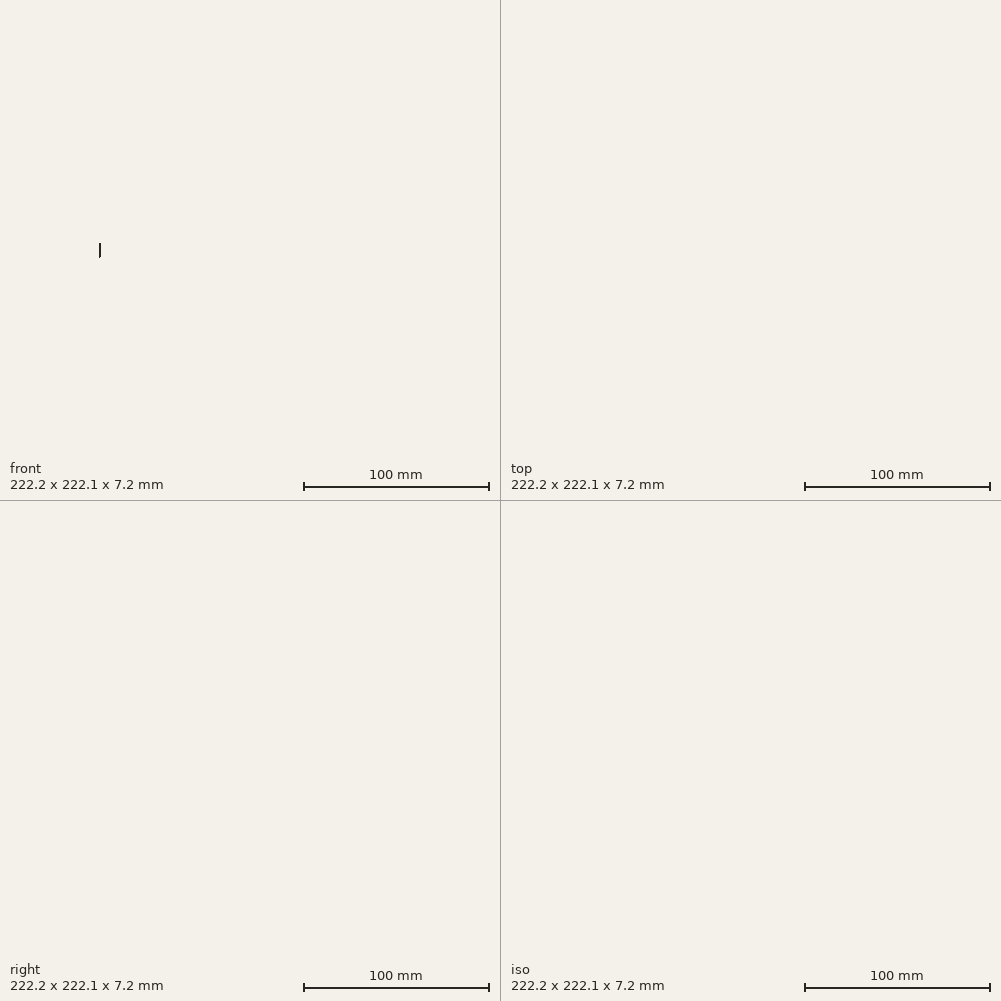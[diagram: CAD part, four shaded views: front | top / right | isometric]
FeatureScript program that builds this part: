
annotation { "Feature Type Name" : "Feature", "Feature Type Description" : "" }
export const myFeature = defineFeature(function(context is Context, id is Id, definition is map)
    precondition{}
    {
        {
            var Q0;
            Q0=qCreatedBy(makeId("Top.planeOp"),FACE);
            var sketch = newSketch(context, id + "F0", { "sketchPlane" : qUnion([Q0])});
            skCircle(sketch, "E0", {"center": v(0, 0) * mm, "radius": 101.6 * mm});
            skCircle(sketch, "E1", {"center": v(0, 0) * mm, "radius": 111.13 * mm});
            skSolve(sketch);
        }
        {
            var Q0;
            Q0=qSketchRegion(id+"F0",true);
            extrude(context, id + "F1", {"entities" : qUnion([Q0]), "depth" : 12.7 * mm});
        }
        {
            var Q0;
            Q0=makeQuery(id+"F1.opExtrude","CAP_FACE",FACE,{"disambiguationData":[OSD([sQuery(id+"F0.wireOp",EDGE,"E0"),sQuery(id+"F0.wireOp",EDGE,"E1")])],"isStart":false});
            var sketch = newSketch(context, id + "F2", { "sketchPlane" : qUnion([Q0])});
            skCircle(sketch, "E2", {"center": v(0, 0) * mm, "radius": 108.74 * mm, "construction": true});
            skCircle(sketch, "E3", {"center": v(0, 0) * mm, "radius": 112.9 * mm});
            skLineSegment(sketch, "E4", {"start": v(0, 0) * mm, "end": v(0, 111.13) * mm, "construction": true});
            skLineSegment(sketch, "E5", {"start": v(0, 0) * mm, "end": v(5.74, 110.98) * mm, "construction": true});
            skArc(sketch, "E6", {"start": v(1.35, 110.38) * mm, "mid": v(0.77, 110.93) * mm, "end": v(0, 111.13) * mm});
            skLineSegment(sketch, "E7", {"start": v(0, 0) * mm, "end": v(2.87, 111.09) * mm, "construction": true});
            skLineSegment(sketch, "E8", {"start": v(0, 111.12) * mm, "end": v(5.74, 110.98) * mm, "construction": true});
            skPoint(sketch, "E9", {"position": v(2.87, 111.05) * mm});
            skArc(sketch, "E10", {"start": v(2.16, 109.08) * mm, "mid": v(2.44, 108.81) * mm, "end": v(2.8, 108.7) * mm});
            skPoint(sketch, "E11", {"position": v(2.8, 108.7) * mm});
            skLineSegment(sketch, "E12", {"start": v(1.35, 110.38) * mm, "end": v(2.16, 109.08) * mm});
            skArc(sketch, "E13.MirrorCS", {"start": v(3.48, 109.05) * mm, "mid": v(3.19, 108.8) * mm, "end": v(2.8, 108.7) * mm});
            skLineSegment(sketch, "E14.MirrorCS", {"start": v(4.35, 110.3) * mm, "end": v(3.48, 109.05) * mm});
            skArc(sketch, "E15.MirrorCS", {"start": v(4.35, 110.3) * mm, "mid": v(4.96, 110.82) * mm, "end": v(5.74, 110.98) * mm});
            skArc(sketch, "E16.1.0", {"start": v(-4.34, 110.3) * mm, "mid": v(-4.94, 110.82) * mm, "end": v(-5.72, 110.98) * mm});
            skLineSegment(sketch, "E16.1.1", {"start": v(-4.34, 110.3) * mm, "end": v(-3.46, 109.05) * mm});
            skArc(sketch, "E16.1.2", {"start": v(-3.46, 109.05) * mm, "mid": v(-3.17, 108.8) * mm, "end": v(-2.8, 108.7) * mm});
            skArc(sketch, "E16.1.3", {"start": v(-2.14, 109.08) * mm, "mid": v(-2.42, 108.81) * mm, "end": v(-2.8, 108.7) * mm});
            skLineSegment(sketch, "E16.1.4", {"start": v(-1.33, 110.38) * mm, "end": v(-2.14, 109.08) * mm});
            skArc(sketch, "E16.1.5", {"start": v(-1.33, 110.38) * mm, "mid": v(-0.75, 110.93) * mm, "end": v(0.02, 111.12) * mm});
            skArc(sketch, "E16.2.0", {"start": v(-10, 109.93) * mm, "mid": v(-10.64, 110.42) * mm, "end": v(-11.43, 110.54) * mm});
            skLineSegment(sketch, "E16.2.1", {"start": v(-10, 109.93) * mm, "end": v(-9.07, 108.72) * mm});
            skArc(sketch, "E16.2.2", {"start": v(-9.07, 108.72) * mm, "mid": v(-8.77, 108.49) * mm, "end": v(-8.38, 108.42) * mm});
            skArc(sketch, "E16.2.3", {"start": v(-7.75, 108.83) * mm, "mid": v(-8.02, 108.54) * mm, "end": v(-8.38, 108.42) * mm});
            skLineSegment(sketch, "E16.2.4", {"start": v(-7, 110.16) * mm, "end": v(-7.75, 108.83) * mm});
            skArc(sketch, "E16.2.5", {"start": v(-7, 110.16) * mm, "mid": v(-6.46, 110.74) * mm, "end": v(-5.7, 110.98) * mm});
            skArc(sketch, "E16.3.0", {"start": v(-15.66, 109.27) * mm, "mid": v(-16.3, 109.72) * mm, "end": v(-17.1, 109.8) * mm});
            skLineSegment(sketch, "E16.3.1", {"start": v(-15.66, 109.27) * mm, "end": v(-14.66, 108.11) * mm});
            skArc(sketch, "E16.3.2", {"start": v(-14.66, 108.11) * mm, "mid": v(-14.34, 107.9) * mm, "end": v(-13.95, 107.84) * mm});
            skArc(sketch, "E16.3.3", {"start": v(-13.34, 108.28) * mm, "mid": v(-13.6, 107.99) * mm, "end": v(-13.95, 107.84) * mm});
            skLineSegment(sketch, "E16.3.4", {"start": v(-12.67, 109.66) * mm, "end": v(-13.34, 108.28) * mm});
            skArc(sketch, "E16.3.5", {"start": v(-12.67, 109.66) * mm, "mid": v(-12.15, 110.26) * mm, "end": v(-11.4, 110.54) * mm});
            skArc(sketch, "E16.4.0", {"start": v(-21.26, 108.32) * mm, "mid": v(-21.94, 108.74) * mm, "end": v(-22.73, 108.78) * mm});
            skLineSegment(sketch, "E16.4.1", {"start": v(-21.26, 108.32) * mm, "end": v(-20.2, 107.22) * mm});
            skArc(sketch, "E16.4.2", {"start": v(-20.2, 107.22) * mm, "mid": v(-19.87, 107) * mm, "end": v(-19.49, 106.98) * mm});
            skArc(sketch, "E16.4.3", {"start": v(-18.9, 107.45) * mm, "mid": v(-19.13, 107.14) * mm, "end": v(-19.49, 106.98) * mm});
            skLineSegment(sketch, "E16.4.4", {"start": v(-18.3, 108.86) * mm, "end": v(-18.9, 107.45) * mm});
            skArc(sketch, "E16.4.5", {"start": v(-18.3, 108.86) * mm, "mid": v(-17.81, 109.49) * mm, "end": v(-17.08, 109.8) * mm});
            skArc(sketch, "E16.5.0", {"start": v(-26.8, 107.08) * mm, "mid": v(-27.5, 107.46) * mm, "end": v(-28.3, 107.46) * mm});
            skLineSegment(sketch, "E16.5.1", {"start": v(-26.8, 107.08) * mm, "end": v(-25.7, 106.03) * mm});
            skArc(sketch, "E16.5.2", {"start": v(-25.7, 106.03) * mm, "mid": v(-25.36, 105.84) * mm, "end": v(-24.97, 105.84) * mm});
            skArc(sketch, "E16.5.3", {"start": v(-24.4, 106.34) * mm, "mid": v(-24.62, 106.02) * mm, "end": v(-24.97, 105.84) * mm});
            skLineSegment(sketch, "E16.5.4", {"start": v(-23.88, 107.77) * mm, "end": v(-24.4, 106.34) * mm});
            skArc(sketch, "E16.5.5", {"start": v(-23.88, 107.77) * mm, "mid": v(-23.43, 108.43) * mm, "end": v(-22.71, 108.78) * mm});
            skArc(sketch, "E16.6.0", {"start": v(-32.28, 105.56) * mm, "mid": v(-33, 105.9) * mm, "end": v(-33.8, 105.86) * mm});
            skLineSegment(sketch, "E16.6.1", {"start": v(-32.28, 105.56) * mm, "end": v(-31.12, 104.57) * mm});
            skArc(sketch, "E16.6.2", {"start": v(-31.12, 104.57) * mm, "mid": v(-30.77, 104.4) * mm, "end": v(-30.38, 104.41) * mm});
            skArc(sketch, "E16.6.3", {"start": v(-29.85, 104.94) * mm, "mid": v(-30.05, 104.6) * mm, "end": v(-30.38, 104.41) * mm});
            skLineSegment(sketch, "E16.6.4", {"start": v(-29.4, 106.4) * mm, "end": v(-29.85, 104.94) * mm});
            skArc(sketch, "E16.6.5", {"start": v(-29.4, 106.4) * mm, "mid": v(-28.98, 107.08) * mm, "end": v(-28.28, 107.47) * mm});
            skArc(sketch, "E16.7.0", {"start": v(-37.68, 103.76) * mm, "mid": v(-38.4, 104.07) * mm, "end": v(-39.2, 103.98) * mm});
            skLineSegment(sketch, "E16.7.1", {"start": v(-37.68, 103.76) * mm, "end": v(-36.46, 102.83) * mm});
            skArc(sketch, "E16.7.2", {"start": v(-36.46, 102.83) * mm, "mid": v(-36.1, 102.68) * mm, "end": v(-35.72, 102.71) * mm});
            skArc(sketch, "E16.7.3", {"start": v(-35.21, 103.26) * mm, "mid": v(-35.4, 102.92) * mm, "end": v(-35.72, 102.71) * mm});
            skLineSegment(sketch, "E16.7.4", {"start": v(-34.83, 104.75) * mm, "end": v(-35.21, 103.26) * mm});
            skArc(sketch, "E16.7.5", {"start": v(-34.83, 104.75) * mm, "mid": v(-34.45, 105.44) * mm, "end": v(-33.78, 105.87) * mm});
            skArc(sketch, "E16.8.0", {"start": v(-42.97, 101.68) * mm, "mid": v(-43.71, 101.95) * mm, "end": v(-44.5, 101.83) * mm});
            skLineSegment(sketch, "E16.8.1", {"start": v(-42.97, 101.68) * mm, "end": v(-41.7, 100.82) * mm});
            skArc(sketch, "E16.8.2", {"start": v(-41.7, 100.82) * mm, "mid": v(-41.34, 100.68) * mm, "end": v(-40.96, 100.74) * mm});
            skArc(sketch, "E16.8.3", {"start": v(-40.48, 101.31) * mm, "mid": v(-40.65, 100.96) * mm, "end": v(-40.96, 100.74) * mm});
            skLineSegment(sketch, "E16.8.4", {"start": v(-40.18, 102.81) * mm, "end": v(-40.48, 101.31) * mm});
            skArc(sketch, "E16.8.5", {"start": v(-40.18, 102.81) * mm, "mid": v(-39.83, 103.53) * mm, "end": v(-39.18, 103.99) * mm});
            skArc(sketch, "E16.9.0", {"start": v(-48.14, 99.33) * mm, "mid": v(-48.9, 99.57) * mm, "end": v(-49.68, 99.4) * mm});
            skLineSegment(sketch, "E16.9.1", {"start": v(-48.14, 99.33) * mm, "end": v(-46.84, 98.54) * mm});
            skArc(sketch, "E16.9.2", {"start": v(-46.84, 98.54) * mm, "mid": v(-46.47, 98.42) * mm, "end": v(-46.1, 98.5) * mm});
            skArc(sketch, "E16.9.3", {"start": v(-45.64, 99.1) * mm, "mid": v(-45.79, 98.74) * mm, "end": v(-46.1, 98.5) * mm});
            skLineSegment(sketch, "E16.9.4", {"start": v(-45.42, 100.6) * mm, "end": v(-45.64, 99.1) * mm});
            skArc(sketch, "E16.9.5", {"start": v(-45.42, 100.6) * mm, "mid": v(-45.11, 101.34) * mm, "end": v(-44.48, 101.83) * mm});
            skArc(sketch, "E16.10.0", {"start": v(-53.2, 96.72) * mm, "mid": v(-53.97, 96.92) * mm, "end": v(-54.73, 96.71) * mm});
            skLineSegment(sketch, "E16.10.1", {"start": v(-53.2, 96.72) * mm, "end": v(-51.85, 96) * mm});
            skArc(sketch, "E16.10.2", {"start": v(-51.85, 96) * mm, "mid": v(-51.48, 95.9) * mm, "end": v(-51.1, 95.99) * mm});
            skArc(sketch, "E16.10.3", {"start": v(-50.68, 96.62) * mm, "mid": v(-50.81, 96.25) * mm, "end": v(-51.1, 95.99) * mm});
            skLineSegment(sketch, "E16.10.4", {"start": v(-50.54, 98.14) * mm, "end": v(-50.68, 96.62) * mm});
            skArc(sketch, "E16.10.5", {"start": v(-50.54, 98.14) * mm, "mid": v(-50.27, 98.89) * mm, "end": v(-49.67, 99.4) * mm});
            skArc(sketch, "E16.11.0", {"start": v(-58.1, 93.86) * mm, "mid": v(-58.88, 94) * mm, "end": v(-59.64, 93.76) * mm});
            skLineSegment(sketch, "E16.11.1", {"start": v(-58.1, 93.86) * mm, "end": v(-56.72, 93.2) * mm});
            skArc(sketch, "E16.11.2", {"start": v(-56.72, 93.2) * mm, "mid": v(-56.34, 93.12) * mm, "end": v(-55.97, 93.23) * mm});
            skArc(sketch, "E16.11.3", {"start": v(-55.59, 93.88) * mm, "mid": v(-55.7, 93.5) * mm, "end": v(-55.97, 93.23) * mm});
            skLineSegment(sketch, "E16.11.4", {"start": v(-55.52, 95.4) * mm, "end": v(-55.59, 93.88) * mm});
            skArc(sketch, "E16.11.5", {"start": v(-55.52, 95.4) * mm, "mid": v(-55.3, 96.17) * mm, "end": v(-54.72, 96.72) * mm});
            skArc(sketch, "E16.12.0", {"start": v(-62.86, 90.74) * mm, "mid": v(-63.64, 90.85) * mm, "end": v(-64.39, 90.57) * mm});
            skLineSegment(sketch, "E16.12.1", {"start": v(-62.86, 90.74) * mm, "end": v(-61.45, 90.15) * mm});
            skArc(sketch, "E16.12.2", {"start": v(-61.45, 90.15) * mm, "mid": v(-61.06, 90.1) * mm, "end": v(-60.7, 90.23) * mm});
            skArc(sketch, "E16.12.3", {"start": v(-60.35, 90.9) * mm, "mid": v(-60.44, 90.52) * mm, "end": v(-60.7, 90.23) * mm});
            skLineSegment(sketch, "E16.12.4", {"start": v(-60.36, 92.42) * mm, "end": v(-60.35, 90.9) * mm});
            skArc(sketch, "E16.12.5", {"start": v(-60.36, 92.42) * mm, "mid": v(-60.17, 93.2) * mm, "end": v(-59.63, 93.77) * mm});
            skArc(sketch, "E16.13.0", {"start": v(-67.45, 87.39) * mm, "mid": v(-68.24, 87.46) * mm, "end": v(-68.97, 87.14) * mm});
            skLineSegment(sketch, "E16.13.1", {"start": v(-67.45, 87.39) * mm, "end": v(-66, 86.87) * mm});
            skArc(sketch, "E16.13.2", {"start": v(-66, 86.87) * mm, "mid": v(-65.62, 86.83) * mm, "end": v(-65.26, 86.98) * mm});
            skArc(sketch, "E16.13.3", {"start": v(-64.95, 87.67) * mm, "mid": v(-65.02, 87.28) * mm, "end": v(-65.26, 86.98) * mm});
            skLineSegment(sketch, "E16.13.4", {"start": v(-65.04, 89.2) * mm, "end": v(-64.95, 87.67) * mm});
            skArc(sketch, "E16.13.5", {"start": v(-65.04, 89.2) * mm, "mid": v(-64.89, 89.97) * mm, "end": v(-64.37, 90.58) * mm});
            skArc(sketch, "E16.14.0", {"start": v(-71.85, 83.8) * mm, "mid": v(-72.65, 83.83) * mm, "end": v(-73.36, 83.47) * mm});
            skLineSegment(sketch, "E16.14.1", {"start": v(-71.85, 83.8) * mm, "end": v(-70.4, 83.36) * mm});
            skArc(sketch, "E16.14.2", {"start": v(-70.4, 83.36) * mm, "mid": v(-70, 83.34) * mm, "end": v(-69.65, 83.5) * mm});
            skArc(sketch, "E16.14.3", {"start": v(-69.37, 84.2) * mm, "mid": v(-69.43, 83.82) * mm, "end": v(-69.65, 83.5) * mm});
            skLineSegment(sketch, "E16.14.4", {"start": v(-69.54, 85.72) * mm, "end": v(-69.37, 84.2) * mm});
            skArc(sketch, "E16.14.5", {"start": v(-69.54, 85.72) * mm, "mid": v(-69.43, 86.51) * mm, "end": v(-68.95, 87.15) * mm});
            skArc(sketch, "E16.15.0", {"start": v(-76.07, 79.99) * mm, "mid": v(-76.87, 79.98) * mm, "end": v(-77.56, 79.58) * mm});
            skLineSegment(sketch, "E16.15.1", {"start": v(-76.07, 79.99) * mm, "end": v(-74.59, 79.62) * mm});
            skArc(sketch, "E16.15.2", {"start": v(-74.59, 79.62) * mm, "mid": v(-74.2, 79.63) * mm, "end": v(-73.86, 79.81) * mm});
            skArc(sketch, "E16.15.3", {"start": v(-73.62, 80.52) * mm, "mid": v(-73.65, 80.14) * mm, "end": v(-73.86, 79.81) * mm});
            skLineSegment(sketch, "E16.15.4", {"start": v(-73.86, 82.03) * mm, "end": v(-73.62, 80.52) * mm});
            skArc(sketch, "E16.15.5", {"start": v(-73.86, 82.03) * mm, "mid": v(-73.8, 82.82) * mm, "end": v(-73.35, 83.48) * mm});
            skArc(sketch, "E16.16.0", {"start": v(-80.09, 75.97) * mm, "mid": v(-80.88, 75.91) * mm, "end": v(-81.55, 75.48) * mm});
            skLineSegment(sketch, "E16.16.1", {"start": v(-80.09, 75.97) * mm, "end": v(-78.59, 75.68) * mm});
            skArc(sketch, "E16.16.2", {"start": v(-78.59, 75.68) * mm, "mid": v(-78.2, 75.7) * mm, "end": v(-77.87, 75.9) * mm});
            skArc(sketch, "E16.16.3", {"start": v(-77.66, 76.63) * mm, "mid": v(-77.68, 76.24) * mm, "end": v(-77.87, 75.9) * mm});
            skLineSegment(sketch, "E16.16.4", {"start": v(-77.99, 78.12) * mm, "end": v(-77.66, 76.63) * mm});
            skArc(sketch, "E16.16.5", {"start": v(-77.99, 78.12) * mm, "mid": v(-77.96, 78.91) * mm, "end": v(-77.55, 79.6) * mm});
            skArc(sketch, "E16.17.0", {"start": v(-83.9, 71.74) * mm, "mid": v(-84.68, 71.65) * mm, "end": v(-85.33, 71.19) * mm});
            skLineSegment(sketch, "E16.17.1", {"start": v(-83.9, 71.74) * mm, "end": v(-82.38, 71.53) * mm});
            skArc(sketch, "E16.17.2", {"start": v(-82.38, 71.53) * mm, "mid": v(-82, 71.57) * mm, "end": v(-81.68, 71.8) * mm});
            skArc(sketch, "E16.17.3", {"start": v(-81.5, 72.53) * mm, "mid": v(-81.5, 72.14) * mm, "end": v(-81.68, 71.8) * mm});
            skLineSegment(sketch, "E16.17.4", {"start": v(-81.9, 74) * mm, "end": v(-81.5, 72.53) * mm});
            skArc(sketch, "E16.17.5", {"start": v(-81.9, 74) * mm, "mid": v(-81.92, 74.8) * mm, "end": v(-81.54, 75.5) * mm});
            skArc(sketch, "E16.18.0", {"start": v(-87.48, 67.33) * mm, "mid": v(-88.26, 67.2) * mm, "end": v(-88.88, 66.7) * mm});
            skLineSegment(sketch, "E16.18.1", {"start": v(-87.48, 67.33) * mm, "end": v(-85.95, 67.2) * mm});
            skArc(sketch, "E16.18.2", {"start": v(-85.95, 67.2) * mm, "mid": v(-85.57, 67.26) * mm, "end": v(-85.26, 67.5) * mm});
            skArc(sketch, "E16.18.3", {"start": v(-85.13, 68.23) * mm, "mid": v(-85.1, 67.85) * mm, "end": v(-85.26, 67.5) * mm});
            skLineSegment(sketch, "E16.18.4", {"start": v(-85.6, 69.69) * mm, "end": v(-85.13, 68.23) * mm});
            skArc(sketch, "E16.18.5", {"start": v(-85.6, 69.69) * mm, "mid": v(-85.66, 70.48) * mm, "end": v(-85.32, 71.2) * mm});
            skArc(sketch, "E16.19.0", {"start": v(-90.83, 62.74) * mm, "mid": v(-91.6, 62.56) * mm, "end": v(-92.2, 62.03) * mm});
            skLineSegment(sketch, "E16.19.1", {"start": v(-90.83, 62.74) * mm, "end": v(-89.3, 62.68) * mm});
            skArc(sketch, "E16.19.2", {"start": v(-89.3, 62.68) * mm, "mid": v(-88.92, 62.76) * mm, "end": v(-88.62, 63.02) * mm});
            skArc(sketch, "E16.19.3", {"start": v(-88.53, 63.76) * mm, "mid": v(-88.48, 63.38) * mm, "end": v(-88.62, 63.02) * mm});
            skLineSegment(sketch, "E16.19.4", {"start": v(-89.08, 65.19) * mm, "end": v(-88.53, 63.76) * mm});
            skArc(sketch, "E16.19.5", {"start": v(-89.08, 65.19) * mm, "mid": v(-89.17, 65.98) * mm, "end": v(-88.87, 66.71) * mm});
            skArc(sketch, "E16.20.0", {"start": v(-93.93, 57.98) * mm, "mid": v(-94.7, 57.76) * mm, "end": v(-95.27, 57.2) * mm});
            skLineSegment(sketch, "E16.20.1", {"start": v(-93.93, 57.98) * mm, "end": v(-92.4, 58) * mm});
            skArc(sketch, "E16.20.2", {"start": v(-92.4, 58) * mm, "mid": v(-92.03, 58.1) * mm, "end": v(-91.75, 58.37) * mm});
            skArc(sketch, "E16.20.3", {"start": v(-91.7, 59.12) * mm, "mid": v(-91.63, 58.74) * mm, "end": v(-91.75, 58.37) * mm});
            skLineSegment(sketch, "E16.20.4", {"start": v(-92.32, 60.51) * mm, "end": v(-91.7, 59.12) * mm});
            skArc(sketch, "E16.20.5", {"start": v(-92.32, 60.51) * mm, "mid": v(-92.45, 61.3) * mm, "end": v(-92.19, 62.05) * mm});
            skArc(sketch, "E16.21.0", {"start": v(-96.8, 53.06) * mm, "mid": v(-97.55, 52.81) * mm, "end": v(-98.09, 52.23) * mm});
            skLineSegment(sketch, "E16.21.1", {"start": v(-96.8, 53.06) * mm, "end": v(-95.27, 53.17) * mm});
            skArc(sketch, "E16.21.2", {"start": v(-95.27, 53.17) * mm, "mid": v(-94.9, 53.29) * mm, "end": v(-94.63, 53.57) * mm});
            skArc(sketch, "E16.21.3", {"start": v(-94.62, 54.32) * mm, "mid": v(-94.53, 53.94) * mm, "end": v(-94.63, 53.57) * mm});
            skLineSegment(sketch, "E16.21.4", {"start": v(-95.31, 55.68) * mm, "end": v(-94.62, 54.32) * mm});
            skArc(sketch, "E16.21.5", {"start": v(-95.31, 55.68) * mm, "mid": v(-95.49, 56.46) * mm, "end": v(-95.26, 57.22) * mm});
            skArc(sketch, "E16.22.0", {"start": v(-99.4, 48.01) * mm, "mid": v(-100.14, 47.72) * mm, "end": v(-100.65, 47.1) * mm});
            skLineSegment(sketch, "E16.22.1", {"start": v(-99.4, 48.01) * mm, "end": v(-97.88, 48.2) * mm});
            skArc(sketch, "E16.22.2", {"start": v(-97.88, 48.2) * mm, "mid": v(-97.52, 48.33) * mm, "end": v(-97.27, 48.63) * mm});
            skArc(sketch, "E16.22.3", {"start": v(-97.29, 49.38) * mm, "mid": v(-97.18, 49) * mm, "end": v(-97.27, 48.63) * mm});
            skLineSegment(sketch, "E16.22.4", {"start": v(-98.05, 50.7) * mm, "end": v(-97.29, 49.38) * mm});
            skArc(sketch, "E16.22.5", {"start": v(-98.05, 50.7) * mm, "mid": v(-98.27, 51.47) * mm, "end": v(-98.08, 52.24) * mm});
            skArc(sketch, "E16.23.0", {"start": v(-101.74, 42.83) * mm, "mid": v(-102.46, 42.5) * mm, "end": v(-102.94, 41.86) * mm});
            skLineSegment(sketch, "E16.23.1", {"start": v(-101.74, 42.83) * mm, "end": v(-100.23, 43.1) * mm});
            skArc(sketch, "E16.23.2", {"start": v(-100.23, 43.1) * mm, "mid": v(-99.88, 43.25) * mm, "end": v(-99.64, 43.55) * mm});
            skArc(sketch, "E16.23.3", {"start": v(-99.7, 44.3) * mm, "mid": v(-99.58, 43.94) * mm, "end": v(-99.64, 43.55) * mm});
            skLineSegment(sketch, "E16.23.4", {"start": v(-100.53, 45.59) * mm, "end": v(-99.7, 44.3) * mm});
            skArc(sketch, "E16.23.5", {"start": v(-100.53, 45.59) * mm, "mid": v(-100.78, 46.34) * mm, "end": v(-100.64, 47.12) * mm});
            skArc(sketch, "E16.24.0", {"start": v(-103.8, 37.54) * mm, "mid": v(-104.52, 37.17) * mm, "end": v(-104.96, 36.5) * mm});
            skLineSegment(sketch, "E16.24.1", {"start": v(-103.8, 37.54) * mm, "end": v(-102.32, 37.87) * mm});
            skArc(sketch, "E16.24.2", {"start": v(-102.32, 37.87) * mm, "mid": v(-101.97, 38.05) * mm, "end": v(-101.75, 38.37) * mm});
            skArc(sketch, "E16.24.3", {"start": v(-101.85, 39.11) * mm, "mid": v(-101.7, 38.75) * mm, "end": v(-101.75, 38.37) * mm});
            skLineSegment(sketch, "E16.24.4", {"start": v(-102.75, 40.35) * mm, "end": v(-101.85, 39.11) * mm});
            skArc(sketch, "E16.24.5", {"start": v(-102.75, 40.35) * mm, "mid": v(-103.04, 41.1) * mm, "end": v(-102.93, 41.88) * mm});
            skArc(sketch, "E16.25.0", {"start": v(-105.6, 32.14) * mm, "mid": v(-106.29, 31.74) * mm, "end": v(-106.7, 31.06) * mm});
            skLineSegment(sketch, "E16.25.1", {"start": v(-105.6, 32.14) * mm, "end": v(-104.13, 32.56) * mm});
            skArc(sketch, "E16.25.2", {"start": v(-104.13, 32.56) * mm, "mid": v(-103.8, 32.75) * mm, "end": v(-103.6, 33.08) * mm});
            skArc(sketch, "E16.25.3", {"start": v(-103.73, 33.82) * mm, "mid": v(-103.57, 33.47) * mm, "end": v(-103.6, 33.08) * mm});
            skLineSegment(sketch, "E16.25.4", {"start": v(-104.69, 35) * mm, "end": v(-103.73, 33.82) * mm});
            skArc(sketch, "E16.25.5", {"start": v(-104.69, 35) * mm, "mid": v(-105.02, 35.73) * mm, "end": v(-104.95, 36.53) * mm});
            skArc(sketch, "E16.26.0", {"start": v(-107.12, 26.66) * mm, "mid": v(-107.78, 26.23) * mm, "end": v(-108.15, 25.52) * mm});
            skLineSegment(sketch, "E16.26.1", {"start": v(-107.12, 26.66) * mm, "end": v(-105.67, 27.15) * mm});
            skArc(sketch, "E16.26.2", {"start": v(-105.67, 27.15) * mm, "mid": v(-105.34, 27.36) * mm, "end": v(-105.16, 27.7) * mm});
            skArc(sketch, "E16.26.3", {"start": v(-105.33, 28.43) * mm, "mid": v(-105.15, 28.1) * mm, "end": v(-105.16, 27.7) * mm});
            skLineSegment(sketch, "E16.26.4", {"start": v(-106.35, 29.57) * mm, "end": v(-105.33, 28.43) * mm});
            skArc(sketch, "E16.26.5", {"start": v(-106.35, 29.57) * mm, "mid": v(-106.72, 30.28) * mm, "end": v(-106.7, 31.08) * mm});
            skArc(sketch, "E16.27.0", {"start": v(-108.35, 21.11) * mm, "mid": v(-109, 20.64) * mm, "end": v(-109.32, 19.92) * mm});
            skLineSegment(sketch, "E16.27.1", {"start": v(-108.35, 21.11) * mm, "end": v(-106.93, 21.68) * mm});
            skArc(sketch, "E16.27.2", {"start": v(-106.93, 21.68) * mm, "mid": v(-106.61, 21.9) * mm, "end": v(-106.44, 22.25) * mm});
            skArc(sketch, "E16.27.3", {"start": v(-106.66, 22.97) * mm, "mid": v(-106.46, 22.64) * mm, "end": v(-106.44, 22.25) * mm});
            skLineSegment(sketch, "E16.27.4", {"start": v(-107.73, 24.06) * mm, "end": v(-106.66, 22.97) * mm});
            skArc(sketch, "E16.27.5", {"start": v(-107.73, 24.06) * mm, "mid": v(-108.13, 24.75) * mm, "end": v(-108.15, 25.54) * mm});
            skArc(sketch, "E16.28.0", {"start": v(-109.3, 15.5) * mm, "mid": v(-109.9, 15) * mm, "end": v(-110.2, 14.27) * mm});
            skLineSegment(sketch, "E16.28.1", {"start": v(-109.3, 15.5) * mm, "end": v(-107.9, 16.14) * mm});
            skArc(sketch, "E16.28.2", {"start": v(-107.9, 16.14) * mm, "mid": v(-107.6, 16.39) * mm, "end": v(-107.45, 16.74) * mm});
            skArc(sketch, "E16.28.3", {"start": v(-107.7, 17.45) * mm, "mid": v(-107.48, 17.13) * mm, "end": v(-107.45, 16.74) * mm});
            skLineSegment(sketch, "E16.28.4", {"start": v(-108.83, 18.48) * mm, "end": v(-107.7, 17.45) * mm});
            skArc(sketch, "E16.28.5", {"start": v(-108.83, 18.48) * mm, "mid": v(-109.26, 19.15) * mm, "end": v(-109.32, 19.94) * mm});
            skArc(sketch, "E16.29.0", {"start": v(-109.94, 9.86) * mm, "mid": v(-110.54, 9.33) * mm, "end": v(-110.8, 8.58) * mm});
            skLineSegment(sketch, "E16.29.1", {"start": v(-109.94, 9.86) * mm, "end": v(-108.59, 10.57) * mm});
            skArc(sketch, "E16.29.2", {"start": v(-108.59, 10.57) * mm, "mid": v(-108.3, 10.83) * mm, "end": v(-108.17, 11.19) * mm});
            skArc(sketch, "E16.29.3", {"start": v(-108.45, 11.89) * mm, "mid": v(-108.22, 11.57) * mm, "end": v(-108.17, 11.19) * mm});
            skLineSegment(sketch, "E16.29.4", {"start": v(-109.63, 12.85) * mm, "end": v(-108.45, 11.89) * mm});
            skArc(sketch, "E16.29.5", {"start": v(-109.63, 12.85) * mm, "mid": v(-110.1, 13.5) * mm, "end": v(-110.2, 14.29) * mm});
            skArc(sketch, "E16.30.0", {"start": v(-110.3, 4.19) * mm, "mid": v(-110.87, 3.63) * mm, "end": v(-111.09, 2.86) * mm});
            skLineSegment(sketch, "E16.30.1", {"start": v(-110.3, 4.19) * mm, "end": v(-108.99, 4.96) * mm});
            skArc(sketch, "E16.30.2", {"start": v(-108.99, 4.96) * mm, "mid": v(-108.71, 5.24) * mm, "end": v(-108.6, 5.6) * mm});
            skArc(sketch, "E16.30.3", {"start": v(-108.92, 6.29) * mm, "mid": v(-108.67, 5.99) * mm, "end": v(-108.6, 5.6) * mm});
            skLineSegment(sketch, "E16.30.4", {"start": v(-110.15, 7.2) * mm, "end": v(-108.92, 6.29) * mm});
            skArc(sketch, "E16.30.5", {"start": v(-110.15, 7.2) * mm, "mid": v(-110.65, 7.81) * mm, "end": v(-110.8, 8.6) * mm});
            skArc(sketch, "E16.31.0", {"start": v(-110.38, -1.5) * mm, "mid": v(-110.9, -2.09) * mm, "end": v(-111.09, -2.86) * mm});
            skLineSegment(sketch, "E16.31.1", {"start": v(-110.38, -1.5) * mm, "end": v(-109.1, -0.65) * mm});
            skArc(sketch, "E16.31.2", {"start": v(-109.1, -0.65) * mm, "mid": v(-108.84, -0.37) * mm, "end": v(-108.74, 0) * mm});
            skArc(sketch, "E16.31.3", {"start": v(-109.1, 0.67) * mm, "mid": v(-108.84, 0.38) * mm, "end": v(-108.74, 0) * mm});
            skLineSegment(sketch, "E16.31.4", {"start": v(-110.38, 1.51) * mm, "end": v(-109.1, 0.67) * mm});
            skArc(sketch, "E16.31.5", {"start": v(-110.38, 1.51) * mm, "mid": v(-110.9, 2.1) * mm, "end": v(-111.09, 2.88) * mm});
            skArc(sketch, "E16.32.0", {"start": v(-110.15, -7.18) * mm, "mid": v(-110.65, -7.8) * mm, "end": v(-110.8, -8.58) * mm});
            skLineSegment(sketch, "E16.32.1", {"start": v(-110.15, -7.18) * mm, "end": v(-108.92, -6.27) * mm});
            skArc(sketch, "E16.32.2", {"start": v(-108.92, -6.27) * mm, "mid": v(-108.68, -5.97) * mm, "end": v(-108.6, -5.59) * mm});
            skArc(sketch, "E16.32.3", {"start": v(-109, -4.95) * mm, "mid": v(-108.71, -5.22) * mm, "end": v(-108.6, -5.59) * mm});
            skLineSegment(sketch, "E16.32.4", {"start": v(-110.3, -4.17) * mm, "end": v(-109, -4.95) * mm});
            skArc(sketch, "E16.32.5", {"start": v(-110.3, -4.17) * mm, "mid": v(-110.87, -3.6) * mm, "end": v(-111.09, -2.84) * mm});
            skArc(sketch, "E16.33.0", {"start": v(-109.64, -12.84) * mm, "mid": v(-110.1, -13.48) * mm, "end": v(-110.2, -14.27) * mm});
            skLineSegment(sketch, "E16.33.1", {"start": v(-109.64, -12.84) * mm, "end": v(-108.45, -11.87) * mm});
            skArc(sketch, "E16.33.2", {"start": v(-108.45, -11.87) * mm, "mid": v(-108.22, -11.56) * mm, "end": v(-108.17, -11.17) * mm});
            skArc(sketch, "E16.33.3", {"start": v(-108.6, -10.55) * mm, "mid": v(-108.3, -10.8) * mm, "end": v(-108.17, -11.17) * mm});
            skLineSegment(sketch, "E16.33.4", {"start": v(-109.95, -9.84) * mm, "end": v(-108.6, -10.55) * mm});
            skArc(sketch, "E16.33.5", {"start": v(-109.95, -9.84) * mm, "mid": v(-110.54, -9.31) * mm, "end": v(-110.8, -8.56) * mm});
            skArc(sketch, "E16.34.0", {"start": v(-108.83, -18.46) * mm, "mid": v(-109.27, -19.13) * mm, "end": v(-109.32, -19.92) * mm});
            skLineSegment(sketch, "E16.34.1", {"start": v(-108.83, -18.46) * mm, "end": v(-107.7, -17.44) * mm});
            skArc(sketch, "E16.34.2", {"start": v(-107.7, -17.44) * mm, "mid": v(-107.49, -17.11) * mm, "end": v(-107.45, -16.73) * mm});
            skArc(sketch, "E16.34.3", {"start": v(-107.9, -16.13) * mm, "mid": v(-107.6, -16.37) * mm, "end": v(-107.45, -16.73) * mm});
            skLineSegment(sketch, "E16.34.4", {"start": v(-109.3, -15.5) * mm, "end": v(-107.9, -16.13) * mm});
            skArc(sketch, "E16.34.5", {"start": v(-109.3, -15.5) * mm, "mid": v(-109.91, -14.99) * mm, "end": v(-110.2, -14.25) * mm});
            skArc(sketch, "E16.35.0", {"start": v(-107.74, -24.04) * mm, "mid": v(-108.14, -24.73) * mm, "end": v(-108.15, -25.52) * mm});
            skLineSegment(sketch, "E16.35.1", {"start": v(-107.74, -24.04) * mm, "end": v(-106.66, -22.96) * mm});
            skArc(sketch, "E16.35.2", {"start": v(-106.66, -22.96) * mm, "mid": v(-106.46, -22.62) * mm, "end": v(-106.45, -22.24) * mm});
            skArc(sketch, "E16.35.3", {"start": v(-106.93, -21.66) * mm, "mid": v(-106.62, -21.89) * mm, "end": v(-106.45, -22.24) * mm});
            skLineSegment(sketch, "E16.35.4", {"start": v(-108.35, -21.1) * mm, "end": v(-106.93, -21.66) * mm});
            skArc(sketch, "E16.35.5", {"start": v(-108.35, -21.1) * mm, "mid": v(-109, -20.63) * mm, "end": v(-109.33, -19.9) * mm});
            skArc(sketch, "E16.36.0", {"start": v(-106.36, -29.56) * mm, "mid": v(-106.72, -30.26) * mm, "end": v(-106.7, -31.06) * mm});
            skLineSegment(sketch, "E16.36.1", {"start": v(-106.36, -29.56) * mm, "end": v(-105.34, -28.42) * mm});
            skArc(sketch, "E16.36.2", {"start": v(-105.34, -28.42) * mm, "mid": v(-105.16, -28.07) * mm, "end": v(-105.16, -27.69) * mm});
            skArc(sketch, "E16.36.3", {"start": v(-105.67, -27.14) * mm, "mid": v(-105.35, -27.35) * mm, "end": v(-105.16, -27.69) * mm});
            skLineSegment(sketch, "E16.36.4", {"start": v(-107.12, -26.65) * mm, "end": v(-105.67, -27.14) * mm});
            skArc(sketch, "E16.36.5", {"start": v(-107.12, -26.65) * mm, "mid": v(-107.79, -26.21) * mm, "end": v(-108.16, -25.5) * mm});
            skArc(sketch, "E16.37.0", {"start": v(-104.7, -35) * mm, "mid": v(-105.02, -35.72) * mm, "end": v(-104.96, -36.5) * mm});
            skLineSegment(sketch, "E16.37.1", {"start": v(-104.7, -35) * mm, "end": v(-103.73, -33.8) * mm});
            skArc(sketch, "E16.37.2", {"start": v(-103.73, -33.8) * mm, "mid": v(-103.57, -33.45) * mm, "end": v(-103.6, -33.06) * mm});
            skArc(sketch, "E16.37.3", {"start": v(-104.14, -32.54) * mm, "mid": v(-103.8, -32.73) * mm, "end": v(-103.6, -33.06) * mm});
            skLineSegment(sketch, "E16.37.4", {"start": v(-105.6, -32.13) * mm, "end": v(-104.14, -32.54) * mm});
            skArc(sketch, "E16.37.5", {"start": v(-105.6, -32.13) * mm, "mid": v(-106.3, -31.72) * mm, "end": v(-106.7, -31.04) * mm});
            skArc(sketch, "E16.38.0", {"start": v(-102.75, -40.33) * mm, "mid": v(-103.04, -41.08) * mm, "end": v(-102.94, -41.86) * mm});
            skLineSegment(sketch, "E16.38.1", {"start": v(-102.75, -40.33) * mm, "end": v(-101.86, -39.1) * mm});
            skArc(sketch, "E16.38.2", {"start": v(-101.86, -39.1) * mm, "mid": v(-101.71, -38.74) * mm, "end": v(-101.76, -38.35) * mm});
            skArc(sketch, "E16.38.3", {"start": v(-102.32, -37.86) * mm, "mid": v(-101.98, -38.03) * mm, "end": v(-101.76, -38.35) * mm});
            skLineSegment(sketch, "E16.38.4", {"start": v(-103.81, -37.52) * mm, "end": v(-102.32, -37.86) * mm});
            skArc(sketch, "E16.38.5", {"start": v(-103.81, -37.52) * mm, "mid": v(-104.52, -37.15) * mm, "end": v(-104.96, -36.5) * mm});
            skArc(sketch, "E16.39.0", {"start": v(-100.54, -45.57) * mm, "mid": v(-100.8, -46.33) * mm, "end": v(-100.65, -47.1) * mm});
            skLineSegment(sketch, "E16.39.1", {"start": v(-100.54, -45.57) * mm, "end": v(-99.7, -44.29) * mm});
            skArc(sketch, "E16.39.2", {"start": v(-99.7, -44.29) * mm, "mid": v(-99.58, -43.92) * mm, "end": v(-99.65, -43.54) * mm});
            skArc(sketch, "E16.39.3", {"start": v(-100.24, -43.07) * mm, "mid": v(-99.88, -43.23) * mm, "end": v(-99.65, -43.54) * mm});
            skLineSegment(sketch, "E16.39.4", {"start": v(-101.74, -42.81) * mm, "end": v(-100.24, -43.07) * mm});
            skArc(sketch, "E16.39.5", {"start": v(-101.74, -42.81) * mm, "mid": v(-102.47, -42.49) * mm, "end": v(-102.94, -41.85) * mm});
            skArc(sketch, "E16.40.0", {"start": v(-98.06, -50.69) * mm, "mid": v(-98.27, -51.45) * mm, "end": v(-98.09, -52.23) * mm});
            skLineSegment(sketch, "E16.40.1", {"start": v(-98.06, -50.69) * mm, "end": v(-97.3, -49.36) * mm});
            skArc(sketch, "E16.40.2", {"start": v(-97.3, -49.36) * mm, "mid": v(-97.2, -48.99) * mm, "end": v(-97.27, -48.61) * mm});
            skArc(sketch, "E16.40.3", {"start": v(-97.89, -48.18) * mm, "mid": v(-97.53, -48.32) * mm, "end": v(-97.27, -48.61) * mm});
            skLineSegment(sketch, "E16.40.4", {"start": v(-99.4, -48) * mm, "end": v(-97.89, -48.18) * mm});
            skArc(sketch, "E16.40.5", {"start": v(-99.4, -48) * mm, "mid": v(-100.15, -47.7) * mm, "end": v(-100.65, -47.1) * mm});
            skArc(sketch, "E16.41.0", {"start": v(-95.32, -55.67) * mm, "mid": v(-95.5, -56.44) * mm, "end": v(-95.27, -57.2) * mm});
            skLineSegment(sketch, "E16.41.1", {"start": v(-95.32, -55.67) * mm, "end": v(-94.63, -54.3) * mm});
            skArc(sketch, "E16.41.2", {"start": v(-94.63, -54.3) * mm, "mid": v(-94.54, -53.93) * mm, "end": v(-94.64, -53.55) * mm});
            skArc(sketch, "E16.41.3", {"start": v(-95.28, -53.15) * mm, "mid": v(-94.91, -53.27) * mm, "end": v(-94.64, -53.55) * mm});
            skLineSegment(sketch, "E16.41.4", {"start": v(-96.8, -53.05) * mm, "end": v(-95.28, -53.15) * mm});
            skArc(sketch, "E16.41.5", {"start": v(-96.8, -53.05) * mm, "mid": v(-97.56, -52.8) * mm, "end": v(-98.1, -52.21) * mm});
            skArc(sketch, "E16.42.0", {"start": v(-92.33, -60.5) * mm, "mid": v(-92.46, -61.28) * mm, "end": v(-92.2, -62.03) * mm});
            skLineSegment(sketch, "E16.42.1", {"start": v(-92.33, -60.5) * mm, "end": v(-91.7, -59.1) * mm});
            skArc(sketch, "E16.42.2", {"start": v(-91.7, -59.1) * mm, "mid": v(-91.64, -58.72) * mm, "end": v(-91.76, -58.35) * mm});
            skArc(sketch, "E16.42.3", {"start": v(-92.42, -57.99) * mm, "mid": v(-92.04, -58.09) * mm, "end": v(-91.76, -58.35) * mm});
            skLineSegment(sketch, "E16.42.4", {"start": v(-93.94, -57.96) * mm, "end": v(-92.42, -57.99) * mm});
            skArc(sketch, "E16.42.5", {"start": v(-93.94, -57.96) * mm, "mid": v(-94.71, -57.75) * mm, "end": v(-95.28, -57.2) * mm});
            skArc(sketch, "E16.43.0", {"start": v(-89.1, -65.17) * mm, "mid": v(-89.18, -65.96) * mm, "end": v(-88.88, -66.7) * mm});
            skLineSegment(sketch, "E16.43.1", {"start": v(-89.1, -65.17) * mm, "end": v(-88.54, -63.75) * mm});
            skArc(sketch, "E16.43.2", {"start": v(-88.54, -63.75) * mm, "mid": v(-88.5, -63.36) * mm, "end": v(-88.63, -63) * mm});
            skArc(sketch, "E16.43.3", {"start": v(-89.3, -62.67) * mm, "mid": v(-88.93, -62.75) * mm, "end": v(-88.63, -63) * mm});
            skLineSegment(sketch, "E16.43.4", {"start": v(-90.84, -62.72) * mm, "end": v(-89.3, -62.67) * mm});
            skArc(sketch, "E16.43.5", {"start": v(-90.84, -62.72) * mm, "mid": v(-91.61, -62.55) * mm, "end": v(-92.2, -62.02) * mm});
            skArc(sketch, "E16.44.0", {"start": v(-85.62, -69.67) * mm, "mid": v(-85.67, -70.47) * mm, "end": v(-85.33, -71.19) * mm});
            skLineSegment(sketch, "E16.44.1", {"start": v(-85.62, -69.67) * mm, "end": v(-85.14, -68.22) * mm});
            skArc(sketch, "E16.44.2", {"start": v(-85.14, -68.22) * mm, "mid": v(-85.11, -67.83) * mm, "end": v(-85.27, -67.48) * mm});
            skArc(sketch, "E16.44.3", {"start": v(-85.96, -67.18) * mm, "mid": v(-85.58, -67.24) * mm, "end": v(-85.27, -67.48) * mm});
            skLineSegment(sketch, "E16.44.4", {"start": v(-87.49, -67.31) * mm, "end": v(-85.96, -67.18) * mm});
            skArc(sketch, "E16.44.5", {"start": v(-87.49, -67.31) * mm, "mid": v(-88.27, -67.18) * mm, "end": v(-88.9, -66.68) * mm});
            skArc(sketch, "E16.45.0", {"start": v(-81.92, -73.99) * mm, "mid": v(-81.93, -74.78) * mm, "end": v(-81.55, -75.48) * mm});
            skLineSegment(sketch, "E16.45.1", {"start": v(-81.92, -73.99) * mm, "end": v(-81.52, -72.51) * mm});
            skArc(sketch, "E16.45.2", {"start": v(-81.52, -72.51) * mm, "mid": v(-81.5, -72.13) * mm, "end": v(-81.69, -71.78) * mm});
            skArc(sketch, "E16.45.3", {"start": v(-82.4, -71.52) * mm, "mid": v(-82, -71.56) * mm, "end": v(-81.69, -71.78) * mm});
            skLineSegment(sketch, "E16.45.4", {"start": v(-83.9, -71.73) * mm, "end": v(-82.4, -71.52) * mm});
            skArc(sketch, "E16.45.5", {"start": v(-83.9, -71.73) * mm, "mid": v(-84.7, -71.64) * mm, "end": v(-85.34, -71.17) * mm});
            skArc(sketch, "E16.46.0", {"start": v(-78, -78.1) * mm, "mid": v(-77.97, -78.9) * mm, "end": v(-77.56, -79.58) * mm});
            skLineSegment(sketch, "E16.46.1", {"start": v(-78, -78.1) * mm, "end": v(-77.68, -76.61) * mm});
            skArc(sketch, "E16.46.2", {"start": v(-77.68, -76.61) * mm, "mid": v(-77.69, -76.23) * mm, "end": v(-77.88, -75.9) * mm});
            skArc(sketch, "E16.46.3", {"start": v(-78.6, -75.67) * mm, "mid": v(-78.21, -75.69) * mm, "end": v(-77.88, -75.9) * mm});
            skLineSegment(sketch, "E16.46.4", {"start": v(-80.1, -75.95) * mm, "end": v(-78.6, -75.67) * mm});
            skArc(sketch, "E16.46.5", {"start": v(-80.1, -75.95) * mm, "mid": v(-80.9, -75.9) * mm, "end": v(-81.57, -75.47) * mm});
            skArc(sketch, "E16.47.0", {"start": v(-73.88, -82.02) * mm, "mid": v(-73.8, -82.81) * mm, "end": v(-73.36, -83.47) * mm});
            skLineSegment(sketch, "E16.47.1", {"start": v(-73.88, -82.02) * mm, "end": v(-73.63, -80.51) * mm});
            skArc(sketch, "E16.47.2", {"start": v(-73.63, -80.51) * mm, "mid": v(-73.66, -80.12) * mm, "end": v(-73.87, -79.8) * mm});
            skArc(sketch, "E16.47.3", {"start": v(-74.6, -79.61) * mm, "mid": v(-74.21, -79.61) * mm, "end": v(-73.87, -79.8) * mm});
            skLineSegment(sketch, "E16.47.4", {"start": v(-76.09, -79.98) * mm, "end": v(-74.6, -79.61) * mm});
            skArc(sketch, "E16.47.5", {"start": v(-76.09, -79.98) * mm, "mid": v(-76.88, -79.96) * mm, "end": v(-77.57, -79.57) * mm});
            skArc(sketch, "E16.48.0", {"start": v(-69.56, -85.71) * mm, "mid": v(-69.45, -86.5) * mm, "end": v(-68.97, -87.14) * mm});
            skLineSegment(sketch, "E16.48.1", {"start": v(-69.56, -85.71) * mm, "end": v(-69.39, -84.2) * mm});
            skArc(sketch, "E16.48.2", {"start": v(-69.39, -84.2) * mm, "mid": v(-69.44, -83.81) * mm, "end": v(-69.67, -83.5) * mm});
            skArc(sketch, "E16.48.3", {"start": v(-70.4, -83.35) * mm, "mid": v(-70.02, -83.33) * mm, "end": v(-69.67, -83.5) * mm});
            skLineSegment(sketch, "E16.48.4", {"start": v(-71.87, -83.79) * mm, "end": v(-70.4, -83.35) * mm});
            skArc(sketch, "E16.48.5", {"start": v(-71.87, -83.79) * mm, "mid": v(-72.66, -83.82) * mm, "end": v(-73.37, -83.46) * mm});
            skArc(sketch, "E16.49.0", {"start": v(-65.05, -89.18) * mm, "mid": v(-64.9, -89.96) * mm, "end": v(-64.39, -90.57) * mm});
            skLineSegment(sketch, "E16.49.1", {"start": v(-65.05, -89.18) * mm, "end": v(-64.96, -87.65) * mm});
            skArc(sketch, "E16.49.2", {"start": v(-64.96, -87.65) * mm, "mid": v(-65.03, -87.27) * mm, "end": v(-65.28, -86.97) * mm});
            skArc(sketch, "E16.49.3", {"start": v(-66.02, -86.86) * mm, "mid": v(-65.63, -86.82) * mm, "end": v(-65.28, -86.97) * mm});
            skLineSegment(sketch, "E16.49.4", {"start": v(-67.46, -87.37) * mm, "end": v(-66.02, -86.86) * mm});
            skArc(sketch, "E16.49.5", {"start": v(-67.46, -87.37) * mm, "mid": v(-68.25, -87.45) * mm, "end": v(-68.98, -87.12) * mm});
            skArc(sketch, "E16.50.0", {"start": v(-60.38, -92.41) * mm, "mid": v(-60.18, -93.18) * mm, "end": v(-59.64, -93.76) * mm});
            skLineSegment(sketch, "E16.50.1", {"start": v(-60.38, -92.41) * mm, "end": v(-60.36, -90.88) * mm});
            skArc(sketch, "E16.50.2", {"start": v(-60.36, -90.88) * mm, "mid": v(-60.45, -90.5) * mm, "end": v(-60.71, -90.22) * mm});
            skArc(sketch, "E16.50.3", {"start": v(-61.46, -90.14) * mm, "mid": v(-61.08, -90.09) * mm, "end": v(-60.71, -90.22) * mm});
            skLineSegment(sketch, "E16.50.4", {"start": v(-62.87, -90.73) * mm, "end": v(-61.46, -90.14) * mm});
            skArc(sketch, "E16.50.5", {"start": v(-62.87, -90.73) * mm, "mid": v(-63.66, -90.84) * mm, "end": v(-64.4, -90.56) * mm});
            skArc(sketch, "E16.51.0", {"start": v(-55.54, -95.4) * mm, "mid": v(-55.3, -96.16) * mm, "end": v(-54.73, -96.71) * mm});
            skLineSegment(sketch, "E16.51.1", {"start": v(-55.54, -95.4) * mm, "end": v(-55.6, -93.87) * mm});
            skArc(sketch, "E16.51.2", {"start": v(-55.6, -93.87) * mm, "mid": v(-55.71, -93.5) * mm, "end": v(-55.99, -93.22) * mm});
            skArc(sketch, "E16.51.3", {"start": v(-56.74, -93.19) * mm, "mid": v(-56.36, -93.11) * mm, "end": v(-55.99, -93.22) * mm});
            skLineSegment(sketch, "E16.51.4", {"start": v(-58.12, -93.85) * mm, "end": v(-56.74, -93.19) * mm});
            skArc(sketch, "E16.51.5", {"start": v(-58.12, -93.85) * mm, "mid": v(-58.9, -94) * mm, "end": v(-59.66, -93.75) * mm});
            skArc(sketch, "E16.52.0", {"start": v(-50.55, -98.13) * mm, "mid": v(-50.28, -98.88) * mm, "end": v(-49.68, -99.4) * mm});
            skLineSegment(sketch, "E16.52.1", {"start": v(-50.55, -98.13) * mm, "end": v(-50.7, -96.6) * mm});
            skArc(sketch, "E16.52.2", {"start": v(-50.7, -96.6) * mm, "mid": v(-50.83, -96.24) * mm, "end": v(-51.11, -95.98) * mm});
            skArc(sketch, "E16.52.3", {"start": v(-51.87, -95.98) * mm, "mid": v(-51.5, -95.89) * mm, "end": v(-51.11, -95.98) * mm});
            skLineSegment(sketch, "E16.52.4", {"start": v(-53.2, -96.71) * mm, "end": v(-51.87, -95.98) * mm});
            skArc(sketch, "E16.52.5", {"start": v(-53.2, -96.71) * mm, "mid": v(-53.98, -96.9) * mm, "end": v(-54.75, -96.7) * mm});
            skArc(sketch, "E16.53.0", {"start": v(-45.44, -100.6) * mm, "mid": v(-45.13, -101.33) * mm, "end": v(-44.5, -101.83) * mm});
            skLineSegment(sketch, "E16.53.1", {"start": v(-45.44, -100.6) * mm, "end": v(-45.66, -99.09) * mm});
            skArc(sketch, "E16.53.2", {"start": v(-45.66, -99.09) * mm, "mid": v(-45.8, -98.73) * mm, "end": v(-46.1, -98.49) * mm});
            skArc(sketch, "E16.53.3", {"start": v(-46.86, -98.53) * mm, "mid": v(-46.49, -98.41) * mm, "end": v(-46.1, -98.49) * mm});
            skLineSegment(sketch, "E16.53.4", {"start": v(-48.16, -99.33) * mm, "end": v(-46.86, -98.53) * mm});
            skArc(sketch, "E16.53.5", {"start": v(-48.16, -99.33) * mm, "mid": v(-48.92, -99.56) * mm, "end": v(-49.7, -99.4) * mm});
            skArc(sketch, "E16.54.0", {"start": v(-40.2, -102.8) * mm, "mid": v(-39.85, -103.52) * mm, "end": v(-39.2, -103.98) * mm});
            skLineSegment(sketch, "E16.54.1", {"start": v(-40.2, -102.8) * mm, "end": v(-40.5, -101.3) * mm});
            skArc(sketch, "E16.54.2", {"start": v(-40.5, -101.3) * mm, "mid": v(-40.66, -100.96) * mm, "end": v(-40.97, -100.73) * mm});
            skArc(sketch, "E16.54.3", {"start": v(-41.72, -100.8) * mm, "mid": v(-41.36, -100.67) * mm, "end": v(-40.97, -100.73) * mm});
            skLineSegment(sketch, "E16.54.4", {"start": v(-42.98, -101.67) * mm, "end": v(-41.72, -100.8) * mm});
            skArc(sketch, "E16.54.5", {"start": v(-42.98, -101.67) * mm, "mid": v(-43.73, -101.94) * mm, "end": v(-44.52, -101.82) * mm});
            skArc(sketch, "E16.55.0", {"start": v(-34.85, -104.74) * mm, "mid": v(-34.47, -105.44) * mm, "end": v(-33.8, -105.86) * mm});
            skLineSegment(sketch, "E16.55.1", {"start": v(-34.85, -104.74) * mm, "end": v(-35.23, -103.26) * mm});
            skArc(sketch, "E16.55.2", {"start": v(-35.23, -103.26) * mm, "mid": v(-35.41, -102.92) * mm, "end": v(-35.74, -102.7) * mm});
            skArc(sketch, "E16.55.3", {"start": v(-36.48, -102.82) * mm, "mid": v(-36.12, -102.67) * mm, "end": v(-35.74, -102.7) * mm});
            skLineSegment(sketch, "E16.55.4", {"start": v(-37.7, -103.75) * mm, "end": v(-36.48, -102.82) * mm});
            skArc(sketch, "E16.55.5", {"start": v(-37.7, -103.75) * mm, "mid": v(-38.43, -104.06) * mm, "end": v(-39.22, -103.98) * mm});
            skArc(sketch, "E16.56.0", {"start": v(-29.41, -106.4) * mm, "mid": v(-29, -107.07) * mm, "end": v(-28.3, -107.46) * mm});
            skLineSegment(sketch, "E16.56.1", {"start": v(-29.41, -106.4) * mm, "end": v(-29.86, -104.94) * mm});
            skArc(sketch, "E16.56.2", {"start": v(-29.86, -104.94) * mm, "mid": v(-30.07, -104.6) * mm, "end": v(-30.4, -104.4) * mm});
            skArc(sketch, "E16.56.3", {"start": v(-31.14, -104.56) * mm, "mid": v(-30.79, -104.4) * mm, "end": v(-30.4, -104.4) * mm});
            skLineSegment(sketch, "E16.56.4", {"start": v(-32.3, -105.55) * mm, "end": v(-31.14, -104.56) * mm});
            skArc(sketch, "E16.56.5", {"start": v(-32.3, -105.55) * mm, "mid": v(-33.02, -105.9) * mm, "end": v(-33.81, -105.86) * mm});
            skArc(sketch, "E16.57.0", {"start": v(-23.9, -107.77) * mm, "mid": v(-23.44, -108.42) * mm, "end": v(-22.73, -108.78) * mm});
            skLineSegment(sketch, "E16.57.1", {"start": v(-23.9, -107.77) * mm, "end": v(-24.42, -106.33) * mm});
            skArc(sketch, "E16.57.2", {"start": v(-24.42, -106.33) * mm, "mid": v(-24.64, -106.01) * mm, "end": v(-24.99, -105.83) * mm});
            skArc(sketch, "E16.57.3", {"start": v(-25.71, -106.03) * mm, "mid": v(-25.37, -105.84) * mm, "end": v(-24.99, -105.83) * mm});
            skLineSegment(sketch, "E16.57.4", {"start": v(-26.82, -107.08) * mm, "end": v(-25.71, -106.03) * mm});
            skArc(sketch, "E16.57.5", {"start": v(-26.82, -107.08) * mm, "mid": v(-27.52, -107.46) * mm, "end": v(-28.32, -107.46) * mm});
            skArc(sketch, "E16.58.0", {"start": v(-18.32, -108.86) * mm, "mid": v(-17.83, -109.49) * mm, "end": v(-17.1, -109.8) * mm});
            skLineSegment(sketch, "E16.58.1", {"start": v(-18.32, -108.86) * mm, "end": v(-18.92, -107.45) * mm});
            skArc(sketch, "E16.58.2", {"start": v(-18.92, -107.45) * mm, "mid": v(-19.15, -107.14) * mm, "end": v(-19.5, -106.98) * mm});
            skArc(sketch, "E16.58.3", {"start": v(-20.22, -107.21) * mm, "mid": v(-19.9, -107) * mm, "end": v(-19.5, -106.98) * mm});
            skLineSegment(sketch, "E16.58.4", {"start": v(-21.28, -108.32) * mm, "end": v(-20.22, -107.21) * mm});
            skArc(sketch, "E16.58.5", {"start": v(-21.28, -108.32) * mm, "mid": v(-21.95, -108.73) * mm, "end": v(-22.75, -108.77) * mm});
            skArc(sketch, "E16.59.0", {"start": v(-12.69, -109.65) * mm, "mid": v(-12.17, -110.26) * mm, "end": v(-11.43, -110.54) * mm});
            skLineSegment(sketch, "E16.59.1", {"start": v(-12.69, -109.65) * mm, "end": v(-13.36, -108.28) * mm});
            skArc(sketch, "E16.59.2", {"start": v(-13.36, -108.28) * mm, "mid": v(-13.61, -107.98) * mm, "end": v(-13.97, -107.84) * mm});
            skArc(sketch, "E16.59.3", {"start": v(-14.67, -108.11) * mm, "mid": v(-14.36, -107.89) * mm, "end": v(-13.97, -107.84) * mm});
            skLineSegment(sketch, "E16.59.4", {"start": v(-15.67, -109.27) * mm, "end": v(-14.67, -108.11) * mm});
            skArc(sketch, "E16.59.5", {"start": v(-15.67, -109.27) * mm, "mid": v(-16.33, -109.72) * mm, "end": v(-17.12, -109.8) * mm});
            skArc(sketch, "E16.60.0", {"start": v(-7.03, -110.16) * mm, "mid": v(-6.48, -110.74) * mm, "end": v(-5.72, -110.98) * mm});
            skLineSegment(sketch, "E16.60.1", {"start": v(-7.03, -110.16) * mm, "end": v(-7.77, -108.83) * mm});
            skArc(sketch, "E16.60.2", {"start": v(-7.77, -108.83) * mm, "mid": v(-8.03, -108.54) * mm, "end": v(-8.4, -108.42) * mm});
            skArc(sketch, "E16.60.3", {"start": v(-9.09, -108.72) * mm, "mid": v(-8.78, -108.48) * mm, "end": v(-8.4, -108.42) * mm});
            skLineSegment(sketch, "E16.60.4", {"start": v(-10.03, -109.93) * mm, "end": v(-9.09, -108.72) * mm});
            skArc(sketch, "E16.60.5", {"start": v(-10.03, -109.93) * mm, "mid": v(-10.66, -110.42) * mm, "end": v(-11.44, -110.53) * mm});
            skArc(sketch, "E16.61.0", {"start": v(-1.35, -110.38) * mm, "mid": v(-0.77, -110.93) * mm, "end": v(0, -111.13) * mm});
            skLineSegment(sketch, "E16.61.1", {"start": v(-1.35, -110.38) * mm, "end": v(-2.16, -109.08) * mm});
            skArc(sketch, "E16.61.2", {"start": v(-2.16, -109.08) * mm, "mid": v(-2.44, -108.81) * mm, "end": v(-2.8, -108.7) * mm});
            skArc(sketch, "E16.61.3", {"start": v(-3.48, -109.05) * mm, "mid": v(-3.19, -108.8) * mm, "end": v(-2.8, -108.7) * mm});
            skLineSegment(sketch, "E16.61.4", {"start": v(-4.35, -110.3) * mm, "end": v(-3.48, -109.05) * mm});
            skArc(sketch, "E16.61.5", {"start": v(-4.35, -110.3) * mm, "mid": v(-4.96, -110.82) * mm, "end": v(-5.74, -110.98) * mm});
            skArc(sketch, "E16.62.0", {"start": v(4.34, -110.3) * mm, "mid": v(4.94, -110.82) * mm, "end": v(5.72, -110.98) * mm});
            skLineSegment(sketch, "E16.62.1", {"start": v(4.34, -110.3) * mm, "end": v(3.46, -109.05) * mm});
            skArc(sketch, "E16.62.2", {"start": v(3.46, -109.05) * mm, "mid": v(3.17, -108.8) * mm, "end": v(2.8, -108.7) * mm});
            skArc(sketch, "E16.62.3", {"start": v(2.14, -109.08) * mm, "mid": v(2.42, -108.81) * mm, "end": v(2.8, -108.7) * mm});
            skLineSegment(sketch, "E16.62.4", {"start": v(1.33, -110.38) * mm, "end": v(2.14, -109.08) * mm});
            skArc(sketch, "E16.62.5", {"start": v(1.33, -110.38) * mm, "mid": v(0.75, -110.93) * mm, "end": v(-0.02, -111.12) * mm});
            skArc(sketch, "E16.63.0", {"start": v(10, -109.93) * mm, "mid": v(10.64, -110.42) * mm, "end": v(11.43, -110.54) * mm});
            skLineSegment(sketch, "E16.63.1", {"start": v(10, -109.93) * mm, "end": v(9.07, -108.72) * mm});
            skArc(sketch, "E16.63.2", {"start": v(9.07, -108.72) * mm, "mid": v(8.77, -108.49) * mm, "end": v(8.38, -108.42) * mm});
            skArc(sketch, "E16.63.3", {"start": v(7.75, -108.83) * mm, "mid": v(8.02, -108.54) * mm, "end": v(8.38, -108.42) * mm});
            skLineSegment(sketch, "E16.63.4", {"start": v(7, -110.16) * mm, "end": v(7.75, -108.83) * mm});
            skArc(sketch, "E16.63.5", {"start": v(7, -110.16) * mm, "mid": v(6.46, -110.74) * mm, "end": v(5.7, -110.98) * mm});
            skArc(sketch, "E16.64.0", {"start": v(15.66, -109.27) * mm, "mid": v(16.3, -109.72) * mm, "end": v(17.1, -109.8) * mm});
            skLineSegment(sketch, "E16.64.1", {"start": v(15.66, -109.27) * mm, "end": v(14.66, -108.11) * mm});
            skArc(sketch, "E16.64.2", {"start": v(14.66, -108.11) * mm, "mid": v(14.34, -107.9) * mm, "end": v(13.95, -107.84) * mm});
            skArc(sketch, "E16.64.3", {"start": v(13.34, -108.28) * mm, "mid": v(13.6, -107.99) * mm, "end": v(13.95, -107.84) * mm});
            skLineSegment(sketch, "E16.64.4", {"start": v(12.67, -109.66) * mm, "end": v(13.34, -108.28) * mm});
            skArc(sketch, "E16.64.5", {"start": v(12.67, -109.66) * mm, "mid": v(12.15, -110.26) * mm, "end": v(11.4, -110.54) * mm});
            skArc(sketch, "E16.65.0", {"start": v(21.26, -108.32) * mm, "mid": v(21.94, -108.74) * mm, "end": v(22.73, -108.78) * mm});
            skLineSegment(sketch, "E16.65.1", {"start": v(21.26, -108.32) * mm, "end": v(20.2, -107.22) * mm});
            skArc(sketch, "E16.65.2", {"start": v(20.2, -107.22) * mm, "mid": v(19.87, -107) * mm, "end": v(19.49, -106.98) * mm});
            skArc(sketch, "E16.65.3", {"start": v(18.9, -107.45) * mm, "mid": v(19.13, -107.14) * mm, "end": v(19.49, -106.98) * mm});
            skLineSegment(sketch, "E16.65.4", {"start": v(18.3, -108.86) * mm, "end": v(18.9, -107.45) * mm});
            skArc(sketch, "E16.65.5", {"start": v(18.3, -108.86) * mm, "mid": v(17.81, -109.49) * mm, "end": v(17.08, -109.8) * mm});
            skArc(sketch, "E16.66.0", {"start": v(26.8, -107.08) * mm, "mid": v(27.5, -107.46) * mm, "end": v(28.3, -107.46) * mm});
            skLineSegment(sketch, "E16.66.1", {"start": v(26.8, -107.08) * mm, "end": v(25.7, -106.03) * mm});
            skArc(sketch, "E16.66.2", {"start": v(25.7, -106.03) * mm, "mid": v(25.36, -105.84) * mm, "end": v(24.97, -105.84) * mm});
            skArc(sketch, "E16.66.3", {"start": v(24.4, -106.34) * mm, "mid": v(24.62, -106.02) * mm, "end": v(24.97, -105.84) * mm});
            skLineSegment(sketch, "E16.66.4", {"start": v(23.88, -107.77) * mm, "end": v(24.4, -106.34) * mm});
            skArc(sketch, "E16.66.5", {"start": v(23.88, -107.77) * mm, "mid": v(23.43, -108.43) * mm, "end": v(22.71, -108.78) * mm});
            skArc(sketch, "E16.67.0", {"start": v(32.28, -105.56) * mm, "mid": v(33, -105.9) * mm, "end": v(33.8, -105.86) * mm});
            skLineSegment(sketch, "E16.67.1", {"start": v(32.28, -105.56) * mm, "end": v(31.12, -104.57) * mm});
            skArc(sketch, "E16.67.2", {"start": v(31.12, -104.57) * mm, "mid": v(30.77, -104.4) * mm, "end": v(30.38, -104.41) * mm});
            skArc(sketch, "E16.67.3", {"start": v(29.85, -104.94) * mm, "mid": v(30.05, -104.6) * mm, "end": v(30.38, -104.41) * mm});
            skLineSegment(sketch, "E16.67.4", {"start": v(29.4, -106.4) * mm, "end": v(29.85, -104.94) * mm});
            skArc(sketch, "E16.67.5", {"start": v(29.4, -106.4) * mm, "mid": v(28.98, -107.08) * mm, "end": v(28.28, -107.47) * mm});
            skArc(sketch, "E16.68.0", {"start": v(37.68, -103.76) * mm, "mid": v(38.4, -104.07) * mm, "end": v(39.2, -103.98) * mm});
            skLineSegment(sketch, "E16.68.1", {"start": v(37.68, -103.76) * mm, "end": v(36.46, -102.83) * mm});
            skArc(sketch, "E16.68.2", {"start": v(36.46, -102.83) * mm, "mid": v(36.1, -102.68) * mm, "end": v(35.72, -102.71) * mm});
            skArc(sketch, "E16.68.3", {"start": v(35.21, -103.26) * mm, "mid": v(35.4, -102.92) * mm, "end": v(35.72, -102.71) * mm});
            skLineSegment(sketch, "E16.68.4", {"start": v(34.83, -104.75) * mm, "end": v(35.21, -103.26) * mm});
            skArc(sketch, "E16.68.5", {"start": v(34.83, -104.75) * mm, "mid": v(34.45, -105.44) * mm, "end": v(33.78, -105.87) * mm});
            skArc(sketch, "E16.69.0", {"start": v(42.97, -101.68) * mm, "mid": v(43.71, -101.95) * mm, "end": v(44.5, -101.83) * mm});
            skLineSegment(sketch, "E16.69.1", {"start": v(42.97, -101.68) * mm, "end": v(41.7, -100.82) * mm});
            skArc(sketch, "E16.69.2", {"start": v(41.7, -100.82) * mm, "mid": v(41.34, -100.68) * mm, "end": v(40.96, -100.74) * mm});
            skArc(sketch, "E16.69.3", {"start": v(40.48, -101.31) * mm, "mid": v(40.65, -100.96) * mm, "end": v(40.96, -100.74) * mm});
            skLineSegment(sketch, "E16.69.4", {"start": v(40.18, -102.81) * mm, "end": v(40.48, -101.31) * mm});
            skArc(sketch, "E16.69.5", {"start": v(40.18, -102.81) * mm, "mid": v(39.83, -103.53) * mm, "end": v(39.18, -103.99) * mm});
            skArc(sketch, "E16.70.0", {"start": v(48.14, -99.33) * mm, "mid": v(48.9, -99.57) * mm, "end": v(49.68, -99.4) * mm});
            skLineSegment(sketch, "E16.70.1", {"start": v(48.14, -99.33) * mm, "end": v(46.84, -98.54) * mm});
            skArc(sketch, "E16.70.2", {"start": v(46.84, -98.54) * mm, "mid": v(46.47, -98.42) * mm, "end": v(46.1, -98.5) * mm});
            skArc(sketch, "E16.70.3", {"start": v(45.64, -99.1) * mm, "mid": v(45.79, -98.74) * mm, "end": v(46.1, -98.5) * mm});
            skLineSegment(sketch, "E16.70.4", {"start": v(45.42, -100.6) * mm, "end": v(45.64, -99.1) * mm});
            skArc(sketch, "E16.70.5", {"start": v(45.42, -100.6) * mm, "mid": v(45.11, -101.34) * mm, "end": v(44.48, -101.83) * mm});
            skArc(sketch, "E16.71.0", {"start": v(53.2, -96.72) * mm, "mid": v(53.97, -96.92) * mm, "end": v(54.73, -96.71) * mm});
            skLineSegment(sketch, "E16.71.1", {"start": v(53.2, -96.72) * mm, "end": v(51.85, -96) * mm});
            skArc(sketch, "E16.71.2", {"start": v(51.85, -96) * mm, "mid": v(51.48, -95.9) * mm, "end": v(51.1, -95.99) * mm});
            skArc(sketch, "E16.71.3", {"start": v(50.68, -96.62) * mm, "mid": v(50.81, -96.25) * mm, "end": v(51.1, -95.99) * mm});
            skLineSegment(sketch, "E16.71.4", {"start": v(50.54, -98.14) * mm, "end": v(50.68, -96.62) * mm});
            skArc(sketch, "E16.71.5", {"start": v(50.54, -98.14) * mm, "mid": v(50.27, -98.89) * mm, "end": v(49.67, -99.4) * mm});
            skArc(sketch, "E16.72.0", {"start": v(58.1, -93.86) * mm, "mid": v(58.88, -94) * mm, "end": v(59.64, -93.76) * mm});
            skLineSegment(sketch, "E16.72.1", {"start": v(58.1, -93.86) * mm, "end": v(56.72, -93.2) * mm});
            skArc(sketch, "E16.72.2", {"start": v(56.72, -93.2) * mm, "mid": v(56.34, -93.12) * mm, "end": v(55.97, -93.23) * mm});
            skArc(sketch, "E16.72.3", {"start": v(55.59, -93.88) * mm, "mid": v(55.7, -93.5) * mm, "end": v(55.97, -93.23) * mm});
            skLineSegment(sketch, "E16.72.4", {"start": v(55.52, -95.4) * mm, "end": v(55.59, -93.88) * mm});
            skArc(sketch, "E16.72.5", {"start": v(55.52, -95.4) * mm, "mid": v(55.3, -96.17) * mm, "end": v(54.72, -96.72) * mm});
            skArc(sketch, "E16.73.0", {"start": v(62.86, -90.74) * mm, "mid": v(63.64, -90.85) * mm, "end": v(64.39, -90.57) * mm});
            skLineSegment(sketch, "E16.73.1", {"start": v(62.86, -90.74) * mm, "end": v(61.45, -90.15) * mm});
            skArc(sketch, "E16.73.2", {"start": v(61.45, -90.15) * mm, "mid": v(61.06, -90.1) * mm, "end": v(60.7, -90.23) * mm});
            skArc(sketch, "E16.73.3", {"start": v(60.35, -90.9) * mm, "mid": v(60.44, -90.52) * mm, "end": v(60.7, -90.23) * mm});
            skLineSegment(sketch, "E16.73.4", {"start": v(60.36, -92.42) * mm, "end": v(60.35, -90.9) * mm});
            skArc(sketch, "E16.73.5", {"start": v(60.36, -92.42) * mm, "mid": v(60.17, -93.2) * mm, "end": v(59.63, -93.77) * mm});
            skArc(sketch, "E16.74.0", {"start": v(67.45, -87.39) * mm, "mid": v(68.24, -87.46) * mm, "end": v(68.97, -87.14) * mm});
            skLineSegment(sketch, "E16.74.1", {"start": v(67.45, -87.39) * mm, "end": v(66, -86.87) * mm});
            skArc(sketch, "E16.74.2", {"start": v(66, -86.87) * mm, "mid": v(65.62, -86.83) * mm, "end": v(65.26, -86.98) * mm});
            skArc(sketch, "E16.74.3", {"start": v(64.95, -87.67) * mm, "mid": v(65.02, -87.28) * mm, "end": v(65.26, -86.98) * mm});
            skLineSegment(sketch, "E16.74.4", {"start": v(65.04, -89.2) * mm, "end": v(64.95, -87.67) * mm});
            skArc(sketch, "E16.74.5", {"start": v(65.04, -89.2) * mm, "mid": v(64.89, -89.97) * mm, "end": v(64.37, -90.58) * mm});
            skArc(sketch, "E16.75.0", {"start": v(71.85, -83.8) * mm, "mid": v(72.65, -83.83) * mm, "end": v(73.36, -83.47) * mm});
            skLineSegment(sketch, "E16.75.1", {"start": v(71.85, -83.8) * mm, "end": v(70.4, -83.36) * mm});
            skArc(sketch, "E16.75.2", {"start": v(70.4, -83.36) * mm, "mid": v(70, -83.34) * mm, "end": v(69.65, -83.5) * mm});
            skArc(sketch, "E16.75.3", {"start": v(69.37, -84.2) * mm, "mid": v(69.43, -83.82) * mm, "end": v(69.65, -83.5) * mm});
            skLineSegment(sketch, "E16.75.4", {"start": v(69.54, -85.72) * mm, "end": v(69.37, -84.2) * mm});
            skArc(sketch, "E16.75.5", {"start": v(69.54, -85.72) * mm, "mid": v(69.43, -86.51) * mm, "end": v(68.95, -87.15) * mm});
            skArc(sketch, "E16.76.0", {"start": v(76.07, -79.99) * mm, "mid": v(76.87, -79.98) * mm, "end": v(77.56, -79.58) * mm});
            skLineSegment(sketch, "E16.76.1", {"start": v(76.07, -79.99) * mm, "end": v(74.59, -79.62) * mm});
            skArc(sketch, "E16.76.2", {"start": v(74.59, -79.62) * mm, "mid": v(74.2, -79.63) * mm, "end": v(73.86, -79.81) * mm});
            skArc(sketch, "E16.76.3", {"start": v(73.62, -80.52) * mm, "mid": v(73.65, -80.14) * mm, "end": v(73.86, -79.81) * mm});
            skLineSegment(sketch, "E16.76.4", {"start": v(73.86, -82.03) * mm, "end": v(73.62, -80.52) * mm});
            skArc(sketch, "E16.76.5", {"start": v(73.86, -82.03) * mm, "mid": v(73.8, -82.82) * mm, "end": v(73.35, -83.48) * mm});
            skArc(sketch, "E16.77.0", {"start": v(80.09, -75.97) * mm, "mid": v(80.88, -75.91) * mm, "end": v(81.55, -75.48) * mm});
            skLineSegment(sketch, "E16.77.1", {"start": v(80.09, -75.97) * mm, "end": v(78.59, -75.68) * mm});
            skArc(sketch, "E16.77.2", {"start": v(78.59, -75.68) * mm, "mid": v(78.2, -75.7) * mm, "end": v(77.87, -75.9) * mm});
            skArc(sketch, "E16.77.3", {"start": v(77.66, -76.63) * mm, "mid": v(77.68, -76.24) * mm, "end": v(77.87, -75.9) * mm});
            skLineSegment(sketch, "E16.77.4", {"start": v(77.99, -78.12) * mm, "end": v(77.66, -76.63) * mm});
            skArc(sketch, "E16.77.5", {"start": v(77.99, -78.12) * mm, "mid": v(77.96, -78.91) * mm, "end": v(77.55, -79.6) * mm});
            skArc(sketch, "E16.78.0", {"start": v(83.9, -71.74) * mm, "mid": v(84.68, -71.65) * mm, "end": v(85.33, -71.19) * mm});
            skLineSegment(sketch, "E16.78.1", {"start": v(83.9, -71.74) * mm, "end": v(82.38, -71.53) * mm});
            skArc(sketch, "E16.78.2", {"start": v(82.38, -71.53) * mm, "mid": v(82, -71.57) * mm, "end": v(81.68, -71.8) * mm});
            skArc(sketch, "E16.78.3", {"start": v(81.5, -72.53) * mm, "mid": v(81.5, -72.14) * mm, "end": v(81.68, -71.8) * mm});
            skLineSegment(sketch, "E16.78.4", {"start": v(81.9, -74) * mm, "end": v(81.5, -72.53) * mm});
            skArc(sketch, "E16.78.5", {"start": v(81.9, -74) * mm, "mid": v(81.92, -74.8) * mm, "end": v(81.54, -75.5) * mm});
            skArc(sketch, "E16.79.0", {"start": v(87.48, -67.33) * mm, "mid": v(88.26, -67.2) * mm, "end": v(88.88, -66.7) * mm});
            skLineSegment(sketch, "E16.79.1", {"start": v(87.48, -67.33) * mm, "end": v(85.95, -67.2) * mm});
            skArc(sketch, "E16.79.2", {"start": v(85.95, -67.2) * mm, "mid": v(85.57, -67.26) * mm, "end": v(85.26, -67.5) * mm});
            skArc(sketch, "E16.79.3", {"start": v(85.13, -68.23) * mm, "mid": v(85.1, -67.85) * mm, "end": v(85.26, -67.5) * mm});
            skLineSegment(sketch, "E16.79.4", {"start": v(85.6, -69.69) * mm, "end": v(85.13, -68.23) * mm});
            skArc(sketch, "E16.79.5", {"start": v(85.6, -69.69) * mm, "mid": v(85.66, -70.48) * mm, "end": v(85.32, -71.2) * mm});
            skArc(sketch, "E16.80.0", {"start": v(90.83, -62.74) * mm, "mid": v(91.6, -62.56) * mm, "end": v(92.2, -62.03) * mm});
            skLineSegment(sketch, "E16.80.1", {"start": v(90.83, -62.74) * mm, "end": v(89.3, -62.68) * mm});
            skArc(sketch, "E16.80.2", {"start": v(89.3, -62.68) * mm, "mid": v(88.92, -62.76) * mm, "end": v(88.62, -63.02) * mm});
            skArc(sketch, "E16.80.3", {"start": v(88.53, -63.76) * mm, "mid": v(88.48, -63.38) * mm, "end": v(88.62, -63.02) * mm});
            skLineSegment(sketch, "E16.80.4", {"start": v(89.08, -65.19) * mm, "end": v(88.53, -63.76) * mm});
            skArc(sketch, "E16.80.5", {"start": v(89.08, -65.19) * mm, "mid": v(89.17, -65.98) * mm, "end": v(88.87, -66.71) * mm});
            skArc(sketch, "E16.81.0", {"start": v(93.93, -57.98) * mm, "mid": v(94.7, -57.76) * mm, "end": v(95.27, -57.2) * mm});
            skLineSegment(sketch, "E16.81.1", {"start": v(93.93, -57.98) * mm, "end": v(92.4, -58) * mm});
            skArc(sketch, "E16.81.2", {"start": v(92.4, -58) * mm, "mid": v(92.03, -58.1) * mm, "end": v(91.75, -58.37) * mm});
            skArc(sketch, "E16.81.3", {"start": v(91.7, -59.12) * mm, "mid": v(91.63, -58.74) * mm, "end": v(91.75, -58.37) * mm});
            skLineSegment(sketch, "E16.81.4", {"start": v(92.32, -60.51) * mm, "end": v(91.7, -59.12) * mm});
            skArc(sketch, "E16.81.5", {"start": v(92.32, -60.51) * mm, "mid": v(92.45, -61.3) * mm, "end": v(92.19, -62.05) * mm});
            skArc(sketch, "E16.82.0", {"start": v(96.8, -53.06) * mm, "mid": v(97.55, -52.81) * mm, "end": v(98.09, -52.23) * mm});
            skLineSegment(sketch, "E16.82.1", {"start": v(96.8, -53.06) * mm, "end": v(95.27, -53.17) * mm});
            skArc(sketch, "E16.82.2", {"start": v(95.27, -53.17) * mm, "mid": v(94.9, -53.29) * mm, "end": v(94.63, -53.57) * mm});
            skArc(sketch, "E16.82.3", {"start": v(94.62, -54.32) * mm, "mid": v(94.53, -53.94) * mm, "end": v(94.63, -53.57) * mm});
            skLineSegment(sketch, "E16.82.4", {"start": v(95.31, -55.68) * mm, "end": v(94.62, -54.32) * mm});
            skArc(sketch, "E16.82.5", {"start": v(95.31, -55.68) * mm, "mid": v(95.49, -56.46) * mm, "end": v(95.26, -57.22) * mm});
            skArc(sketch, "E16.83.0", {"start": v(99.4, -48.01) * mm, "mid": v(100.14, -47.72) * mm, "end": v(100.65, -47.1) * mm});
            skLineSegment(sketch, "E16.83.1", {"start": v(99.4, -48.01) * mm, "end": v(97.88, -48.2) * mm});
            skArc(sketch, "E16.83.2", {"start": v(97.88, -48.2) * mm, "mid": v(97.52, -48.33) * mm, "end": v(97.27, -48.63) * mm});
            skArc(sketch, "E16.83.3", {"start": v(97.29, -49.38) * mm, "mid": v(97.18, -49) * mm, "end": v(97.27, -48.63) * mm});
            skLineSegment(sketch, "E16.83.4", {"start": v(98.05, -50.7) * mm, "end": v(97.29, -49.38) * mm});
            skArc(sketch, "E16.83.5", {"start": v(98.05, -50.7) * mm, "mid": v(98.27, -51.47) * mm, "end": v(98.08, -52.24) * mm});
            skArc(sketch, "E16.84.0", {"start": v(101.74, -42.83) * mm, "mid": v(102.46, -42.5) * mm, "end": v(102.94, -41.86) * mm});
            skLineSegment(sketch, "E16.84.1", {"start": v(101.74, -42.83) * mm, "end": v(100.23, -43.1) * mm});
            skArc(sketch, "E16.84.2", {"start": v(100.23, -43.1) * mm, "mid": v(99.88, -43.25) * mm, "end": v(99.64, -43.55) * mm});
            skArc(sketch, "E16.84.3", {"start": v(99.7, -44.3) * mm, "mid": v(99.58, -43.94) * mm, "end": v(99.64, -43.55) * mm});
            skLineSegment(sketch, "E16.84.4", {"start": v(100.53, -45.59) * mm, "end": v(99.7, -44.3) * mm});
            skArc(sketch, "E16.84.5", {"start": v(100.53, -45.59) * mm, "mid": v(100.78, -46.34) * mm, "end": v(100.64, -47.12) * mm});
            skArc(sketch, "E16.85.0", {"start": v(103.8, -37.54) * mm, "mid": v(104.52, -37.17) * mm, "end": v(104.96, -36.5) * mm});
            skLineSegment(sketch, "E16.85.1", {"start": v(103.8, -37.54) * mm, "end": v(102.32, -37.87) * mm});
            skArc(sketch, "E16.85.2", {"start": v(102.32, -37.87) * mm, "mid": v(101.97, -38.05) * mm, "end": v(101.75, -38.37) * mm});
            skArc(sketch, "E16.85.3", {"start": v(101.85, -39.11) * mm, "mid": v(101.7, -38.75) * mm, "end": v(101.75, -38.37) * mm});
            skLineSegment(sketch, "E16.85.4", {"start": v(102.75, -40.35) * mm, "end": v(101.85, -39.11) * mm});
            skArc(sketch, "E16.85.5", {"start": v(102.75, -40.35) * mm, "mid": v(103.04, -41.1) * mm, "end": v(102.93, -41.88) * mm});
            skArc(sketch, "E16.86.0", {"start": v(105.6, -32.14) * mm, "mid": v(106.29, -31.74) * mm, "end": v(106.7, -31.06) * mm});
            skLineSegment(sketch, "E16.86.1", {"start": v(105.6, -32.14) * mm, "end": v(104.13, -32.56) * mm});
            skArc(sketch, "E16.86.2", {"start": v(104.13, -32.56) * mm, "mid": v(103.8, -32.75) * mm, "end": v(103.6, -33.08) * mm});
            skArc(sketch, "E16.86.3", {"start": v(103.73, -33.82) * mm, "mid": v(103.57, -33.47) * mm, "end": v(103.6, -33.08) * mm});
            skLineSegment(sketch, "E16.86.4", {"start": v(104.69, -35) * mm, "end": v(103.73, -33.82) * mm});
            skArc(sketch, "E16.86.5", {"start": v(104.69, -35) * mm, "mid": v(105.02, -35.73) * mm, "end": v(104.95, -36.53) * mm});
            skArc(sketch, "E16.87.0", {"start": v(107.12, -26.66) * mm, "mid": v(107.78, -26.23) * mm, "end": v(108.15, -25.52) * mm});
            skLineSegment(sketch, "E16.87.1", {"start": v(107.12, -26.66) * mm, "end": v(105.67, -27.15) * mm});
            skArc(sketch, "E16.87.2", {"start": v(105.67, -27.15) * mm, "mid": v(105.34, -27.36) * mm, "end": v(105.16, -27.7) * mm});
            skArc(sketch, "E16.87.3", {"start": v(105.33, -28.43) * mm, "mid": v(105.15, -28.1) * mm, "end": v(105.16, -27.7) * mm});
            skLineSegment(sketch, "E16.87.4", {"start": v(106.35, -29.57) * mm, "end": v(105.33, -28.43) * mm});
            skArc(sketch, "E16.87.5", {"start": v(106.35, -29.57) * mm, "mid": v(106.72, -30.28) * mm, "end": v(106.7, -31.08) * mm});
            skArc(sketch, "E16.88.0", {"start": v(108.35, -21.11) * mm, "mid": v(109, -20.64) * mm, "end": v(109.32, -19.92) * mm});
            skLineSegment(sketch, "E16.88.1", {"start": v(108.35, -21.11) * mm, "end": v(106.93, -21.68) * mm});
            skArc(sketch, "E16.88.2", {"start": v(106.93, -21.68) * mm, "mid": v(106.61, -21.9) * mm, "end": v(106.44, -22.25) * mm});
            skArc(sketch, "E16.88.3", {"start": v(106.66, -22.97) * mm, "mid": v(106.46, -22.64) * mm, "end": v(106.44, -22.25) * mm});
            skLineSegment(sketch, "E16.88.4", {"start": v(107.73, -24.06) * mm, "end": v(106.66, -22.97) * mm});
            skArc(sketch, "E16.88.5", {"start": v(107.73, -24.06) * mm, "mid": v(108.13, -24.75) * mm, "end": v(108.15, -25.54) * mm});
            skArc(sketch, "E16.89.0", {"start": v(109.3, -15.5) * mm, "mid": v(109.9, -15) * mm, "end": v(110.2, -14.27) * mm});
            skLineSegment(sketch, "E16.89.1", {"start": v(109.3, -15.5) * mm, "end": v(107.9, -16.14) * mm});
            skArc(sketch, "E16.89.2", {"start": v(107.9, -16.14) * mm, "mid": v(107.6, -16.39) * mm, "end": v(107.45, -16.74) * mm});
            skArc(sketch, "E16.89.3", {"start": v(107.7, -17.45) * mm, "mid": v(107.48, -17.13) * mm, "end": v(107.45, -16.74) * mm});
            skLineSegment(sketch, "E16.89.4", {"start": v(108.83, -18.48) * mm, "end": v(107.7, -17.45) * mm});
            skArc(sketch, "E16.89.5", {"start": v(108.83, -18.48) * mm, "mid": v(109.26, -19.15) * mm, "end": v(109.32, -19.94) * mm});
            skArc(sketch, "E16.90.0", {"start": v(109.94, -9.86) * mm, "mid": v(110.54, -9.33) * mm, "end": v(110.8, -8.58) * mm});
            skLineSegment(sketch, "E16.90.1", {"start": v(109.94, -9.86) * mm, "end": v(108.59, -10.57) * mm});
            skArc(sketch, "E16.90.2", {"start": v(108.59, -10.57) * mm, "mid": v(108.3, -10.83) * mm, "end": v(108.17, -11.19) * mm});
            skArc(sketch, "E16.90.3", {"start": v(108.45, -11.89) * mm, "mid": v(108.22, -11.57) * mm, "end": v(108.17, -11.19) * mm});
            skLineSegment(sketch, "E16.90.4", {"start": v(109.63, -12.85) * mm, "end": v(108.45, -11.89) * mm});
            skArc(sketch, "E16.90.5", {"start": v(109.63, -12.85) * mm, "mid": v(110.1, -13.5) * mm, "end": v(110.2, -14.29) * mm});
            skArc(sketch, "E16.91.0", {"start": v(110.3, -4.19) * mm, "mid": v(110.87, -3.63) * mm, "end": v(111.09, -2.86) * mm});
            skLineSegment(sketch, "E16.91.1", {"start": v(110.3, -4.19) * mm, "end": v(108.99, -4.96) * mm});
            skArc(sketch, "E16.91.2", {"start": v(108.99, -4.96) * mm, "mid": v(108.71, -5.24) * mm, "end": v(108.6, -5.6) * mm});
            skArc(sketch, "E16.91.3", {"start": v(108.92, -6.29) * mm, "mid": v(108.67, -5.99) * mm, "end": v(108.6, -5.6) * mm});
            skLineSegment(sketch, "E16.91.4", {"start": v(110.15, -7.2) * mm, "end": v(108.92, -6.29) * mm});
            skArc(sketch, "E16.91.5", {"start": v(110.15, -7.2) * mm, "mid": v(110.65, -7.81) * mm, "end": v(110.8, -8.6) * mm});
            skArc(sketch, "E16.92.0", {"start": v(110.38, 1.5) * mm, "mid": v(110.9, 2.09) * mm, "end": v(111.09, 2.86) * mm});
            skLineSegment(sketch, "E16.92.1", {"start": v(110.38, 1.5) * mm, "end": v(109.1, 0.65) * mm});
            skArc(sketch, "E16.92.2", {"start": v(109.1, 0.65) * mm, "mid": v(108.84, 0.37) * mm, "end": v(108.74, 0) * mm});
            skArc(sketch, "E16.92.3", {"start": v(109.1, -0.67) * mm, "mid": v(108.84, -0.38) * mm, "end": v(108.74, 0) * mm});
            skLineSegment(sketch, "E16.92.4", {"start": v(110.38, -1.51) * mm, "end": v(109.1, -0.67) * mm});
            skArc(sketch, "E16.92.5", {"start": v(110.38, -1.51) * mm, "mid": v(110.9, -2.1) * mm, "end": v(111.09, -2.88) * mm});
            skArc(sketch, "E16.93.0", {"start": v(110.15, 7.18) * mm, "mid": v(110.65, 7.8) * mm, "end": v(110.8, 8.58) * mm});
            skLineSegment(sketch, "E16.93.1", {"start": v(110.15, 7.18) * mm, "end": v(108.92, 6.27) * mm});
            skArc(sketch, "E16.93.2", {"start": v(108.92, 6.27) * mm, "mid": v(108.68, 5.97) * mm, "end": v(108.6, 5.59) * mm});
            skArc(sketch, "E16.93.3", {"start": v(109, 4.95) * mm, "mid": v(108.71, 5.22) * mm, "end": v(108.6, 5.59) * mm});
            skLineSegment(sketch, "E16.93.4", {"start": v(110.3, 4.17) * mm, "end": v(109, 4.95) * mm});
            skArc(sketch, "E16.93.5", {"start": v(110.3, 4.17) * mm, "mid": v(110.87, 3.6) * mm, "end": v(111.09, 2.84) * mm});
            skArc(sketch, "E16.94.0", {"start": v(109.64, 12.84) * mm, "mid": v(110.1, 13.48) * mm, "end": v(110.2, 14.27) * mm});
            skLineSegment(sketch, "E16.94.1", {"start": v(109.64, 12.84) * mm, "end": v(108.45, 11.87) * mm});
            skArc(sketch, "E16.94.2", {"start": v(108.45, 11.87) * mm, "mid": v(108.22, 11.56) * mm, "end": v(108.17, 11.17) * mm});
            skArc(sketch, "E16.94.3", {"start": v(108.6, 10.55) * mm, "mid": v(108.3, 10.8) * mm, "end": v(108.17, 11.17) * mm});
            skLineSegment(sketch, "E16.94.4", {"start": v(109.95, 9.84) * mm, "end": v(108.6, 10.55) * mm});
            skArc(sketch, "E16.94.5", {"start": v(109.95, 9.84) * mm, "mid": v(110.54, 9.31) * mm, "end": v(110.8, 8.56) * mm});
            skArc(sketch, "E16.95.0", {"start": v(108.83, 18.46) * mm, "mid": v(109.27, 19.13) * mm, "end": v(109.32, 19.92) * mm});
            skLineSegment(sketch, "E16.95.1", {"start": v(108.83, 18.46) * mm, "end": v(107.7, 17.44) * mm});
            skArc(sketch, "E16.95.2", {"start": v(107.7, 17.44) * mm, "mid": v(107.49, 17.11) * mm, "end": v(107.45, 16.73) * mm});
            skArc(sketch, "E16.95.3", {"start": v(107.9, 16.13) * mm, "mid": v(107.6, 16.37) * mm, "end": v(107.45, 16.73) * mm});
            skLineSegment(sketch, "E16.95.4", {"start": v(109.3, 15.5) * mm, "end": v(107.9, 16.13) * mm});
            skArc(sketch, "E16.95.5", {"start": v(109.3, 15.5) * mm, "mid": v(109.91, 14.99) * mm, "end": v(110.2, 14.25) * mm});
            skArc(sketch, "E16.96.0", {"start": v(107.74, 24.04) * mm, "mid": v(108.14, 24.73) * mm, "end": v(108.15, 25.52) * mm});
            skLineSegment(sketch, "E16.96.1", {"start": v(107.74, 24.04) * mm, "end": v(106.66, 22.96) * mm});
            skArc(sketch, "E16.96.2", {"start": v(106.66, 22.96) * mm, "mid": v(106.46, 22.62) * mm, "end": v(106.45, 22.24) * mm});
            skArc(sketch, "E16.96.3", {"start": v(106.93, 21.66) * mm, "mid": v(106.62, 21.89) * mm, "end": v(106.45, 22.24) * mm});
            skLineSegment(sketch, "E16.96.4", {"start": v(108.35, 21.1) * mm, "end": v(106.93, 21.66) * mm});
            skArc(sketch, "E16.96.5", {"start": v(108.35, 21.1) * mm, "mid": v(109, 20.63) * mm, "end": v(109.33, 19.9) * mm});
            skArc(sketch, "E16.97.0", {"start": v(106.36, 29.56) * mm, "mid": v(106.72, 30.26) * mm, "end": v(106.7, 31.06) * mm});
            skLineSegment(sketch, "E16.97.1", {"start": v(106.36, 29.56) * mm, "end": v(105.34, 28.42) * mm});
            skArc(sketch, "E16.97.2", {"start": v(105.34, 28.42) * mm, "mid": v(105.16, 28.07) * mm, "end": v(105.16, 27.69) * mm});
            skArc(sketch, "E16.97.3", {"start": v(105.67, 27.14) * mm, "mid": v(105.35, 27.35) * mm, "end": v(105.16, 27.69) * mm});
            skLineSegment(sketch, "E16.97.4", {"start": v(107.12, 26.65) * mm, "end": v(105.67, 27.14) * mm});
            skArc(sketch, "E16.97.5", {"start": v(107.12, 26.65) * mm, "mid": v(107.79, 26.21) * mm, "end": v(108.16, 25.5) * mm});
            skArc(sketch, "E16.98.0", {"start": v(104.7, 35) * mm, "mid": v(105.02, 35.72) * mm, "end": v(104.96, 36.5) * mm});
            skLineSegment(sketch, "E16.98.1", {"start": v(104.7, 35) * mm, "end": v(103.73, 33.8) * mm});
            skArc(sketch, "E16.98.2", {"start": v(103.73, 33.8) * mm, "mid": v(103.57, 33.45) * mm, "end": v(103.6, 33.06) * mm});
            skArc(sketch, "E16.98.3", {"start": v(104.14, 32.54) * mm, "mid": v(103.8, 32.73) * mm, "end": v(103.6, 33.06) * mm});
            skLineSegment(sketch, "E16.98.4", {"start": v(105.6, 32.13) * mm, "end": v(104.14, 32.54) * mm});
            skArc(sketch, "E16.98.5", {"start": v(105.6, 32.13) * mm, "mid": v(106.3, 31.72) * mm, "end": v(106.7, 31.04) * mm});
            skArc(sketch, "E16.99.0", {"start": v(102.75, 40.33) * mm, "mid": v(103.04, 41.08) * mm, "end": v(102.94, 41.86) * mm});
            skLineSegment(sketch, "E16.99.1", {"start": v(102.75, 40.33) * mm, "end": v(101.86, 39.1) * mm});
            skArc(sketch, "E16.99.2", {"start": v(101.86, 39.1) * mm, "mid": v(101.71, 38.74) * mm, "end": v(101.76, 38.35) * mm});
            skArc(sketch, "E16.99.3", {"start": v(102.32, 37.86) * mm, "mid": v(101.98, 38.03) * mm, "end": v(101.76, 38.35) * mm});
            skLineSegment(sketch, "E16.99.4", {"start": v(103.81, 37.52) * mm, "end": v(102.32, 37.86) * mm});
            skArc(sketch, "E16.99.5", {"start": v(103.81, 37.52) * mm, "mid": v(104.52, 37.15) * mm, "end": v(104.96, 36.5) * mm});
            skArc(sketch, "E16.100.0", {"start": v(100.54, 45.57) * mm, "mid": v(100.8, 46.33) * mm, "end": v(100.65, 47.1) * mm});
            skLineSegment(sketch, "E16.100.1", {"start": v(100.54, 45.57) * mm, "end": v(99.7, 44.29) * mm});
            skArc(sketch, "E16.100.2", {"start": v(99.7, 44.29) * mm, "mid": v(99.58, 43.92) * mm, "end": v(99.65, 43.54) * mm});
            skArc(sketch, "E16.100.3", {"start": v(100.24, 43.07) * mm, "mid": v(99.88, 43.23) * mm, "end": v(99.65, 43.54) * mm});
            skLineSegment(sketch, "E16.100.4", {"start": v(101.74, 42.81) * mm, "end": v(100.24, 43.07) * mm});
            skArc(sketch, "E16.100.5", {"start": v(101.74, 42.81) * mm, "mid": v(102.47, 42.49) * mm, "end": v(102.94, 41.85) * mm});
            skArc(sketch, "E16.101.0", {"start": v(98.06, 50.69) * mm, "mid": v(98.27, 51.45) * mm, "end": v(98.09, 52.23) * mm});
            skLineSegment(sketch, "E16.101.1", {"start": v(98.06, 50.69) * mm, "end": v(97.3, 49.36) * mm});
            skArc(sketch, "E16.101.2", {"start": v(97.3, 49.36) * mm, "mid": v(97.2, 48.99) * mm, "end": v(97.27, 48.61) * mm});
            skArc(sketch, "E16.101.3", {"start": v(97.89, 48.18) * mm, "mid": v(97.53, 48.32) * mm, "end": v(97.27, 48.61) * mm});
            skLineSegment(sketch, "E16.101.4", {"start": v(99.4, 48) * mm, "end": v(97.89, 48.18) * mm});
            skArc(sketch, "E16.101.5", {"start": v(99.4, 48) * mm, "mid": v(100.15, 47.7) * mm, "end": v(100.65, 47.1) * mm});
            skArc(sketch, "E16.102.0", {"start": v(95.32, 55.67) * mm, "mid": v(95.5, 56.44) * mm, "end": v(95.27, 57.2) * mm});
            skLineSegment(sketch, "E16.102.1", {"start": v(95.32, 55.67) * mm, "end": v(94.63, 54.3) * mm});
            skArc(sketch, "E16.102.2", {"start": v(94.63, 54.3) * mm, "mid": v(94.54, 53.93) * mm, "end": v(94.64, 53.55) * mm});
            skArc(sketch, "E16.102.3", {"start": v(95.28, 53.15) * mm, "mid": v(94.91, 53.27) * mm, "end": v(94.64, 53.55) * mm});
            skLineSegment(sketch, "E16.102.4", {"start": v(96.8, 53.05) * mm, "end": v(95.28, 53.15) * mm});
            skArc(sketch, "E16.102.5", {"start": v(96.8, 53.05) * mm, "mid": v(97.56, 52.8) * mm, "end": v(98.1, 52.21) * mm});
            skArc(sketch, "E16.103.0", {"start": v(92.33, 60.5) * mm, "mid": v(92.46, 61.28) * mm, "end": v(92.2, 62.03) * mm});
            skLineSegment(sketch, "E16.103.1", {"start": v(92.33, 60.5) * mm, "end": v(91.7, 59.1) * mm});
            skArc(sketch, "E16.103.2", {"start": v(91.7, 59.1) * mm, "mid": v(91.64, 58.72) * mm, "end": v(91.76, 58.35) * mm});
            skArc(sketch, "E16.103.3", {"start": v(92.42, 57.99) * mm, "mid": v(92.04, 58.09) * mm, "end": v(91.76, 58.35) * mm});
            skLineSegment(sketch, "E16.103.4", {"start": v(93.94, 57.96) * mm, "end": v(92.42, 57.99) * mm});
            skArc(sketch, "E16.103.5", {"start": v(93.94, 57.96) * mm, "mid": v(94.71, 57.75) * mm, "end": v(95.28, 57.2) * mm});
            skArc(sketch, "E16.104.0", {"start": v(89.1, 65.17) * mm, "mid": v(89.18, 65.96) * mm, "end": v(88.88, 66.7) * mm});
            skLineSegment(sketch, "E16.104.1", {"start": v(89.1, 65.17) * mm, "end": v(88.54, 63.75) * mm});
            skArc(sketch, "E16.104.2", {"start": v(88.54, 63.75) * mm, "mid": v(88.5, 63.36) * mm, "end": v(88.63, 63) * mm});
            skArc(sketch, "E16.104.3", {"start": v(89.3, 62.67) * mm, "mid": v(88.93, 62.75) * mm, "end": v(88.63, 63) * mm});
            skLineSegment(sketch, "E16.104.4", {"start": v(90.84, 62.72) * mm, "end": v(89.3, 62.67) * mm});
            skArc(sketch, "E16.104.5", {"start": v(90.84, 62.72) * mm, "mid": v(91.61, 62.55) * mm, "end": v(92.2, 62.02) * mm});
            skArc(sketch, "E16.105.0", {"start": v(85.62, 69.67) * mm, "mid": v(85.67, 70.47) * mm, "end": v(85.33, 71.19) * mm});
            skLineSegment(sketch, "E16.105.1", {"start": v(85.62, 69.67) * mm, "end": v(85.14, 68.22) * mm});
            skArc(sketch, "E16.105.2", {"start": v(85.14, 68.22) * mm, "mid": v(85.11, 67.83) * mm, "end": v(85.27, 67.48) * mm});
            skArc(sketch, "E16.105.3", {"start": v(85.96, 67.18) * mm, "mid": v(85.58, 67.24) * mm, "end": v(85.27, 67.48) * mm});
            skLineSegment(sketch, "E16.105.4", {"start": v(87.49, 67.31) * mm, "end": v(85.96, 67.18) * mm});
            skArc(sketch, "E16.105.5", {"start": v(87.49, 67.31) * mm, "mid": v(88.27, 67.18) * mm, "end": v(88.9, 66.68) * mm});
            skArc(sketch, "E16.106.0", {"start": v(81.92, 73.99) * mm, "mid": v(81.93, 74.78) * mm, "end": v(81.55, 75.48) * mm});
            skLineSegment(sketch, "E16.106.1", {"start": v(81.92, 73.99) * mm, "end": v(81.52, 72.51) * mm});
            skArc(sketch, "E16.106.2", {"start": v(81.52, 72.51) * mm, "mid": v(81.5, 72.13) * mm, "end": v(81.69, 71.78) * mm});
            skArc(sketch, "E16.106.3", {"start": v(82.4, 71.52) * mm, "mid": v(82, 71.56) * mm, "end": v(81.69, 71.78) * mm});
            skLineSegment(sketch, "E16.106.4", {"start": v(83.9, 71.73) * mm, "end": v(82.4, 71.52) * mm});
            skArc(sketch, "E16.106.5", {"start": v(83.9, 71.73) * mm, "mid": v(84.7, 71.64) * mm, "end": v(85.34, 71.17) * mm});
            skArc(sketch, "E16.107.0", {"start": v(78, 78.1) * mm, "mid": v(77.97, 78.9) * mm, "end": v(77.56, 79.58) * mm});
            skLineSegment(sketch, "E16.107.1", {"start": v(78, 78.1) * mm, "end": v(77.68, 76.61) * mm});
            skArc(sketch, "E16.107.2", {"start": v(77.68, 76.61) * mm, "mid": v(77.69, 76.23) * mm, "end": v(77.88, 75.9) * mm});
            skArc(sketch, "E16.107.3", {"start": v(78.6, 75.67) * mm, "mid": v(78.21, 75.69) * mm, "end": v(77.88, 75.9) * mm});
            skLineSegment(sketch, "E16.107.4", {"start": v(80.1, 75.95) * mm, "end": v(78.6, 75.67) * mm});
            skArc(sketch, "E16.107.5", {"start": v(80.1, 75.95) * mm, "mid": v(80.9, 75.9) * mm, "end": v(81.57, 75.47) * mm});
            skArc(sketch, "E16.108.0", {"start": v(73.88, 82.02) * mm, "mid": v(73.8, 82.81) * mm, "end": v(73.36, 83.47) * mm});
            skLineSegment(sketch, "E16.108.1", {"start": v(73.88, 82.02) * mm, "end": v(73.63, 80.51) * mm});
            skArc(sketch, "E16.108.2", {"start": v(73.63, 80.51) * mm, "mid": v(73.66, 80.12) * mm, "end": v(73.87, 79.8) * mm});
            skArc(sketch, "E16.108.3", {"start": v(74.6, 79.61) * mm, "mid": v(74.21, 79.61) * mm, "end": v(73.87, 79.8) * mm});
            skLineSegment(sketch, "E16.108.4", {"start": v(76.09, 79.98) * mm, "end": v(74.6, 79.61) * mm});
            skArc(sketch, "E16.108.5", {"start": v(76.09, 79.98) * mm, "mid": v(76.88, 79.96) * mm, "end": v(77.57, 79.57) * mm});
            skArc(sketch, "E16.109.0", {"start": v(69.56, 85.71) * mm, "mid": v(69.45, 86.5) * mm, "end": v(68.97, 87.14) * mm});
            skLineSegment(sketch, "E16.109.1", {"start": v(69.56, 85.71) * mm, "end": v(69.39, 84.2) * mm});
            skArc(sketch, "E16.109.2", {"start": v(69.39, 84.2) * mm, "mid": v(69.44, 83.81) * mm, "end": v(69.67, 83.5) * mm});
            skArc(sketch, "E16.109.3", {"start": v(70.4, 83.35) * mm, "mid": v(70.02, 83.33) * mm, "end": v(69.67, 83.5) * mm});
            skLineSegment(sketch, "E16.109.4", {"start": v(71.87, 83.79) * mm, "end": v(70.4, 83.35) * mm});
            skArc(sketch, "E16.109.5", {"start": v(71.87, 83.79) * mm, "mid": v(72.66, 83.82) * mm, "end": v(73.37, 83.46) * mm});
            skArc(sketch, "E16.110.0", {"start": v(65.05, 89.18) * mm, "mid": v(64.9, 89.96) * mm, "end": v(64.39, 90.57) * mm});
            skLineSegment(sketch, "E16.110.1", {"start": v(65.05, 89.18) * mm, "end": v(64.96, 87.65) * mm});
            skArc(sketch, "E16.110.2", {"start": v(64.96, 87.65) * mm, "mid": v(65.03, 87.27) * mm, "end": v(65.28, 86.97) * mm});
            skArc(sketch, "E16.110.3", {"start": v(66.02, 86.86) * mm, "mid": v(65.63, 86.82) * mm, "end": v(65.28, 86.97) * mm});
            skLineSegment(sketch, "E16.110.4", {"start": v(67.46, 87.37) * mm, "end": v(66.02, 86.86) * mm});
            skArc(sketch, "E16.110.5", {"start": v(67.46, 87.37) * mm, "mid": v(68.25, 87.45) * mm, "end": v(68.98, 87.12) * mm});
            skArc(sketch, "E16.111.0", {"start": v(60.38, 92.41) * mm, "mid": v(60.18, 93.18) * mm, "end": v(59.64, 93.76) * mm});
            skLineSegment(sketch, "E16.111.1", {"start": v(60.38, 92.41) * mm, "end": v(60.36, 90.88) * mm});
            skArc(sketch, "E16.111.2", {"start": v(60.36, 90.88) * mm, "mid": v(60.45, 90.5) * mm, "end": v(60.71, 90.22) * mm});
            skArc(sketch, "E16.111.3", {"start": v(61.46, 90.14) * mm, "mid": v(61.08, 90.09) * mm, "end": v(60.71, 90.22) * mm});
            skLineSegment(sketch, "E16.111.4", {"start": v(62.87, 90.73) * mm, "end": v(61.46, 90.14) * mm});
            skArc(sketch, "E16.111.5", {"start": v(62.87, 90.73) * mm, "mid": v(63.66, 90.84) * mm, "end": v(64.4, 90.56) * mm});
            skArc(sketch, "E16.112.0", {"start": v(55.54, 95.4) * mm, "mid": v(55.3, 96.16) * mm, "end": v(54.73, 96.71) * mm});
            skLineSegment(sketch, "E16.112.1", {"start": v(55.54, 95.4) * mm, "end": v(55.6, 93.87) * mm});
            skArc(sketch, "E16.112.2", {"start": v(55.6, 93.87) * mm, "mid": v(55.71, 93.5) * mm, "end": v(55.99, 93.22) * mm});
            skArc(sketch, "E16.112.3", {"start": v(56.74, 93.19) * mm, "mid": v(56.36, 93.11) * mm, "end": v(55.99, 93.22) * mm});
            skLineSegment(sketch, "E16.112.4", {"start": v(58.12, 93.85) * mm, "end": v(56.74, 93.19) * mm});
            skArc(sketch, "E16.112.5", {"start": v(58.12, 93.85) * mm, "mid": v(58.9, 94) * mm, "end": v(59.66, 93.75) * mm});
            skArc(sketch, "E16.113.0", {"start": v(50.55, 98.13) * mm, "mid": v(50.28, 98.88) * mm, "end": v(49.68, 99.4) * mm});
            skLineSegment(sketch, "E16.113.1", {"start": v(50.55, 98.13) * mm, "end": v(50.7, 96.6) * mm});
            skArc(sketch, "E16.113.2", {"start": v(50.7, 96.6) * mm, "mid": v(50.83, 96.24) * mm, "end": v(51.11, 95.98) * mm});
            skArc(sketch, "E16.113.3", {"start": v(51.87, 95.98) * mm, "mid": v(51.5, 95.89) * mm, "end": v(51.11, 95.98) * mm});
            skLineSegment(sketch, "E16.113.4", {"start": v(53.2, 96.71) * mm, "end": v(51.87, 95.98) * mm});
            skArc(sketch, "E16.113.5", {"start": v(53.2, 96.71) * mm, "mid": v(53.98, 96.9) * mm, "end": v(54.75, 96.7) * mm});
            skArc(sketch, "E16.114.0", {"start": v(45.44, 100.6) * mm, "mid": v(45.13, 101.33) * mm, "end": v(44.5, 101.83) * mm});
            skLineSegment(sketch, "E16.114.1", {"start": v(45.44, 100.6) * mm, "end": v(45.66, 99.09) * mm});
            skArc(sketch, "E16.114.2", {"start": v(45.66, 99.09) * mm, "mid": v(45.8, 98.73) * mm, "end": v(46.1, 98.49) * mm});
            skArc(sketch, "E16.114.3", {"start": v(46.86, 98.53) * mm, "mid": v(46.49, 98.41) * mm, "end": v(46.1, 98.49) * mm});
            skLineSegment(sketch, "E16.114.4", {"start": v(48.16, 99.33) * mm, "end": v(46.86, 98.53) * mm});
            skArc(sketch, "E16.114.5", {"start": v(48.16, 99.33) * mm, "mid": v(48.92, 99.56) * mm, "end": v(49.7, 99.4) * mm});
            skArc(sketch, "E16.115.0", {"start": v(40.2, 102.8) * mm, "mid": v(39.85, 103.52) * mm, "end": v(39.2, 103.98) * mm});
            skLineSegment(sketch, "E16.115.1", {"start": v(40.2, 102.8) * mm, "end": v(40.5, 101.3) * mm});
            skArc(sketch, "E16.115.2", {"start": v(40.5, 101.3) * mm, "mid": v(40.66, 100.96) * mm, "end": v(40.97, 100.73) * mm});
            skArc(sketch, "E16.115.3", {"start": v(41.72, 100.8) * mm, "mid": v(41.36, 100.67) * mm, "end": v(40.97, 100.73) * mm});
            skLineSegment(sketch, "E16.115.4", {"start": v(42.98, 101.67) * mm, "end": v(41.72, 100.8) * mm});
            skArc(sketch, "E16.115.5", {"start": v(42.98, 101.67) * mm, "mid": v(43.73, 101.94) * mm, "end": v(44.52, 101.82) * mm});
            skArc(sketch, "E16.116.0", {"start": v(34.85, 104.74) * mm, "mid": v(34.47, 105.44) * mm, "end": v(33.8, 105.86) * mm});
            skLineSegment(sketch, "E16.116.1", {"start": v(34.85, 104.74) * mm, "end": v(35.23, 103.26) * mm});
            skArc(sketch, "E16.116.2", {"start": v(35.23, 103.26) * mm, "mid": v(35.41, 102.92) * mm, "end": v(35.74, 102.7) * mm});
            skArc(sketch, "E16.116.3", {"start": v(36.48, 102.82) * mm, "mid": v(36.12, 102.67) * mm, "end": v(35.74, 102.7) * mm});
            skLineSegment(sketch, "E16.116.4", {"start": v(37.7, 103.75) * mm, "end": v(36.48, 102.82) * mm});
            skArc(sketch, "E16.116.5", {"start": v(37.7, 103.75) * mm, "mid": v(38.43, 104.06) * mm, "end": v(39.22, 103.98) * mm});
            skArc(sketch, "E16.117.0", {"start": v(29.41, 106.4) * mm, "mid": v(29, 107.07) * mm, "end": v(28.3, 107.46) * mm});
            skLineSegment(sketch, "E16.117.1", {"start": v(29.41, 106.4) * mm, "end": v(29.86, 104.94) * mm});
            skArc(sketch, "E16.117.2", {"start": v(29.86, 104.94) * mm, "mid": v(30.07, 104.6) * mm, "end": v(30.4, 104.4) * mm});
            skArc(sketch, "E16.117.3", {"start": v(31.14, 104.56) * mm, "mid": v(30.79, 104.4) * mm, "end": v(30.4, 104.4) * mm});
            skLineSegment(sketch, "E16.117.4", {"start": v(32.3, 105.55) * mm, "end": v(31.14, 104.56) * mm});
            skArc(sketch, "E16.117.5", {"start": v(32.3, 105.55) * mm, "mid": v(33.02, 105.9) * mm, "end": v(33.81, 105.86) * mm});
            skArc(sketch, "E16.118.0", {"start": v(23.9, 107.77) * mm, "mid": v(23.44, 108.42) * mm, "end": v(22.73, 108.78) * mm});
            skLineSegment(sketch, "E16.118.1", {"start": v(23.9, 107.77) * mm, "end": v(24.42, 106.33) * mm});
            skArc(sketch, "E16.118.2", {"start": v(24.42, 106.33) * mm, "mid": v(24.64, 106.01) * mm, "end": v(24.99, 105.83) * mm});
            skArc(sketch, "E16.118.3", {"start": v(25.71, 106.03) * mm, "mid": v(25.37, 105.84) * mm, "end": v(24.99, 105.83) * mm});
            skLineSegment(sketch, "E16.118.4", {"start": v(26.82, 107.08) * mm, "end": v(25.71, 106.03) * mm});
            skArc(sketch, "E16.118.5", {"start": v(26.82, 107.08) * mm, "mid": v(27.52, 107.46) * mm, "end": v(28.32, 107.46) * mm});
            skArc(sketch, "E16.119.0", {"start": v(18.32, 108.86) * mm, "mid": v(17.83, 109.49) * mm, "end": v(17.1, 109.8) * mm});
            skLineSegment(sketch, "E16.119.1", {"start": v(18.32, 108.86) * mm, "end": v(18.92, 107.45) * mm});
            skArc(sketch, "E16.119.2", {"start": v(18.92, 107.45) * mm, "mid": v(19.15, 107.14) * mm, "end": v(19.5, 106.98) * mm});
            skArc(sketch, "E16.119.3", {"start": v(20.22, 107.21) * mm, "mid": v(19.9, 107) * mm, "end": v(19.5, 106.98) * mm});
            skLineSegment(sketch, "E16.119.4", {"start": v(21.28, 108.32) * mm, "end": v(20.22, 107.21) * mm});
            skArc(sketch, "E16.119.5", {"start": v(21.28, 108.32) * mm, "mid": v(21.95, 108.73) * mm, "end": v(22.75, 108.77) * mm});
            skArc(sketch, "E16.120.0", {"start": v(12.69, 109.65) * mm, "mid": v(12.17, 110.26) * mm, "end": v(11.43, 110.54) * mm});
            skLineSegment(sketch, "E16.120.1", {"start": v(12.69, 109.65) * mm, "end": v(13.36, 108.28) * mm});
            skArc(sketch, "E16.120.2", {"start": v(13.36, 108.28) * mm, "mid": v(13.61, 107.98) * mm, "end": v(13.97, 107.84) * mm});
            skArc(sketch, "E16.120.3", {"start": v(14.67, 108.11) * mm, "mid": v(14.36, 107.89) * mm, "end": v(13.97, 107.84) * mm});
            skLineSegment(sketch, "E16.120.4", {"start": v(15.67, 109.27) * mm, "end": v(14.67, 108.11) * mm});
            skArc(sketch, "E16.120.5", {"start": v(15.67, 109.27) * mm, "mid": v(16.33, 109.72) * mm, "end": v(17.12, 109.8) * mm});
            skArc(sketch, "E16.121.0", {"start": v(7.03, 110.16) * mm, "mid": v(6.48, 110.74) * mm, "end": v(5.72, 110.98) * mm});
            skLineSegment(sketch, "E16.121.1", {"start": v(7.03, 110.16) * mm, "end": v(7.77, 108.83) * mm});
            skArc(sketch, "E16.121.2", {"start": v(7.77, 108.83) * mm, "mid": v(8.03, 108.54) * mm, "end": v(8.4, 108.42) * mm});
            skArc(sketch, "E16.121.3", {"start": v(9.09, 108.72) * mm, "mid": v(8.78, 108.48) * mm, "end": v(8.4, 108.42) * mm});
            skLineSegment(sketch, "E16.121.4", {"start": v(10.03, 109.93) * mm, "end": v(9.09, 108.72) * mm});
            skArc(sketch, "E16.121.5", {"start": v(10.03, 109.93) * mm, "mid": v(10.66, 110.42) * mm, "end": v(11.44, 110.53) * mm});
            skSolve(sketch);
        }
        {
            var Q0;
            Q0=qSketchRegion(id+"F2",true);
            extrude(context, id + "F3", {"entities" : qUnion([Q0]), "operationType" : NewBodyOperationType.REMOVE, "oppositeDirection" : true, "depth" : 25.4 * mm});
        }
        {
            var Q0;
            Q0=qCreatedBy(makeId("Top.planeOp"),FACE);
            var sketch = newSketch(context, id + "F4", { "sketchPlane" : qUnion([Q0])});
            skCircle(sketch, "E17", {"center": v(0, 0) * mm, "radius": 106.71 * mm});
            skSolve(sketch);
        }
        {
            var Q0;
            Q0=qSketchRegion(id+"F4",true);
            extrude(context, id + "F5", {"entities" : qUnion([Q0]), "depth" : 19.05 * mm, "hasSecondDirection" : true, "secondDirectionOppositeDirection" : true, "secondDirectionDepth" : 6.35 * mm});
        }
        {
            var Q0;
            Q0=makeQuery(id+"F5.opExtrude","CAP_EDGE",EDGE,{"disambiguationData":[OSD([sQuery(id+"F4.wireOp",EDGE,"E17")])],"isStart":false});
            var Q1;
            Q1=makeQuery(id+"F5.opExtrude","CAP_EDGE",EDGE,{"disambiguationData":[OSD([sQuery(id+"F4.wireOp",EDGE,"E17")])],"isStart":true});
            fillet(context, id + "F6", {"entities" : qUnion([Q0, Q1]), "radius" : 6.35 * mm, "tangentPropagation" : true, "allowEdgeOverflow" : false});
        }
        {
            var Q0;
            Q0=makeQuery(id+"F5.opExtrude","SWEPT_BODY",BODY,{"disambiguationData":[OSD([sQuery(id+"F4.wireOp",EDGE,"E17")])]});
            deleteBodies(context, id + "F7", {"entities" : qUnion([Q0])});
        }
        {
            var Q0;
            Q0=qCreatedBy(makeId("Right.planeOp"),FACE);
            var sketch = newSketch(context, id + "F8", { "sketchPlane" : qUnion([Q0])});
            skLineSegment(sketch, "E18", {"start": v(-113.32, 3.36) * mm, "end": v(-113.32, 9.34) * mm});
            skLineSegment(sketch, "E19", {"start": v(-113.32, 9.34) * mm, "end": v(-101.6, 12.7) * mm});
            skLineSegment(sketch, "E20", {"start": v(-101.6, 0) * mm, "end": v(-113.32, 3.36) * mm});
            skLineSegment(sketch, "E21", {"start": v(-101.6, 0) * mm, "end": v(-101.6, 0) * mm});
            skLineSegment(sketch, "E22", {"start": v(-101.6, 0) * mm, "end": v(-119.44, 0) * mm});
            skLineSegment(sketch, "E23", {"start": v(-119.44, 0) * mm, "end": v(-119.44, 12.7) * mm});
            skLineSegment(sketch, "E24", {"start": v(-119.44, 12.7) * mm, "end": v(-101.6, 12.7) * mm});
            skLineSegment(sketch, "E25", {"start": v(0, 0) * mm, "end": v(0, -54.5) * mm, "construction": true});
            skSolve(sketch);
        }
        {
            var Q0;
            Q0=qSketchRegion(id+"F8",true);
            var Q1;
            Q1=sQuery(id+"F8.wireOp",EDGE,"E25");
            revolve(context, id + "F9", {"operationType" : NewBodyOperationType.REMOVE, "entities" : qUnion([Q0]), "axis" : qUnion([Q1]), "revolveType" : RevolveType.FULL, "oppositeDirection" : true});
        }
        {
            var Q0;
            Q0=qCreatedBy(makeId("Top.planeOp"),FACE);
            var sketch = newSketch(context, id + "F10", { "sketchPlane" : qUnion([Q0])});
            skLineSegment(sketch, "E26", {"start": v(0, 0) * mm, "end": v(0, -159.1) * mm, "construction": true});
            skLineSegment(sketch, "E27.rect.left", {"start": v(1.52, -112.3) * mm, "end": v(1.52, -108.74) * mm});
            skPoint(sketch, "E27.rect.middle", {"position": v(0, -107.88) * mm});
            skPoint(sketch, "E28.center", {"position": v(0, 0) * mm});
            skLineSegment(sketch, "E29", {"start": v(0, 0) * mm, "end": v(11.42, -110.54) * mm, "construction": true});
            skCircle(sketch, "E30", {"center": v(0, 0) * mm, "radius": 108.37 * mm, "construction": true});
            skLineSegment(sketch, "E31", {"start": v(0, 0) * mm, "end": v(5.71, -110.98) * mm, "construction": true});
            skLineSegment(sketch, "E32.MirrorCS", {"start": v(10.01, -111.87) * mm, "end": v(1.52, -112.3) * mm});
            skLineSegment(sketch, "E33.MirrorCS", {"start": v(10.01, -111.87) * mm, "end": v(9.65, -108.33) * mm});
            skLineSegment(sketch, "E34.MirrorCS", {"start": v(1.52, -112.3) * mm, "end": v(10.01, -111.87) * mm});
            skLineSegment(sketch, "E35", {"start": v(1.52, -108.74) * mm, "end": v(3.48, -107.62) * mm});
            skLineSegment(sketch, "E36", {"start": v(8.02, -107.38) * mm, "end": v(9.65, -108.33) * mm});
            skLineSegment(sketch, "E37", {"start": v(3.48, -107.62) * mm, "end": v(8.02, -107.38) * mm});
            skPoint(sketch, "E38", {"position": v(5.75, -107.5) * mm});
            skLineSegment(sketch, "E39.1.0", {"start": v(13.06, -111.55) * mm, "end": v(12.7, -108.01) * mm});
            skLineSegment(sketch, "E39.1.1", {"start": v(13.06, -111.55) * mm, "end": v(21.46, -110.25) * mm});
            skLineSegment(sketch, "E39.1.2", {"start": v(12.7, -108.01) * mm, "end": v(14.52, -106.69) * mm});
            skLineSegment(sketch, "E39.1.3", {"start": v(14.52, -106.69) * mm, "end": v(19.01, -106) * mm});
            skLineSegment(sketch, "E39.1.4", {"start": v(21.46, -110.25) * mm, "end": v(20.73, -106.76) * mm});
            skLineSegment(sketch, "E39.1.5", {"start": v(19.01, -106) * mm, "end": v(20.73, -106.76) * mm});
            skLineSegment(sketch, "E39.1.6", {"start": v(21.46, -110.25) * mm, "end": v(13.06, -111.55) * mm});
            skLineSegment(sketch, "E39.1.7", {"start": v(13.06, -111.55) * mm, "end": v(12.7, -108.01) * mm});
            skLineSegment(sketch, "E39.1.8", {"start": v(21.46, -110.25) * mm, "end": v(20.73, -106.76) * mm});
            skLineSegment(sketch, "E39.1.9", {"start": v(21.46, -110.25) * mm, "end": v(20.73, -106.76) * mm});
            skLineSegment(sketch, "E39.1.10", {"start": v(13.06, -111.55) * mm, "end": v(12.7, -108.01) * mm});
            skLineSegment(sketch, "E39.2.0", {"start": v(24.46, -109.62) * mm, "end": v(23.74, -106.13) * mm});
            skLineSegment(sketch, "E39.2.1", {"start": v(24.46, -109.62) * mm, "end": v(32.68, -107.46) * mm});
            skLineSegment(sketch, "E39.2.2", {"start": v(23.74, -106.13) * mm, "end": v(25.42, -104.63) * mm});
            skLineSegment(sketch, "E39.2.3", {"start": v(25.42, -104.63) * mm, "end": v(29.81, -103.47) * mm});
            skLineSegment(sketch, "E39.2.4", {"start": v(32.68, -107.46) * mm, "end": v(31.6, -104.06) * mm});
            skLineSegment(sketch, "E39.2.5", {"start": v(29.81, -103.47) * mm, "end": v(31.6, -104.06) * mm});
            skLineSegment(sketch, "E39.2.6", {"start": v(32.68, -107.46) * mm, "end": v(24.46, -109.62) * mm});
            skLineSegment(sketch, "E39.2.7", {"start": v(24.46, -109.62) * mm, "end": v(23.74, -106.13) * mm});
            skLineSegment(sketch, "E39.2.8", {"start": v(32.68, -107.46) * mm, "end": v(31.6, -104.06) * mm});
            skLineSegment(sketch, "E39.2.9", {"start": v(32.68, -107.46) * mm, "end": v(31.6, -104.06) * mm});
            skLineSegment(sketch, "E39.2.10", {"start": v(24.46, -109.62) * mm, "end": v(23.74, -106.13) * mm});
            skLineSegment(sketch, "E39.3.0", {"start": v(35.6, -106.52) * mm, "end": v(34.52, -103.13) * mm});
            skLineSegment(sketch, "E39.3.1", {"start": v(35.6, -106.52) * mm, "end": v(43.56, -103.53) * mm});
            skLineSegment(sketch, "E39.3.2", {"start": v(34.52, -103.13) * mm, "end": v(36.04, -101.46) * mm});
            skLineSegment(sketch, "E39.3.3", {"start": v(36.04, -101.46) * mm, "end": v(40.3, -99.86) * mm});
            skLineSegment(sketch, "E39.3.4", {"start": v(43.56, -103.53) * mm, "end": v(42.13, -100.26) * mm});
            skLineSegment(sketch, "E39.3.5", {"start": v(40.3, -99.86) * mm, "end": v(42.13, -100.26) * mm});
            skLineSegment(sketch, "E39.3.6", {"start": v(43.56, -103.53) * mm, "end": v(35.6, -106.52) * mm});
            skLineSegment(sketch, "E39.3.7", {"start": v(35.6, -106.52) * mm, "end": v(34.52, -103.13) * mm});
            skLineSegment(sketch, "E39.3.8", {"start": v(43.56, -103.53) * mm, "end": v(42.13, -100.26) * mm});
            skLineSegment(sketch, "E39.3.9", {"start": v(43.56, -103.53) * mm, "end": v(42.13, -100.26) * mm});
            skLineSegment(sketch, "E39.3.10", {"start": v(35.6, -106.52) * mm, "end": v(34.52, -103.13) * mm});
            skLineSegment(sketch, "E39.4.0", {"start": v(46.37, -102.3) * mm, "end": v(44.94, -99.03) * mm});
            skLineSegment(sketch, "E39.4.1", {"start": v(46.37, -102.3) * mm, "end": v(53.97, -98.5) * mm});
            skLineSegment(sketch, "E39.4.2", {"start": v(44.94, -99.03) * mm, "end": v(46.28, -97.22) * mm});
            skLineSegment(sketch, "E39.4.3", {"start": v(46.28, -97.22) * mm, "end": v(50.35, -95.19) * mm});
            skLineSegment(sketch, "E39.4.4", {"start": v(53.97, -98.5) * mm, "end": v(52.22, -95.4) * mm});
            skLineSegment(sketch, "E39.4.5", {"start": v(50.35, -95.19) * mm, "end": v(52.22, -95.4) * mm});
            skLineSegment(sketch, "E39.4.6", {"start": v(53.97, -98.5) * mm, "end": v(46.37, -102.3) * mm});
            skLineSegment(sketch, "E39.4.7", {"start": v(46.37, -102.3) * mm, "end": v(44.94, -99.03) * mm});
            skLineSegment(sketch, "E39.4.8", {"start": v(53.97, -98.5) * mm, "end": v(52.22, -95.4) * mm});
            skLineSegment(sketch, "E39.4.9", {"start": v(53.97, -98.5) * mm, "end": v(52.22, -95.4) * mm});
            skLineSegment(sketch, "E39.4.10", {"start": v(46.37, -102.3) * mm, "end": v(44.94, -99.03) * mm});
            skLineSegment(sketch, "E39.5.0", {"start": v(56.64, -96.99) * mm, "end": v(54.89, -93.89) * mm});
            skLineSegment(sketch, "E39.5.1", {"start": v(56.64, -96.99) * mm, "end": v(63.82, -92.43) * mm});
            skLineSegment(sketch, "E39.5.2", {"start": v(54.89, -93.89) * mm, "end": v(56.03, -91.95) * mm});
            skLineSegment(sketch, "E39.5.3", {"start": v(56.03, -91.95) * mm, "end": v(59.87, -89.5) * mm});
            skLineSegment(sketch, "E39.5.4", {"start": v(63.82, -92.43) * mm, "end": v(61.75, -89.52) * mm});
            skLineSegment(sketch, "E39.5.5", {"start": v(59.87, -89.5) * mm, "end": v(61.75, -89.52) * mm});
            skLineSegment(sketch, "E39.5.6", {"start": v(63.82, -92.43) * mm, "end": v(56.64, -96.99) * mm});
            skLineSegment(sketch, "E39.5.7", {"start": v(56.64, -96.99) * mm, "end": v(54.89, -93.89) * mm});
            skLineSegment(sketch, "E39.5.8", {"start": v(63.82, -92.43) * mm, "end": v(61.75, -89.52) * mm});
            skLineSegment(sketch, "E39.5.9", {"start": v(63.82, -92.43) * mm, "end": v(61.75, -89.52) * mm});
            skLineSegment(sketch, "E39.5.10", {"start": v(56.64, -96.99) * mm, "end": v(54.89, -93.89) * mm});
            skLineSegment(sketch, "E39.6.0", {"start": v(66.31, -90.65) * mm, "end": v(64.25, -87.75) * mm});
            skLineSegment(sketch, "E39.6.1", {"start": v(66.31, -90.65) * mm, "end": v(72.98, -85.37) * mm});
            skLineSegment(sketch, "E39.6.2", {"start": v(64.25, -87.75) * mm, "end": v(65.19, -85.7) * mm});
            skLineSegment(sketch, "E39.6.3", {"start": v(65.19, -85.7) * mm, "end": v(68.75, -82.88) * mm});
            skLineSegment(sketch, "E39.6.4", {"start": v(72.98, -85.37) * mm, "end": v(70.63, -82.7) * mm});
            skLineSegment(sketch, "E39.6.5", {"start": v(68.75, -82.88) * mm, "end": v(70.63, -82.7) * mm});
            skLineSegment(sketch, "E39.6.6", {"start": v(72.98, -85.37) * mm, "end": v(66.31, -90.65) * mm});
            skLineSegment(sketch, "E39.6.7", {"start": v(66.31, -90.65) * mm, "end": v(64.25, -87.75) * mm});
            skLineSegment(sketch, "E39.6.8", {"start": v(72.98, -85.37) * mm, "end": v(70.63, -82.7) * mm});
            skLineSegment(sketch, "E39.6.9", {"start": v(72.98, -85.37) * mm, "end": v(70.63, -82.7) * mm});
            skLineSegment(sketch, "E39.6.10", {"start": v(66.31, -90.65) * mm, "end": v(64.25, -87.75) * mm});
            skLineSegment(sketch, "E39.7.0", {"start": v(75.28, -83.35) * mm, "end": v(72.93, -80.67) * mm});
            skLineSegment(sketch, "E39.7.1", {"start": v(75.28, -83.35) * mm, "end": v(81.37, -77.42) * mm});
            skLineSegment(sketch, "E39.7.2", {"start": v(72.93, -80.67) * mm, "end": v(73.65, -78.54) * mm});
            skLineSegment(sketch, "E39.7.3", {"start": v(73.65, -78.54) * mm, "end": v(76.91, -75.37) * mm});
            skLineSegment(sketch, "E39.7.4", {"start": v(81.37, -77.42) * mm, "end": v(78.76, -75) * mm});
            skLineSegment(sketch, "E39.7.5", {"start": v(76.91, -75.37) * mm, "end": v(78.76, -75) * mm});
            skLineSegment(sketch, "E39.7.6", {"start": v(81.37, -77.42) * mm, "end": v(75.28, -83.35) * mm});
            skLineSegment(sketch, "E39.7.7", {"start": v(75.28, -83.35) * mm, "end": v(72.93, -80.67) * mm});
            skLineSegment(sketch, "E39.7.8", {"start": v(81.37, -77.42) * mm, "end": v(78.76, -75) * mm});
            skLineSegment(sketch, "E39.7.9", {"start": v(81.37, -77.42) * mm, "end": v(78.76, -75) * mm});
            skLineSegment(sketch, "E39.7.10", {"start": v(75.28, -83.35) * mm, "end": v(72.93, -80.67) * mm});
            skLineSegment(sketch, "E39.8.0", {"start": v(83.45, -75.17) * mm, "end": v(80.84, -72.75) * mm});
            skLineSegment(sketch, "E39.8.1", {"start": v(83.45, -75.17) * mm, "end": v(88.9, -68.64) * mm});
            skLineSegment(sketch, "E39.8.2", {"start": v(80.84, -72.75) * mm, "end": v(81.34, -70.55) * mm});
            skLineSegment(sketch, "E39.8.3", {"start": v(81.34, -70.55) * mm, "end": v(84.25, -67.06) * mm});
            skLineSegment(sketch, "E39.8.4", {"start": v(88.9, -68.64) * mm, "end": v(86.05, -66.5) * mm});
            skLineSegment(sketch, "E39.8.5", {"start": v(84.25, -67.06) * mm, "end": v(86.05, -66.5) * mm});
            skLineSegment(sketch, "E39.8.6", {"start": v(88.9, -68.64) * mm, "end": v(83.45, -75.17) * mm});
            skLineSegment(sketch, "E39.8.7", {"start": v(83.45, -75.17) * mm, "end": v(80.84, -72.75) * mm});
            skLineSegment(sketch, "E39.8.8", {"start": v(88.9, -68.64) * mm, "end": v(86.05, -66.5) * mm});
            skLineSegment(sketch, "E39.8.9", {"start": v(88.9, -68.64) * mm, "end": v(86.05, -66.5) * mm});
            skLineSegment(sketch, "E39.8.10", {"start": v(83.45, -75.17) * mm, "end": v(80.84, -72.75) * mm});
            skLineSegment(sketch, "E39.9.0", {"start": v(90.74, -66.19) * mm, "end": v(87.9, -64.05) * mm});
            skLineSegment(sketch, "E39.9.1", {"start": v(90.74, -66.19) * mm, "end": v(95.49, -59.14) * mm});
            skLineSegment(sketch, "E39.9.2", {"start": v(87.9, -64.05) * mm, "end": v(88.16, -61.81) * mm});
            skLineSegment(sketch, "E39.9.3", {"start": v(88.16, -61.81) * mm, "end": v(90.7, -58.04) * mm});
            skLineSegment(sketch, "E39.9.4", {"start": v(95.49, -59.14) * mm, "end": v(92.43, -57.3) * mm});
            skLineSegment(sketch, "E39.9.5", {"start": v(90.7, -58.04) * mm, "end": v(92.43, -57.3) * mm});
            skLineSegment(sketch, "E39.9.6", {"start": v(95.49, -59.14) * mm, "end": v(90.74, -66.19) * mm});
            skLineSegment(sketch, "E39.9.7", {"start": v(90.74, -66.19) * mm, "end": v(87.9, -64.05) * mm});
            skLineSegment(sketch, "E39.9.8", {"start": v(95.49, -59.14) * mm, "end": v(92.43, -57.3) * mm});
            skLineSegment(sketch, "E39.9.9", {"start": v(95.49, -59.14) * mm, "end": v(92.43, -57.3) * mm});
            skLineSegment(sketch, "E39.9.10", {"start": v(90.74, -66.19) * mm, "end": v(87.9, -64.05) * mm});
            skLineSegment(sketch, "E39.10.0", {"start": v(97.07, -56.5) * mm, "end": v(94.01, -54.67) * mm});
            skLineSegment(sketch, "E39.10.1", {"start": v(97.07, -56.5) * mm, "end": v(101.06, -49) * mm});
            skLineSegment(sketch, "E39.10.2", {"start": v(94.01, -54.67) * mm, "end": v(94.05, -52.42) * mm});
            skLineSegment(sketch, "E39.10.3", {"start": v(94.05, -52.42) * mm, "end": v(96.19, -48.4) * mm});
            skLineSegment(sketch, "E39.10.4", {"start": v(101.06, -49) * mm, "end": v(97.84, -47.5) * mm});
            skLineSegment(sketch, "E39.10.5", {"start": v(96.19, -48.4) * mm, "end": v(97.84, -47.5) * mm});
            skLineSegment(sketch, "E39.10.6", {"start": v(101.06, -49) * mm, "end": v(97.07, -56.5) * mm});
            skLineSegment(sketch, "E39.10.7", {"start": v(97.07, -56.5) * mm, "end": v(94.01, -54.67) * mm});
            skLineSegment(sketch, "E39.10.8", {"start": v(101.06, -49) * mm, "end": v(97.84, -47.5) * mm});
            skLineSegment(sketch, "E39.10.9", {"start": v(101.06, -49) * mm, "end": v(97.84, -47.5) * mm});
            skLineSegment(sketch, "E39.10.10", {"start": v(97.07, -56.5) * mm, "end": v(94.01, -54.67) * mm});
            skLineSegment(sketch, "E39.11.0", {"start": v(102.36, -46.23) * mm, "end": v(99.14, -44.72) * mm});
            skLineSegment(sketch, "E39.11.1", {"start": v(102.36, -46.23) * mm, "end": v(105.56, -38.35) * mm});
            skLineSegment(sketch, "E39.11.2", {"start": v(99.14, -44.72) * mm, "end": v(98.94, -42.47) * mm});
            skLineSegment(sketch, "E39.11.3", {"start": v(98.94, -42.47) * mm, "end": v(100.66, -38.26) * mm});
            skLineSegment(sketch, "E39.11.4", {"start": v(105.56, -38.35) * mm, "end": v(102.2, -37.18) * mm});
            skLineSegment(sketch, "E39.11.5", {"start": v(100.66, -38.26) * mm, "end": v(102.2, -37.18) * mm});
            skLineSegment(sketch, "E39.11.6", {"start": v(105.56, -38.35) * mm, "end": v(102.36, -46.23) * mm});
            skLineSegment(sketch, "E39.11.7", {"start": v(102.36, -46.23) * mm, "end": v(99.14, -44.72) * mm});
            skLineSegment(sketch, "E39.11.8", {"start": v(105.56, -38.35) * mm, "end": v(102.2, -37.18) * mm});
            skLineSegment(sketch, "E39.11.9", {"start": v(105.56, -38.35) * mm, "end": v(102.2, -37.18) * mm});
            skLineSegment(sketch, "E39.11.10", {"start": v(102.36, -46.23) * mm, "end": v(99.14, -44.72) * mm});
            skLineSegment(sketch, "E39.12.0", {"start": v(106.57, -35.46) * mm, "end": v(103.2, -34.29) * mm});
            skLineSegment(sketch, "E39.12.1", {"start": v(106.57, -35.46) * mm, "end": v(108.95, -27.3) * mm});
            skLineSegment(sketch, "E39.12.2", {"start": v(103.2, -34.29) * mm, "end": v(102.78, -32.07) * mm});
            skLineSegment(sketch, "E39.12.3", {"start": v(102.78, -32.07) * mm, "end": v(104.06, -27.7) * mm});
            skLineSegment(sketch, "E39.12.4", {"start": v(108.95, -27.3) * mm, "end": v(105.48, -26.48) * mm});
            skLineSegment(sketch, "E39.12.5", {"start": v(104.06, -27.7) * mm, "end": v(105.48, -26.48) * mm});
            skLineSegment(sketch, "E39.12.6", {"start": v(108.95, -27.3) * mm, "end": v(106.57, -35.46) * mm});
            skLineSegment(sketch, "E39.12.7", {"start": v(106.57, -35.46) * mm, "end": v(103.2, -34.29) * mm});
            skLineSegment(sketch, "E39.12.8", {"start": v(108.95, -27.3) * mm, "end": v(105.48, -26.48) * mm});
            skLineSegment(sketch, "E39.12.9", {"start": v(108.95, -27.3) * mm, "end": v(105.48, -26.48) * mm});
            skLineSegment(sketch, "E39.12.10", {"start": v(106.57, -35.46) * mm, "end": v(103.2, -34.29) * mm});
            skLineSegment(sketch, "E39.13.0", {"start": v(109.65, -24.31) * mm, "end": v(106.19, -23.5) * mm});
            skLineSegment(sketch, "E39.13.1", {"start": v(109.65, -24.31) * mm, "end": v(111.18, -15.95) * mm});
            skLineSegment(sketch, "E39.13.2", {"start": v(106.19, -23.5) * mm, "end": v(105.54, -21.34) * mm});
            skLineSegment(sketch, "E39.13.3", {"start": v(105.54, -21.34) * mm, "end": v(106.35, -16.86) * mm});
            skLineSegment(sketch, "E39.13.4", {"start": v(111.18, -15.95) * mm, "end": v(107.65, -15.5) * mm});
            skLineSegment(sketch, "E39.13.5", {"start": v(106.35, -16.86) * mm, "end": v(107.65, -15.5) * mm});
            skLineSegment(sketch, "E39.13.6", {"start": v(111.18, -15.95) * mm, "end": v(109.65, -24.31) * mm});
            skLineSegment(sketch, "E39.13.7", {"start": v(109.65, -24.31) * mm, "end": v(106.19, -23.5) * mm});
            skLineSegment(sketch, "E39.13.8", {"start": v(111.18, -15.95) * mm, "end": v(107.65, -15.5) * mm});
            skLineSegment(sketch, "E39.13.9", {"start": v(111.18, -15.95) * mm, "end": v(107.65, -15.5) * mm});
            skLineSegment(sketch, "E39.13.10", {"start": v(109.65, -24.31) * mm, "end": v(106.19, -23.5) * mm});
            skLineSegment(sketch, "E39.14.0", {"start": v(111.57, -12.9) * mm, "end": v(108.04, -12.45) * mm});
            skLineSegment(sketch, "E39.14.1", {"start": v(111.57, -12.9) * mm, "end": v(112.23, -4.43) * mm});
            skLineSegment(sketch, "E39.14.2", {"start": v(108.04, -12.45) * mm, "end": v(107.17, -10.37) * mm});
            skLineSegment(sketch, "E39.14.3", {"start": v(107.17, -10.37) * mm, "end": v(107.52, -5.84) * mm});
            skLineSegment(sketch, "E39.14.4", {"start": v(112.23, -4.43) * mm, "end": v(108.67, -4.34) * mm});
            skLineSegment(sketch, "E39.14.5", {"start": v(107.52, -5.84) * mm, "end": v(108.67, -4.34) * mm});
            skLineSegment(sketch, "E39.14.6", {"start": v(112.23, -4.43) * mm, "end": v(111.57, -12.9) * mm});
            skLineSegment(sketch, "E39.14.7", {"start": v(111.57, -12.9) * mm, "end": v(108.04, -12.45) * mm});
            skLineSegment(sketch, "E39.14.8", {"start": v(112.23, -4.43) * mm, "end": v(108.67, -4.34) * mm});
            skLineSegment(sketch, "E39.14.9", {"start": v(112.23, -4.43) * mm, "end": v(108.67, -4.34) * mm});
            skLineSegment(sketch, "E39.14.10", {"start": v(111.57, -12.9) * mm, "end": v(108.04, -12.45) * mm});
            skLineSegment(sketch, "E39.15.0", {"start": v(112.3, -1.37) * mm, "end": v(108.75, -1.28) * mm});
            skLineSegment(sketch, "E39.15.1", {"start": v(112.3, -1.37) * mm, "end": v(112.09, 7.13) * mm});
            skLineSegment(sketch, "E39.15.2", {"start": v(108.75, -1.28) * mm, "end": v(107.67, 0.7) * mm});
            skLineSegment(sketch, "E39.15.3", {"start": v(107.67, 0.7) * mm, "end": v(107.55, 5.25) * mm});
            skLineSegment(sketch, "E39.15.4", {"start": v(112.09, 7.13) * mm, "end": v(108.54, 6.86) * mm});
            skLineSegment(sketch, "E39.15.5", {"start": v(107.55, 5.25) * mm, "end": v(108.54, 6.86) * mm});
            skLineSegment(sketch, "E39.15.6", {"start": v(112.09, 7.13) * mm, "end": v(112.3, -1.37) * mm});
            skLineSegment(sketch, "E39.15.7", {"start": v(112.3, -1.37) * mm, "end": v(108.75, -1.28) * mm});
            skLineSegment(sketch, "E39.15.8", {"start": v(112.09, 7.13) * mm, "end": v(108.54, 6.86) * mm});
            skLineSegment(sketch, "E39.15.9", {"start": v(112.09, 7.13) * mm, "end": v(108.54, 6.86) * mm});
            skLineSegment(sketch, "E39.15.10", {"start": v(112.3, -1.37) * mm, "end": v(108.75, -1.28) * mm});
            skLineSegment(sketch, "E39.16.0", {"start": v(111.85, 10.19) * mm, "end": v(108.3, 9.91) * mm});
            skLineSegment(sketch, "E39.16.1", {"start": v(111.85, 10.19) * mm, "end": v(110.76, 18.62) * mm});
            skLineSegment(sketch, "E39.16.2", {"start": v(108.3, 9.91) * mm, "end": v(107.03, 11.77) * mm});
            skLineSegment(sketch, "E39.16.3", {"start": v(107.03, 11.77) * mm, "end": v(106.44, 16.28) * mm});
            skLineSegment(sketch, "E39.16.4", {"start": v(110.76, 18.62) * mm, "end": v(107.26, 17.98) * mm});
            skLineSegment(sketch, "E39.16.5", {"start": v(106.44, 16.28) * mm, "end": v(107.26, 17.98) * mm});
            skLineSegment(sketch, "E39.16.6", {"start": v(110.76, 18.62) * mm, "end": v(111.85, 10.19) * mm});
            skLineSegment(sketch, "E39.16.7", {"start": v(111.85, 10.19) * mm, "end": v(108.3, 9.91) * mm});
            skLineSegment(sketch, "E39.16.8", {"start": v(110.76, 18.62) * mm, "end": v(107.26, 17.98) * mm});
            skLineSegment(sketch, "E39.16.9", {"start": v(110.76, 18.62) * mm, "end": v(107.26, 17.98) * mm});
            skLineSegment(sketch, "E39.16.10", {"start": v(111.85, 10.19) * mm, "end": v(108.3, 9.91) * mm});
            skLineSegment(sketch, "E39.17.0", {"start": v(110.21, 21.63) * mm, "end": v(106.7, 21) * mm});
            skLineSegment(sketch, "E39.17.1", {"start": v(110.21, 21.63) * mm, "end": v(108.26, 29.9) * mm});
            skLineSegment(sketch, "E39.17.2", {"start": v(106.7, 21) * mm, "end": v(105.25, 22.71) * mm});
            skLineSegment(sketch, "E39.17.3", {"start": v(105.25, 22.71) * mm, "end": v(104.2, 27.14) * mm});
            skLineSegment(sketch, "E39.17.4", {"start": v(108.26, 29.9) * mm, "end": v(104.84, 28.91) * mm});
            skLineSegment(sketch, "E39.17.5", {"start": v(104.2, 27.14) * mm, "end": v(104.84, 28.91) * mm});
            skLineSegment(sketch, "E39.17.6", {"start": v(108.26, 29.9) * mm, "end": v(110.21, 21.63) * mm});
            skLineSegment(sketch, "E39.17.7", {"start": v(110.21, 21.63) * mm, "end": v(106.7, 21) * mm});
            skLineSegment(sketch, "E39.17.8", {"start": v(108.26, 29.9) * mm, "end": v(104.84, 28.91) * mm});
            skLineSegment(sketch, "E39.17.9", {"start": v(108.26, 29.9) * mm, "end": v(104.84, 28.91) * mm});
            skLineSegment(sketch, "E39.17.10", {"start": v(110.21, 21.63) * mm, "end": v(106.7, 21) * mm});
            skLineSegment(sketch, "E39.18.0", {"start": v(107.4, 32.85) * mm, "end": v(103.98, 31.86) * mm});
            skLineSegment(sketch, "E39.18.1", {"start": v(107.4, 32.85) * mm, "end": v(104.61, 40.88) * mm});
            skLineSegment(sketch, "E39.18.2", {"start": v(103.98, 31.86) * mm, "end": v(102.36, 33.41) * mm});
            skLineSegment(sketch, "E39.18.3", {"start": v(102.36, 33.41) * mm, "end": v(100.86, 37.7) * mm});
            skLineSegment(sketch, "E39.18.4", {"start": v(104.61, 40.88) * mm, "end": v(101.31, 39.54) * mm});
            skLineSegment(sketch, "E39.18.5", {"start": v(100.86, 37.7) * mm, "end": v(101.31, 39.54) * mm});
            skLineSegment(sketch, "E39.18.6", {"start": v(104.61, 40.88) * mm, "end": v(107.4, 32.85) * mm});
            skLineSegment(sketch, "E39.18.7", {"start": v(107.4, 32.85) * mm, "end": v(103.98, 31.86) * mm});
            skLineSegment(sketch, "E39.18.8", {"start": v(104.61, 40.88) * mm, "end": v(101.31, 39.54) * mm});
            skLineSegment(sketch, "E39.18.9", {"start": v(104.61, 40.88) * mm, "end": v(101.31, 39.54) * mm});
            skLineSegment(sketch, "E39.18.10", {"start": v(107.4, 32.85) * mm, "end": v(103.98, 31.86) * mm});
            skLineSegment(sketch, "E39.19.0", {"start": v(103.46, 43.72) * mm, "end": v(100.16, 42.38) * mm});
            skLineSegment(sketch, "E39.19.1", {"start": v(103.46, 43.72) * mm, "end": v(99.85, 51.42) * mm});
            skLineSegment(sketch, "E39.19.2", {"start": v(100.16, 42.38) * mm, "end": v(98.38, 43.76) * mm});
            skLineSegment(sketch, "E39.19.3", {"start": v(98.38, 43.76) * mm, "end": v(96.45, 47.88) * mm});
            skLineSegment(sketch, "E39.19.4", {"start": v(99.85, 51.42) * mm, "end": v(96.71, 49.75) * mm});
            skLineSegment(sketch, "E39.19.5", {"start": v(96.45, 47.88) * mm, "end": v(96.71, 49.75) * mm});
            skLineSegment(sketch, "E39.19.6", {"start": v(99.85, 51.42) * mm, "end": v(103.46, 43.72) * mm});
            skLineSegment(sketch, "E39.19.7", {"start": v(103.46, 43.72) * mm, "end": v(100.16, 42.38) * mm});
            skLineSegment(sketch, "E39.19.8", {"start": v(99.85, 51.42) * mm, "end": v(96.71, 49.75) * mm});
            skLineSegment(sketch, "E39.19.9", {"start": v(99.85, 51.42) * mm, "end": v(96.71, 49.75) * mm});
            skLineSegment(sketch, "E39.19.10", {"start": v(103.46, 43.72) * mm, "end": v(100.16, 42.38) * mm});
            skLineSegment(sketch, "E39.20.0", {"start": v(98.41, 54.13) * mm, "end": v(95.27, 52.45) * mm});
            skLineSegment(sketch, "E39.20.1", {"start": v(98.41, 54.13) * mm, "end": v(94.04, 61.41) * mm});
            skLineSegment(sketch, "E39.20.2", {"start": v(95.27, 52.45) * mm, "end": v(93.36, 53.65) * mm});
            skLineSegment(sketch, "E39.20.3", {"start": v(93.36, 53.65) * mm, "end": v(91.02, 57.54) * mm});
            skLineSegment(sketch, "E39.20.4", {"start": v(94.04, 61.41) * mm, "end": v(91.08, 59.43) * mm});
            skLineSegment(sketch, "E39.20.5", {"start": v(91.02, 57.54) * mm, "end": v(91.08, 59.43) * mm});
            skLineSegment(sketch, "E39.20.6", {"start": v(94.04, 61.41) * mm, "end": v(98.41, 54.13) * mm});
            skLineSegment(sketch, "E39.20.7", {"start": v(98.41, 54.13) * mm, "end": v(95.27, 52.45) * mm});
            skLineSegment(sketch, "E39.20.8", {"start": v(94.04, 61.41) * mm, "end": v(91.08, 59.43) * mm});
            skLineSegment(sketch, "E39.20.9", {"start": v(94.04, 61.41) * mm, "end": v(91.08, 59.43) * mm});
            skLineSegment(sketch, "E39.20.10", {"start": v(98.41, 54.13) * mm, "end": v(95.27, 52.45) * mm});
            skLineSegment(sketch, "E39.21.0", {"start": v(92.33, 63.96) * mm, "end": v(89.37, 61.97) * mm});
            skLineSegment(sketch, "E39.21.1", {"start": v(92.33, 63.96) * mm, "end": v(87.23, 70.76) * mm});
            skLineSegment(sketch, "E39.21.2", {"start": v(89.37, 61.97) * mm, "end": v(87.35, 62.96) * mm});
            skLineSegment(sketch, "E39.21.3", {"start": v(87.35, 62.96) * mm, "end": v(84.62, 66.6) * mm});
            skLineSegment(sketch, "E39.21.4", {"start": v(87.23, 70.76) * mm, "end": v(84.49, 68.48) * mm});
            skLineSegment(sketch, "E39.21.5", {"start": v(84.62, 66.6) * mm, "end": v(84.49, 68.48) * mm});
            skLineSegment(sketch, "E39.21.6", {"start": v(87.23, 70.76) * mm, "end": v(92.33, 63.96) * mm});
            skLineSegment(sketch, "E39.21.7", {"start": v(92.33, 63.96) * mm, "end": v(89.37, 61.97) * mm});
            skLineSegment(sketch, "E39.21.8", {"start": v(87.23, 70.76) * mm, "end": v(84.49, 68.48) * mm});
            skLineSegment(sketch, "E39.21.9", {"start": v(87.23, 70.76) * mm, "end": v(84.49, 68.48) * mm});
            skLineSegment(sketch, "E39.21.10", {"start": v(92.33, 63.96) * mm, "end": v(89.37, 61.97) * mm});
            skLineSegment(sketch, "E39.22.0", {"start": v(85.26, 73.11) * mm, "end": v(82.53, 70.83) * mm});
            skLineSegment(sketch, "E39.22.1", {"start": v(85.26, 73.11) * mm, "end": v(79.49, 79.35) * mm});
            skLineSegment(sketch, "E39.22.2", {"start": v(82.53, 70.83) * mm, "end": v(80.41, 71.6) * mm});
            skLineSegment(sketch, "E39.22.3", {"start": v(80.41, 71.6) * mm, "end": v(77.32, 74.94) * mm});
            skLineSegment(sketch, "E39.22.4", {"start": v(79.49, 79.35) * mm, "end": v(77, 76.8) * mm});
            skLineSegment(sketch, "E39.22.5", {"start": v(77.32, 74.94) * mm, "end": v(77, 76.8) * mm});
            skLineSegment(sketch, "E39.22.6", {"start": v(79.49, 79.35) * mm, "end": v(85.26, 73.11) * mm});
            skLineSegment(sketch, "E39.22.7", {"start": v(85.26, 73.11) * mm, "end": v(82.53, 70.83) * mm});
            skLineSegment(sketch, "E39.22.8", {"start": v(79.49, 79.35) * mm, "end": v(77, 76.8) * mm});
            skLineSegment(sketch, "E39.22.9", {"start": v(79.49, 79.35) * mm, "end": v(77, 76.8) * mm});
            skLineSegment(sketch, "E39.22.10", {"start": v(85.26, 73.11) * mm, "end": v(82.53, 70.83) * mm});
            skLineSegment(sketch, "E39.23.0", {"start": v(77.3, 81.5) * mm, "end": v(74.8, 78.94) * mm});
            skLineSegment(sketch, "E39.23.1", {"start": v(77.3, 81.5) * mm, "end": v(70.9, 87.1) * mm});
            skLineSegment(sketch, "E39.23.2", {"start": v(74.8, 78.94) * mm, "end": v(72.62, 79.5) * mm});
            skLineSegment(sketch, "E39.23.3", {"start": v(72.62, 79.5) * mm, "end": v(69.2, 82.5) * mm});
            skLineSegment(sketch, "E39.23.4", {"start": v(70.9, 87.1) * mm, "end": v(68.7, 84.31) * mm});
            skLineSegment(sketch, "E39.23.5", {"start": v(69.2, 82.5) * mm, "end": v(68.7, 84.31) * mm});
            skLineSegment(sketch, "E39.23.6", {"start": v(70.9, 87.1) * mm, "end": v(77.3, 81.5) * mm});
            skLineSegment(sketch, "E39.23.7", {"start": v(77.3, 81.5) * mm, "end": v(74.8, 78.94) * mm});
            skLineSegment(sketch, "E39.23.8", {"start": v(70.9, 87.1) * mm, "end": v(68.7, 84.31) * mm});
            skLineSegment(sketch, "E39.23.9", {"start": v(70.9, 87.1) * mm, "end": v(68.7, 84.31) * mm});
            skLineSegment(sketch, "E39.23.10", {"start": v(77.3, 81.5) * mm, "end": v(74.8, 78.94) * mm});
            skLineSegment(sketch, "E39.24.0", {"start": v(68.5, 89) * mm, "end": v(66.3, 86.21) * mm});
            skLineSegment(sketch, "E39.24.1", {"start": v(68.5, 89) * mm, "end": v(61.58, 93.93) * mm});
            skLineSegment(sketch, "E39.24.2", {"start": v(66.3, 86.21) * mm, "end": v(64.06, 86.54) * mm});
            skLineSegment(sketch, "E39.24.3", {"start": v(64.06, 86.54) * mm, "end": v(60.36, 89.18) * mm});
            skLineSegment(sketch, "E39.24.4", {"start": v(61.58, 93.93) * mm, "end": v(59.66, 90.93) * mm});
            skLineSegment(sketch, "E39.24.5", {"start": v(60.36, 89.18) * mm, "end": v(59.66, 90.93) * mm});
            skLineSegment(sketch, "E39.24.6", {"start": v(61.58, 93.93) * mm, "end": v(68.5, 89) * mm});
            skLineSegment(sketch, "E39.24.7", {"start": v(68.5, 89) * mm, "end": v(66.3, 86.21) * mm});
            skLineSegment(sketch, "E39.24.8", {"start": v(61.58, 93.93) * mm, "end": v(59.66, 90.93) * mm});
            skLineSegment(sketch, "E39.24.9", {"start": v(61.58, 93.93) * mm, "end": v(59.66, 90.93) * mm});
            skLineSegment(sketch, "E39.24.10", {"start": v(68.5, 89) * mm, "end": v(66.3, 86.21) * mm});
            skLineSegment(sketch, "E39.25.0", {"start": v(58.99, 95.58) * mm, "end": v(57.08, 92.57) * mm});
            skLineSegment(sketch, "E39.25.1", {"start": v(58.99, 95.58) * mm, "end": v(51.6, 99.77) * mm});
            skLineSegment(sketch, "E39.25.2", {"start": v(57.08, 92.57) * mm, "end": v(54.83, 92.67) * mm});
            skLineSegment(sketch, "E39.25.3", {"start": v(54.83, 92.67) * mm, "end": v(50.87, 94.9) * mm});
            skLineSegment(sketch, "E39.25.4", {"start": v(51.6, 99.77) * mm, "end": v(50, 96.58) * mm});
            skLineSegment(sketch, "E39.25.5", {"start": v(50.87, 94.9) * mm, "end": v(50, 96.58) * mm});
            skLineSegment(sketch, "E39.25.6", {"start": v(51.6, 99.77) * mm, "end": v(58.99, 95.58) * mm});
            skLineSegment(sketch, "E39.25.7", {"start": v(58.99, 95.58) * mm, "end": v(57.08, 92.57) * mm});
            skLineSegment(sketch, "E39.25.8", {"start": v(51.6, 99.77) * mm, "end": v(50, 96.58) * mm});
            skLineSegment(sketch, "E39.25.9", {"start": v(51.6, 99.77) * mm, "end": v(50, 96.58) * mm});
            skLineSegment(sketch, "E39.25.10", {"start": v(58.99, 95.58) * mm, "end": v(57.08, 92.57) * mm});
            skLineSegment(sketch, "E39.26.0", {"start": v(48.85, 101.14) * mm, "end": v(47.26, 97.95) * mm});
            skLineSegment(sketch, "E39.26.1", {"start": v(48.85, 101.14) * mm, "end": v(41.06, 104.54) * mm});
            skLineSegment(sketch, "E39.26.2", {"start": v(47.26, 97.95) * mm, "end": v(45, 97.82) * mm});
            skLineSegment(sketch, "E39.26.3", {"start": v(45, 97.82) * mm, "end": v(40.84, 99.64) * mm});
            skLineSegment(sketch, "E39.26.4", {"start": v(41.06, 104.54) * mm, "end": v(39.8, 101.2) * mm});
            skLineSegment(sketch, "E39.26.5", {"start": v(40.84, 99.64) * mm, "end": v(39.8, 101.2) * mm});
            skLineSegment(sketch, "E39.26.6", {"start": v(41.06, 104.54) * mm, "end": v(48.85, 101.14) * mm});
            skLineSegment(sketch, "E39.26.7", {"start": v(48.85, 101.14) * mm, "end": v(47.26, 97.95) * mm});
            skLineSegment(sketch, "E39.26.8", {"start": v(41.06, 104.54) * mm, "end": v(39.8, 101.2) * mm});
            skLineSegment(sketch, "E39.26.9", {"start": v(41.06, 104.54) * mm, "end": v(39.8, 101.2) * mm});
            skLineSegment(sketch, "E39.26.10", {"start": v(48.85, 101.14) * mm, "end": v(47.26, 97.95) * mm});
            skLineSegment(sketch, "E39.27.0", {"start": v(38.2, 105.62) * mm, "end": v(36.93, 102.3) * mm});
            skLineSegment(sketch, "E39.27.1", {"start": v(38.2, 105.62) * mm, "end": v(30.1, 108.21) * mm});
            skLineSegment(sketch, "E39.27.2", {"start": v(36.93, 102.3) * mm, "end": v(34.7, 101.93) * mm});
            skLineSegment(sketch, "E39.27.3", {"start": v(34.7, 101.93) * mm, "end": v(30.38, 103.3) * mm});
            skLineSegment(sketch, "E39.27.4", {"start": v(30.1, 108.21) * mm, "end": v(29.18, 104.77) * mm});
            skLineSegment(sketch, "E39.27.5", {"start": v(30.38, 103.3) * mm, "end": v(29.18, 104.77) * mm});
            skLineSegment(sketch, "E39.27.6", {"start": v(30.1, 108.21) * mm, "end": v(38.2, 105.62) * mm});
            skLineSegment(sketch, "E39.27.7", {"start": v(38.2, 105.62) * mm, "end": v(36.93, 102.3) * mm});
            skLineSegment(sketch, "E39.27.8", {"start": v(30.1, 108.21) * mm, "end": v(29.18, 104.77) * mm});
            skLineSegment(sketch, "E39.27.9", {"start": v(30.1, 108.21) * mm, "end": v(29.18, 104.77) * mm});
            skLineSegment(sketch, "E39.27.10", {"start": v(38.2, 105.62) * mm, "end": v(36.93, 102.3) * mm});
            skLineSegment(sketch, "E39.28.0", {"start": v(27.13, 109) * mm, "end": v(26.22, 105.55) * mm});
            skLineSegment(sketch, "E39.28.1", {"start": v(27.13, 109) * mm, "end": v(18.8, 110.73) * mm});
            skLineSegment(sketch, "E39.28.2", {"start": v(26.22, 105.55) * mm, "end": v(24.05, 104.95) * mm});
            skLineSegment(sketch, "E39.28.3", {"start": v(24.05, 104.95) * mm, "end": v(19.6, 105.88) * mm});
            skLineSegment(sketch, "E39.28.4", {"start": v(18.8, 110.73) * mm, "end": v(18.26, 107.21) * mm});
            skLineSegment(sketch, "E39.28.5", {"start": v(19.6, 105.88) * mm, "end": v(18.26, 107.21) * mm});
            skLineSegment(sketch, "E39.28.6", {"start": v(18.8, 110.73) * mm, "end": v(27.13, 109) * mm});
            skLineSegment(sketch, "E39.28.7", {"start": v(27.13, 109) * mm, "end": v(26.22, 105.55) * mm});
            skLineSegment(sketch, "E39.28.8", {"start": v(18.8, 110.73) * mm, "end": v(18.26, 107.21) * mm});
            skLineSegment(sketch, "E39.28.9", {"start": v(18.8, 110.73) * mm, "end": v(18.26, 107.21) * mm});
            skLineSegment(sketch, "E39.28.10", {"start": v(27.13, 109) * mm, "end": v(26.22, 105.55) * mm});
            skLineSegment(sketch, "E39.29.0", {"start": v(15.78, 111.2) * mm, "end": v(15.23, 107.68) * mm});
            skLineSegment(sketch, "E39.29.1", {"start": v(15.78, 111.2) * mm, "end": v(7.32, 112.08) * mm});
            skLineSegment(sketch, "E39.29.2", {"start": v(15.23, 107.68) * mm, "end": v(13.13, 106.87) * mm});
            skLineSegment(sketch, "E39.29.3", {"start": v(13.13, 106.87) * mm, "end": v(8.6, 107.34) * mm});
            skLineSegment(sketch, "E39.29.4", {"start": v(7.32, 112.08) * mm, "end": v(7.14, 108.52) * mm});
            skLineSegment(sketch, "E39.29.5", {"start": v(8.6, 107.34) * mm, "end": v(7.14, 108.52) * mm});
            skLineSegment(sketch, "E39.29.6", {"start": v(7.32, 112.08) * mm, "end": v(15.78, 111.2) * mm});
            skLineSegment(sketch, "E39.29.7", {"start": v(15.78, 111.2) * mm, "end": v(15.23, 107.68) * mm});
            skLineSegment(sketch, "E39.29.8", {"start": v(7.32, 112.08) * mm, "end": v(7.14, 108.52) * mm});
            skLineSegment(sketch, "E39.29.9", {"start": v(7.32, 112.08) * mm, "end": v(7.14, 108.52) * mm});
            skLineSegment(sketch, "E39.29.10", {"start": v(15.78, 111.2) * mm, "end": v(15.23, 107.68) * mm});
            skLineSegment(sketch, "E39.30.0", {"start": v(4.26, 112.24) * mm, "end": v(4.08, 108.68) * mm});
            skLineSegment(sketch, "E39.30.1", {"start": v(4.26, 112.24) * mm, "end": v(-4.24, 112.24) * mm});
            skLineSegment(sketch, "E39.30.2", {"start": v(4.08, 108.68) * mm, "end": v(2.07, 107.65) * mm});
            skLineSegment(sketch, "E39.30.3", {"start": v(2.07, 107.65) * mm, "end": v(-2.48, 107.65) * mm});
            skLineSegment(sketch, "E39.30.4", {"start": v(-4.24, 112.24) * mm, "end": v(-4.06, 108.68) * mm});
            skLineSegment(sketch, "E39.30.5", {"start": v(-2.48, 107.65) * mm, "end": v(-4.06, 108.68) * mm});
            skLineSegment(sketch, "E39.30.6", {"start": v(-4.24, 112.24) * mm, "end": v(4.26, 112.24) * mm});
            skLineSegment(sketch, "E39.30.7", {"start": v(4.26, 112.24) * mm, "end": v(4.08, 108.68) * mm});
            skLineSegment(sketch, "E39.30.8", {"start": v(-4.24, 112.24) * mm, "end": v(-4.06, 108.68) * mm});
            skLineSegment(sketch, "E39.30.9", {"start": v(-4.24, 112.24) * mm, "end": v(-4.06, 108.68) * mm});
            skLineSegment(sketch, "E39.30.10", {"start": v(4.26, 112.24) * mm, "end": v(4.08, 108.68) * mm});
            skLineSegment(sketch, "E39.31.0", {"start": v(-7.3, 112.08) * mm, "end": v(-7.12, 108.52) * mm});
            skLineSegment(sketch, "E39.31.1", {"start": v(-7.3, 112.08) * mm, "end": v(-15.76, 111.2) * mm});
            skLineSegment(sketch, "E39.31.2", {"start": v(-7.12, 108.52) * mm, "end": v(-9.01, 107.3) * mm});
            skLineSegment(sketch, "E39.31.3", {"start": v(-9.01, 107.3) * mm, "end": v(-13.53, 106.83) * mm});
            skLineSegment(sketch, "E39.31.4", {"start": v(-15.76, 111.2) * mm, "end": v(-15.21, 107.69) * mm});
            skLineSegment(sketch, "E39.31.5", {"start": v(-13.53, 106.83) * mm, "end": v(-15.21, 107.69) * mm});
            skLineSegment(sketch, "E39.31.6", {"start": v(-15.76, 111.2) * mm, "end": v(-7.3, 112.08) * mm});
            skLineSegment(sketch, "E39.31.7", {"start": v(-7.3, 112.08) * mm, "end": v(-7.12, 108.52) * mm});
            skLineSegment(sketch, "E39.31.8", {"start": v(-15.76, 111.2) * mm, "end": v(-15.21, 107.69) * mm});
            skLineSegment(sketch, "E39.31.9", {"start": v(-15.76, 111.2) * mm, "end": v(-15.21, 107.69) * mm});
            skLineSegment(sketch, "E39.31.10", {"start": v(-7.3, 112.08) * mm, "end": v(-7.12, 108.52) * mm});
            skLineSegment(sketch, "E39.32.0", {"start": v(-18.79, 110.73) * mm, "end": v(-18.24, 107.21) * mm});
            skLineSegment(sketch, "E39.32.1", {"start": v(-18.79, 110.73) * mm, "end": v(-27.1, 109) * mm});
            skLineSegment(sketch, "E39.32.2", {"start": v(-18.24, 107.21) * mm, "end": v(-20, 105.8) * mm});
            skLineSegment(sketch, "E39.32.3", {"start": v(-20, 105.8) * mm, "end": v(-24.45, 104.87) * mm});
            skLineSegment(sketch, "E39.32.4", {"start": v(-27.1, 109) * mm, "end": v(-26.2, 105.55) * mm});
            skLineSegment(sketch, "E39.32.5", {"start": v(-24.45, 104.87) * mm, "end": v(-26.2, 105.55) * mm});
            skLineSegment(sketch, "E39.32.6", {"start": v(-27.1, 109) * mm, "end": v(-18.79, 110.73) * mm});
            skLineSegment(sketch, "E39.32.7", {"start": v(-18.79, 110.73) * mm, "end": v(-18.24, 107.21) * mm});
            skLineSegment(sketch, "E39.32.8", {"start": v(-27.1, 109) * mm, "end": v(-26.2, 105.55) * mm});
            skLineSegment(sketch, "E39.32.9", {"start": v(-27.1, 109) * mm, "end": v(-26.2, 105.55) * mm});
            skLineSegment(sketch, "E39.32.10", {"start": v(-18.79, 110.73) * mm, "end": v(-18.24, 107.21) * mm});
            skLineSegment(sketch, "E39.33.0", {"start": v(-30.07, 108.21) * mm, "end": v(-29.17, 104.77) * mm});
            skLineSegment(sketch, "E39.33.1", {"start": v(-30.07, 108.21) * mm, "end": v(-38.17, 105.63) * mm});
            skLineSegment(sketch, "E39.33.2", {"start": v(-29.17, 104.77) * mm, "end": v(-30.77, 103.18) * mm});
            skLineSegment(sketch, "E39.33.3", {"start": v(-30.77, 103.18) * mm, "end": v(-35.1, 101.8) * mm});
            skLineSegment(sketch, "E39.33.4", {"start": v(-38.17, 105.63) * mm, "end": v(-36.92, 102.3) * mm});
            skLineSegment(sketch, "E39.33.5", {"start": v(-35.1, 101.8) * mm, "end": v(-36.92, 102.3) * mm});
            skLineSegment(sketch, "E39.33.6", {"start": v(-38.17, 105.63) * mm, "end": v(-30.07, 108.21) * mm});
            skLineSegment(sketch, "E39.33.7", {"start": v(-30.07, 108.21) * mm, "end": v(-29.17, 104.77) * mm});
            skLineSegment(sketch, "E39.33.8", {"start": v(-38.17, 105.63) * mm, "end": v(-36.92, 102.3) * mm});
            skLineSegment(sketch, "E39.33.9", {"start": v(-38.17, 105.63) * mm, "end": v(-36.92, 102.3) * mm});
            skLineSegment(sketch, "E39.33.10", {"start": v(-30.07, 108.21) * mm, "end": v(-29.17, 104.77) * mm});
            skLineSegment(sketch, "E39.34.0", {"start": v(-41.04, 104.55) * mm, "end": v(-39.79, 101.22) * mm});
            skLineSegment(sketch, "E39.34.1", {"start": v(-41.04, 104.55) * mm, "end": v(-48.83, 101.15) * mm});
            skLineSegment(sketch, "E39.34.2", {"start": v(-39.79, 101.22) * mm, "end": v(-41.21, 99.47) * mm});
            skLineSegment(sketch, "E39.34.3", {"start": v(-41.21, 99.47) * mm, "end": v(-45.38, 97.65) * mm});
            skLineSegment(sketch, "E39.34.4", {"start": v(-48.83, 101.15) * mm, "end": v(-47.24, 97.96) * mm});
            skLineSegment(sketch, "E39.34.5", {"start": v(-45.38, 97.65) * mm, "end": v(-47.24, 97.96) * mm});
            skLineSegment(sketch, "E39.34.6", {"start": v(-48.83, 101.15) * mm, "end": v(-41.04, 104.55) * mm});
            skLineSegment(sketch, "E39.34.7", {"start": v(-41.04, 104.55) * mm, "end": v(-39.79, 101.22) * mm});
            skLineSegment(sketch, "E39.34.8", {"start": v(-48.83, 101.15) * mm, "end": v(-47.24, 97.96) * mm});
            skLineSegment(sketch, "E39.34.9", {"start": v(-48.83, 101.15) * mm, "end": v(-47.24, 97.96) * mm});
            skLineSegment(sketch, "E39.34.10", {"start": v(-41.04, 104.55) * mm, "end": v(-39.79, 101.22) * mm});
            skLineSegment(sketch, "E39.35.0", {"start": v(-51.57, 99.77) * mm, "end": v(-49.98, 96.59) * mm});
            skLineSegment(sketch, "E39.35.1", {"start": v(-51.57, 99.77) * mm, "end": v(-58.97, 95.59) * mm});
            skLineSegment(sketch, "E39.35.2", {"start": v(-49.98, 96.59) * mm, "end": v(-51.22, 94.7) * mm});
            skLineSegment(sketch, "E39.35.3", {"start": v(-51.22, 94.7) * mm, "end": v(-55.18, 92.47) * mm});
            skLineSegment(sketch, "E39.35.4", {"start": v(-58.97, 95.59) * mm, "end": v(-57.06, 92.58) * mm});
            skLineSegment(sketch, "E39.35.5", {"start": v(-55.18, 92.47) * mm, "end": v(-57.06, 92.58) * mm});
            skLineSegment(sketch, "E39.35.6", {"start": v(-58.97, 95.59) * mm, "end": v(-51.57, 99.77) * mm});
            skLineSegment(sketch, "E39.35.7", {"start": v(-51.57, 99.77) * mm, "end": v(-49.98, 96.59) * mm});
            skLineSegment(sketch, "E39.35.8", {"start": v(-58.97, 95.59) * mm, "end": v(-57.06, 92.58) * mm});
            skLineSegment(sketch, "E39.35.9", {"start": v(-58.97, 95.59) * mm, "end": v(-57.06, 92.58) * mm});
            skLineSegment(sketch, "E39.35.10", {"start": v(-51.57, 99.77) * mm, "end": v(-49.98, 96.59) * mm});
            skLineSegment(sketch, "E39.36.0", {"start": v(-61.56, 93.94) * mm, "end": v(-59.65, 90.94) * mm});
            skLineSegment(sketch, "E39.36.1", {"start": v(-61.56, 93.94) * mm, "end": v(-68.49, 89.02) * mm});
            skLineSegment(sketch, "E39.36.2", {"start": v(-59.65, 90.94) * mm, "end": v(-60.7, 88.94) * mm});
            skLineSegment(sketch, "E39.36.3", {"start": v(-60.7, 88.94) * mm, "end": v(-64.4, 86.3) * mm});
            skLineSegment(sketch, "E39.36.4", {"start": v(-68.49, 89.02) * mm, "end": v(-66.28, 86.22) * mm});
            skLineSegment(sketch, "E39.36.5", {"start": v(-64.4, 86.3) * mm, "end": v(-66.28, 86.22) * mm});
            skLineSegment(sketch, "E39.36.6", {"start": v(-68.49, 89.02) * mm, "end": v(-61.56, 93.94) * mm});
            skLineSegment(sketch, "E39.36.7", {"start": v(-61.56, 93.94) * mm, "end": v(-59.65, 90.94) * mm});
            skLineSegment(sketch, "E39.36.8", {"start": v(-68.49, 89.02) * mm, "end": v(-66.28, 86.22) * mm});
            skLineSegment(sketch, "E39.36.9", {"start": v(-68.49, 89.02) * mm, "end": v(-66.28, 86.22) * mm});
            skLineSegment(sketch, "E39.36.10", {"start": v(-61.56, 93.94) * mm, "end": v(-59.65, 90.94) * mm});
            skLineSegment(sketch, "E39.37.0", {"start": v(-70.9, 87.12) * mm, "end": v(-68.68, 84.32) * mm});
            skLineSegment(sketch, "E39.37.1", {"start": v(-70.9, 87.12) * mm, "end": v(-77.28, 81.5) * mm});
            skLineSegment(sketch, "E39.37.2", {"start": v(-68.68, 84.32) * mm, "end": v(-69.51, 82.23) * mm});
            skLineSegment(sketch, "E39.37.3", {"start": v(-69.51, 82.23) * mm, "end": v(-72.93, 79.23) * mm});
            skLineSegment(sketch, "E39.37.4", {"start": v(-77.28, 81.5) * mm, "end": v(-74.8, 78.95) * mm});
            skLineSegment(sketch, "E39.37.5", {"start": v(-72.93, 79.23) * mm, "end": v(-74.8, 78.95) * mm});
            skLineSegment(sketch, "E39.37.6", {"start": v(-77.28, 81.5) * mm, "end": v(-70.9, 87.12) * mm});
            skLineSegment(sketch, "E39.37.7", {"start": v(-70.9, 87.12) * mm, "end": v(-68.68, 84.32) * mm});
            skLineSegment(sketch, "E39.37.8", {"start": v(-77.28, 81.5) * mm, "end": v(-74.8, 78.95) * mm});
            skLineSegment(sketch, "E39.37.9", {"start": v(-77.28, 81.5) * mm, "end": v(-74.8, 78.95) * mm});
            skLineSegment(sketch, "E39.37.10", {"start": v(-70.9, 87.12) * mm, "end": v(-68.68, 84.32) * mm});
            skLineSegment(sketch, "E39.38.0", {"start": v(-79.47, 79.36) * mm, "end": v(-76.99, 76.81) * mm});
            skLineSegment(sketch, "E39.38.1", {"start": v(-79.47, 79.36) * mm, "end": v(-85.25, 73.13) * mm});
            skLineSegment(sketch, "E39.38.2", {"start": v(-76.99, 76.81) * mm, "end": v(-77.6, 74.64) * mm});
            skLineSegment(sketch, "E39.38.3", {"start": v(-77.6, 74.64) * mm, "end": v(-80.69, 71.3) * mm});
            skLineSegment(sketch, "E39.38.4", {"start": v(-85.25, 73.13) * mm, "end": v(-82.51, 70.84) * mm});
            skLineSegment(sketch, "E39.38.5", {"start": v(-80.69, 71.3) * mm, "end": v(-82.51, 70.84) * mm});
            skLineSegment(sketch, "E39.38.6", {"start": v(-85.25, 73.13) * mm, "end": v(-79.47, 79.36) * mm});
            skLineSegment(sketch, "E39.38.7", {"start": v(-79.47, 79.36) * mm, "end": v(-76.99, 76.81) * mm});
            skLineSegment(sketch, "E39.38.8", {"start": v(-85.25, 73.13) * mm, "end": v(-82.51, 70.84) * mm});
            skLineSegment(sketch, "E39.38.9", {"start": v(-85.25, 73.13) * mm, "end": v(-82.51, 70.84) * mm});
            skLineSegment(sketch, "E39.38.10", {"start": v(-79.47, 79.36) * mm, "end": v(-76.99, 76.81) * mm});
            skLineSegment(sketch, "E39.39.0", {"start": v(-87.21, 70.77) * mm, "end": v(-84.48, 68.5) * mm});
            skLineSegment(sketch, "E39.39.1", {"start": v(-87.21, 70.77) * mm, "end": v(-92.32, 63.97) * mm});
            skLineSegment(sketch, "E39.39.2", {"start": v(-84.48, 68.5) * mm, "end": v(-84.86, 66.27) * mm});
            skLineSegment(sketch, "E39.39.3", {"start": v(-84.86, 66.27) * mm, "end": v(-87.6, 62.63) * mm});
            skLineSegment(sketch, "E39.39.4", {"start": v(-92.32, 63.97) * mm, "end": v(-89.36, 61.98) * mm});
            skLineSegment(sketch, "E39.39.5", {"start": v(-87.6, 62.63) * mm, "end": v(-89.36, 61.98) * mm});
            skLineSegment(sketch, "E39.39.6", {"start": v(-92.32, 63.97) * mm, "end": v(-87.21, 70.77) * mm});
            skLineSegment(sketch, "E39.39.7", {"start": v(-87.21, 70.77) * mm, "end": v(-84.48, 68.5) * mm});
            skLineSegment(sketch, "E39.39.8", {"start": v(-92.32, 63.97) * mm, "end": v(-89.36, 61.98) * mm});
            skLineSegment(sketch, "E39.39.9", {"start": v(-92.32, 63.97) * mm, "end": v(-89.36, 61.98) * mm});
            skLineSegment(sketch, "E39.39.10", {"start": v(-87.21, 70.77) * mm, "end": v(-84.48, 68.5) * mm});
            skLineSegment(sketch, "E39.40.0", {"start": v(-94.03, 61.43) * mm, "end": v(-91.07, 59.44) * mm});
            skLineSegment(sketch, "E39.40.1", {"start": v(-94.03, 61.43) * mm, "end": v(-98.4, 54.14) * mm});
            skLineSegment(sketch, "E39.40.2", {"start": v(-91.07, 59.44) * mm, "end": v(-91.23, 57.2) * mm});
            skLineSegment(sketch, "E39.40.3", {"start": v(-91.23, 57.2) * mm, "end": v(-93.57, 53.3) * mm});
            skLineSegment(sketch, "E39.40.4", {"start": v(-98.4, 54.14) * mm, "end": v(-95.26, 52.47) * mm});
            skLineSegment(sketch, "E39.40.5", {"start": v(-93.57, 53.3) * mm, "end": v(-95.26, 52.47) * mm});
            skLineSegment(sketch, "E39.40.6", {"start": v(-98.4, 54.14) * mm, "end": v(-94.03, 61.43) * mm});
            skLineSegment(sketch, "E39.40.7", {"start": v(-94.03, 61.43) * mm, "end": v(-91.07, 59.44) * mm});
            skLineSegment(sketch, "E39.40.8", {"start": v(-98.4, 54.14) * mm, "end": v(-95.26, 52.47) * mm});
            skLineSegment(sketch, "E39.40.9", {"start": v(-98.4, 54.14) * mm, "end": v(-95.26, 52.47) * mm});
            skLineSegment(sketch, "E39.40.10", {"start": v(-94.03, 61.43) * mm, "end": v(-91.07, 59.44) * mm});
            skLineSegment(sketch, "E39.41.0", {"start": v(-99.85, 51.44) * mm, "end": v(-96.7, 49.76) * mm});
            skLineSegment(sketch, "E39.41.1", {"start": v(-99.85, 51.44) * mm, "end": v(-103.45, 43.74) * mm});
            skLineSegment(sketch, "E39.41.2", {"start": v(-96.7, 49.76) * mm, "end": v(-96.62, 47.5) * mm});
            skLineSegment(sketch, "E39.41.3", {"start": v(-96.62, 47.5) * mm, "end": v(-98.55, 43.4) * mm});
            skLineSegment(sketch, "E39.41.4", {"start": v(-103.45, 43.74) * mm, "end": v(-100.15, 42.4) * mm});
            skLineSegment(sketch, "E39.41.5", {"start": v(-98.55, 43.4) * mm, "end": v(-100.15, 42.4) * mm});
            skLineSegment(sketch, "E39.41.6", {"start": v(-103.45, 43.74) * mm, "end": v(-99.85, 51.44) * mm});
            skLineSegment(sketch, "E39.41.7", {"start": v(-99.85, 51.44) * mm, "end": v(-96.7, 49.76) * mm});
            skLineSegment(sketch, "E39.41.8", {"start": v(-103.45, 43.74) * mm, "end": v(-100.15, 42.4) * mm});
            skLineSegment(sketch, "E39.41.9", {"start": v(-103.45, 43.74) * mm, "end": v(-100.15, 42.4) * mm});
            skLineSegment(sketch, "E39.41.10", {"start": v(-99.85, 51.44) * mm, "end": v(-96.7, 49.76) * mm});
            skLineSegment(sketch, "E39.42.0", {"start": v(-104.6, 40.9) * mm, "end": v(-101.3, 39.56) * mm});
            skLineSegment(sketch, "E39.42.1", {"start": v(-104.6, 40.9) * mm, "end": v(-107.4, 32.87) * mm});
            skLineSegment(sketch, "E39.42.2", {"start": v(-101.3, 39.56) * mm, "end": v(-101, 37.32) * mm});
            skLineSegment(sketch, "E39.42.3", {"start": v(-101, 37.32) * mm, "end": v(-102.5, 33.03) * mm});
            skLineSegment(sketch, "E39.42.4", {"start": v(-107.4, 32.87) * mm, "end": v(-103.98, 31.87) * mm});
            skLineSegment(sketch, "E39.42.5", {"start": v(-102.5, 33.03) * mm, "end": v(-103.98, 31.87) * mm});
            skLineSegment(sketch, "E39.42.6", {"start": v(-107.4, 32.87) * mm, "end": v(-104.6, 40.9) * mm});
            skLineSegment(sketch, "E39.42.7", {"start": v(-104.6, 40.9) * mm, "end": v(-101.3, 39.56) * mm});
            skLineSegment(sketch, "E39.42.8", {"start": v(-107.4, 32.87) * mm, "end": v(-103.98, 31.87) * mm});
            skLineSegment(sketch, "E39.42.9", {"start": v(-107.4, 32.87) * mm, "end": v(-103.98, 31.87) * mm});
            skLineSegment(sketch, "E39.42.10", {"start": v(-104.6, 40.9) * mm, "end": v(-101.3, 39.56) * mm});
            skLineSegment(sketch, "E39.43.0", {"start": v(-108.26, 29.92) * mm, "end": v(-104.84, 28.93) * mm});
            skLineSegment(sketch, "E39.43.1", {"start": v(-108.26, 29.92) * mm, "end": v(-110.2, 21.65) * mm});
            skLineSegment(sketch, "E39.43.2", {"start": v(-104.84, 28.93) * mm, "end": v(-104.3, 26.74) * mm});
            skLineSegment(sketch, "E39.43.3", {"start": v(-104.3, 26.74) * mm, "end": v(-105.34, 22.32) * mm});
            skLineSegment(sketch, "E39.43.4", {"start": v(-110.2, 21.65) * mm, "end": v(-106.7, 21.01) * mm});
            skLineSegment(sketch, "E39.43.5", {"start": v(-105.34, 22.32) * mm, "end": v(-106.7, 21.01) * mm});
            skLineSegment(sketch, "E39.43.6", {"start": v(-110.2, 21.65) * mm, "end": v(-108.26, 29.92) * mm});
            skLineSegment(sketch, "E39.43.7", {"start": v(-108.26, 29.92) * mm, "end": v(-104.84, 28.93) * mm});
            skLineSegment(sketch, "E39.43.8", {"start": v(-110.2, 21.65) * mm, "end": v(-106.7, 21.01) * mm});
            skLineSegment(sketch, "E39.43.9", {"start": v(-110.2, 21.65) * mm, "end": v(-106.7, 21.01) * mm});
            skLineSegment(sketch, "E39.43.10", {"start": v(-108.26, 29.92) * mm, "end": v(-104.84, 28.93) * mm});
            skLineSegment(sketch, "E39.44.0", {"start": v(-110.76, 18.63) * mm, "end": v(-107.26, 18) * mm});
            skLineSegment(sketch, "E39.44.1", {"start": v(-110.76, 18.63) * mm, "end": v(-111.85, 10.2) * mm});
            skLineSegment(sketch, "E39.44.2", {"start": v(-107.26, 18) * mm, "end": v(-106.5, 15.87) * mm});
            skLineSegment(sketch, "E39.44.3", {"start": v(-106.5, 15.87) * mm, "end": v(-107.08, 11.37) * mm});
            skLineSegment(sketch, "E39.44.4", {"start": v(-111.85, 10.2) * mm, "end": v(-108.3, 9.93) * mm});
            skLineSegment(sketch, "E39.44.5", {"start": v(-107.08, 11.37) * mm, "end": v(-108.3, 9.93) * mm});
            skLineSegment(sketch, "E39.44.6", {"start": v(-111.85, 10.2) * mm, "end": v(-110.76, 18.63) * mm});
            skLineSegment(sketch, "E39.44.7", {"start": v(-110.76, 18.63) * mm, "end": v(-107.26, 18) * mm});
            skLineSegment(sketch, "E39.44.8", {"start": v(-111.85, 10.2) * mm, "end": v(-108.3, 9.93) * mm});
            skLineSegment(sketch, "E39.44.9", {"start": v(-111.85, 10.2) * mm, "end": v(-108.3, 9.93) * mm});
            skLineSegment(sketch, "E39.44.10", {"start": v(-110.76, 18.63) * mm, "end": v(-107.26, 18) * mm});
            skLineSegment(sketch, "E39.45.0", {"start": v(-112.09, 7.15) * mm, "end": v(-108.54, 6.87) * mm});
            skLineSegment(sketch, "E39.45.1", {"start": v(-112.09, 7.15) * mm, "end": v(-112.3, -1.35) * mm});
            skLineSegment(sketch, "E39.45.2", {"start": v(-108.54, 6.87) * mm, "end": v(-107.56, 4.84) * mm});
            skLineSegment(sketch, "E39.45.3", {"start": v(-107.56, 4.84) * mm, "end": v(-107.68, 0.3) * mm});
            skLineSegment(sketch, "E39.45.4", {"start": v(-112.3, -1.35) * mm, "end": v(-108.75, -1.26) * mm});
            skLineSegment(sketch, "E39.45.5", {"start": v(-107.68, 0.3) * mm, "end": v(-108.75, -1.26) * mm});
            skLineSegment(sketch, "E39.45.6", {"start": v(-112.3, -1.35) * mm, "end": v(-112.09, 7.15) * mm});
            skLineSegment(sketch, "E39.45.7", {"start": v(-112.09, 7.15) * mm, "end": v(-108.54, 6.87) * mm});
            skLineSegment(sketch, "E39.45.8", {"start": v(-112.3, -1.35) * mm, "end": v(-108.75, -1.26) * mm});
            skLineSegment(sketch, "E39.45.9", {"start": v(-112.3, -1.35) * mm, "end": v(-108.75, -1.26) * mm});
            skLineSegment(sketch, "E39.45.10", {"start": v(-112.09, 7.15) * mm, "end": v(-108.54, 6.87) * mm});
            skLineSegment(sketch, "E39.46.0", {"start": v(-112.23, -4.42) * mm, "end": v(-108.67, -4.32) * mm});
            skLineSegment(sketch, "E39.46.1", {"start": v(-112.23, -4.42) * mm, "end": v(-111.57, -12.9) * mm});
            skLineSegment(sketch, "E39.46.2", {"start": v(-108.67, -4.32) * mm, "end": v(-107.5, -6.25) * mm});
            skLineSegment(sketch, "E39.46.3", {"start": v(-107.5, -6.25) * mm, "end": v(-107.14, -10.78) * mm});
            skLineSegment(sketch, "E39.46.4", {"start": v(-111.57, -12.9) * mm, "end": v(-108.04, -12.43) * mm});
            skLineSegment(sketch, "E39.46.5", {"start": v(-107.14, -10.78) * mm, "end": v(-108.04, -12.43) * mm});
            skLineSegment(sketch, "E39.46.6", {"start": v(-111.57, -12.9) * mm, "end": v(-112.23, -4.42) * mm});
            skLineSegment(sketch, "E39.46.7", {"start": v(-112.23, -4.42) * mm, "end": v(-108.67, -4.32) * mm});
            skLineSegment(sketch, "E39.46.8", {"start": v(-111.57, -12.9) * mm, "end": v(-108.04, -12.43) * mm});
            skLineSegment(sketch, "E39.46.9", {"start": v(-111.57, -12.9) * mm, "end": v(-108.04, -12.43) * mm});
            skLineSegment(sketch, "E39.46.10", {"start": v(-112.23, -4.42) * mm, "end": v(-108.67, -4.32) * mm});
            skLineSegment(sketch, "E39.47.0", {"start": v(-111.18, -15.93) * mm, "end": v(-107.65, -15.47) * mm});
            skLineSegment(sketch, "E39.47.1", {"start": v(-111.18, -15.93) * mm, "end": v(-109.66, -24.3) * mm});
            skLineSegment(sketch, "E39.47.2", {"start": v(-107.65, -15.47) * mm, "end": v(-106.28, -17.26) * mm});
            skLineSegment(sketch, "E39.47.3", {"start": v(-106.28, -17.26) * mm, "end": v(-105.47, -21.74) * mm});
            skLineSegment(sketch, "E39.47.4", {"start": v(-109.66, -24.3) * mm, "end": v(-106.2, -23.48) * mm});
            skLineSegment(sketch, "E39.47.5", {"start": v(-105.47, -21.74) * mm, "end": v(-106.2, -23.48) * mm});
            skLineSegment(sketch, "E39.47.6", {"start": v(-109.66, -24.3) * mm, "end": v(-111.18, -15.93) * mm});
            skLineSegment(sketch, "E39.47.7", {"start": v(-111.18, -15.93) * mm, "end": v(-107.65, -15.47) * mm});
            skLineSegment(sketch, "E39.47.8", {"start": v(-109.66, -24.3) * mm, "end": v(-106.2, -23.48) * mm});
            skLineSegment(sketch, "E39.47.9", {"start": v(-109.66, -24.3) * mm, "end": v(-106.2, -23.48) * mm});
            skLineSegment(sketch, "E39.47.10", {"start": v(-111.18, -15.93) * mm, "end": v(-107.65, -15.47) * mm});
            skLineSegment(sketch, "E39.48.0", {"start": v(-108.95, -27.28) * mm, "end": v(-105.49, -26.46) * mm});
            skLineSegment(sketch, "E39.48.1", {"start": v(-108.95, -27.28) * mm, "end": v(-106.58, -35.44) * mm});
            skLineSegment(sketch, "E39.48.2", {"start": v(-105.49, -26.46) * mm, "end": v(-103.94, -28.1) * mm});
            skLineSegment(sketch, "E39.48.3", {"start": v(-103.94, -28.1) * mm, "end": v(-102.67, -32.47) * mm});
            skLineSegment(sketch, "E39.48.4", {"start": v(-106.58, -35.44) * mm, "end": v(-103.21, -34.27) * mm});
            skLineSegment(sketch, "E39.48.5", {"start": v(-102.67, -32.47) * mm, "end": v(-103.21, -34.27) * mm});
            skLineSegment(sketch, "E39.48.6", {"start": v(-106.58, -35.44) * mm, "end": v(-108.95, -27.28) * mm});
            skLineSegment(sketch, "E39.48.7", {"start": v(-108.95, -27.28) * mm, "end": v(-105.49, -26.46) * mm});
            skLineSegment(sketch, "E39.48.8", {"start": v(-106.58, -35.44) * mm, "end": v(-103.21, -34.27) * mm});
            skLineSegment(sketch, "E39.48.9", {"start": v(-106.58, -35.44) * mm, "end": v(-103.21, -34.27) * mm});
            skLineSegment(sketch, "E39.48.10", {"start": v(-108.95, -27.28) * mm, "end": v(-105.49, -26.46) * mm});
            skLineSegment(sketch, "E39.49.0", {"start": v(-105.57, -38.34) * mm, "end": v(-102.2, -37.17) * mm});
            skLineSegment(sketch, "E39.49.1", {"start": v(-105.57, -38.34) * mm, "end": v(-102.37, -46.21) * mm});
            skLineSegment(sketch, "E39.49.2", {"start": v(-102.2, -37.17) * mm, "end": v(-100.5, -38.64) * mm});
            skLineSegment(sketch, "E39.49.3", {"start": v(-100.5, -38.64) * mm, "end": v(-98.79, -42.85) * mm});
            skLineSegment(sketch, "E39.49.4", {"start": v(-102.37, -46.21) * mm, "end": v(-99.14, -44.7) * mm});
            skLineSegment(sketch, "E39.49.5", {"start": v(-98.79, -42.85) * mm, "end": v(-99.14, -44.7) * mm});
            skLineSegment(sketch, "E39.49.6", {"start": v(-102.37, -46.21) * mm, "end": v(-105.57, -38.34) * mm});
            skLineSegment(sketch, "E39.49.7", {"start": v(-105.57, -38.34) * mm, "end": v(-102.2, -37.17) * mm});
            skLineSegment(sketch, "E39.49.8", {"start": v(-102.37, -46.21) * mm, "end": v(-99.14, -44.7) * mm});
            skLineSegment(sketch, "E39.49.9", {"start": v(-102.37, -46.21) * mm, "end": v(-99.14, -44.7) * mm});
            skLineSegment(sketch, "E39.49.10", {"start": v(-105.57, -38.34) * mm, "end": v(-102.2, -37.17) * mm});
            skLineSegment(sketch, "E39.50.0", {"start": v(-101.07, -48.99) * mm, "end": v(-97.84, -47.48) * mm});
            skLineSegment(sketch, "E39.50.1", {"start": v(-101.07, -48.99) * mm, "end": v(-97.08, -56.5) * mm});
            skLineSegment(sketch, "E39.50.2", {"start": v(-97.84, -47.48) * mm, "end": v(-96, -48.77) * mm});
            skLineSegment(sketch, "E39.50.3", {"start": v(-96, -48.77) * mm, "end": v(-93.86, -52.78) * mm});
            skLineSegment(sketch, "E39.50.4", {"start": v(-97.08, -56.5) * mm, "end": v(-94.02, -54.66) * mm});
            skLineSegment(sketch, "E39.50.5", {"start": v(-93.86, -52.78) * mm, "end": v(-94.02, -54.66) * mm});
            skLineSegment(sketch, "E39.50.6", {"start": v(-97.08, -56.5) * mm, "end": v(-101.07, -48.99) * mm});
            skLineSegment(sketch, "E39.50.7", {"start": v(-101.07, -48.99) * mm, "end": v(-97.84, -47.48) * mm});
            skLineSegment(sketch, "E39.50.8", {"start": v(-97.08, -56.5) * mm, "end": v(-94.02, -54.66) * mm});
            skLineSegment(sketch, "E39.50.9", {"start": v(-97.08, -56.5) * mm, "end": v(-94.02, -54.66) * mm});
            skLineSegment(sketch, "E39.50.10", {"start": v(-101.07, -48.99) * mm, "end": v(-97.84, -47.48) * mm});
            skLineSegment(sketch, "E39.51.0", {"start": v(-95.5, -59.12) * mm, "end": v(-92.44, -57.29) * mm});
            skLineSegment(sketch, "E39.51.1", {"start": v(-95.5, -59.12) * mm, "end": v(-90.75, -66.17) * mm});
            skLineSegment(sketch, "E39.51.2", {"start": v(-92.44, -57.29) * mm, "end": v(-90.47, -58.38) * mm});
            skLineSegment(sketch, "E39.51.3", {"start": v(-90.47, -58.38) * mm, "end": v(-87.93, -62.15) * mm});
            skLineSegment(sketch, "E39.51.4", {"start": v(-90.75, -66.17) * mm, "end": v(-87.9, -64.04) * mm});
            skLineSegment(sketch, "E39.51.5", {"start": v(-87.93, -62.15) * mm, "end": v(-87.9, -64.04) * mm});
            skLineSegment(sketch, "E39.51.6", {"start": v(-90.75, -66.17) * mm, "end": v(-95.5, -59.12) * mm});
            skLineSegment(sketch, "E39.51.7", {"start": v(-95.5, -59.12) * mm, "end": v(-92.44, -57.29) * mm});
            skLineSegment(sketch, "E39.51.8", {"start": v(-90.75, -66.17) * mm, "end": v(-87.9, -64.04) * mm});
            skLineSegment(sketch, "E39.51.9", {"start": v(-90.75, -66.17) * mm, "end": v(-87.9, -64.04) * mm});
            skLineSegment(sketch, "E39.51.10", {"start": v(-95.5, -59.12) * mm, "end": v(-92.44, -57.29) * mm});
            skLineSegment(sketch, "E39.52.0", {"start": v(-88.91, -68.63) * mm, "end": v(-86.06, -66.49) * mm});
            skLineSegment(sketch, "E39.52.1", {"start": v(-88.91, -68.63) * mm, "end": v(-83.47, -75.15) * mm});
            skLineSegment(sketch, "E39.52.2", {"start": v(-86.06, -66.49) * mm, "end": v(-84, -67.37) * mm});
            skLineSegment(sketch, "E39.52.3", {"start": v(-84, -67.37) * mm, "end": v(-81.08, -70.86) * mm});
            skLineSegment(sketch, "E39.52.4", {"start": v(-83.47, -75.15) * mm, "end": v(-80.85, -72.74) * mm});
            skLineSegment(sketch, "E39.52.5", {"start": v(-81.08, -70.86) * mm, "end": v(-80.85, -72.74) * mm});
            skLineSegment(sketch, "E39.52.6", {"start": v(-83.47, -75.15) * mm, "end": v(-88.91, -68.63) * mm});
            skLineSegment(sketch, "E39.52.7", {"start": v(-88.91, -68.63) * mm, "end": v(-86.06, -66.49) * mm});
            skLineSegment(sketch, "E39.52.8", {"start": v(-83.47, -75.15) * mm, "end": v(-80.85, -72.74) * mm});
            skLineSegment(sketch, "E39.52.9", {"start": v(-83.47, -75.15) * mm, "end": v(-80.85, -72.74) * mm});
            skLineSegment(sketch, "E39.52.10", {"start": v(-88.91, -68.63) * mm, "end": v(-86.06, -66.49) * mm});
            skLineSegment(sketch, "E39.53.0", {"start": v(-81.38, -77.4) * mm, "end": v(-78.77, -74.99) * mm});
            skLineSegment(sketch, "E39.53.1", {"start": v(-81.38, -77.4) * mm, "end": v(-75.3, -83.34) * mm});
            skLineSegment(sketch, "E39.53.2", {"start": v(-78.77, -74.99) * mm, "end": v(-76.62, -75.65) * mm});
            skLineSegment(sketch, "E39.53.3", {"start": v(-76.62, -75.65) * mm, "end": v(-73.36, -78.83) * mm});
            skLineSegment(sketch, "E39.53.4", {"start": v(-75.3, -83.34) * mm, "end": v(-72.95, -80.66) * mm});
            skLineSegment(sketch, "E39.53.5", {"start": v(-73.36, -78.83) * mm, "end": v(-72.95, -80.66) * mm});
            skLineSegment(sketch, "E39.53.6", {"start": v(-75.3, -83.34) * mm, "end": v(-81.38, -77.4) * mm});
            skLineSegment(sketch, "E39.53.7", {"start": v(-81.38, -77.4) * mm, "end": v(-78.77, -74.99) * mm});
            skLineSegment(sketch, "E39.53.8", {"start": v(-75.3, -83.34) * mm, "end": v(-72.95, -80.66) * mm});
            skLineSegment(sketch, "E39.53.9", {"start": v(-75.3, -83.34) * mm, "end": v(-72.95, -80.66) * mm});
            skLineSegment(sketch, "E39.53.10", {"start": v(-81.38, -77.4) * mm, "end": v(-78.77, -74.99) * mm});
            skLineSegment(sketch, "E39.54.0", {"start": v(-73, -85.36) * mm, "end": v(-70.64, -82.69) * mm});
            skLineSegment(sketch, "E39.54.1", {"start": v(-73, -85.36) * mm, "end": v(-66.33, -90.64) * mm});
            skLineSegment(sketch, "E39.54.2", {"start": v(-70.64, -82.69) * mm, "end": v(-68.43, -83.13) * mm});
            skLineSegment(sketch, "E39.54.3", {"start": v(-68.43, -83.13) * mm, "end": v(-64.87, -85.95) * mm});
            skLineSegment(sketch, "E39.54.4", {"start": v(-66.33, -90.64) * mm, "end": v(-64.26, -87.74) * mm});
            skLineSegment(sketch, "E39.54.5", {"start": v(-64.87, -85.95) * mm, "end": v(-64.26, -87.74) * mm});
            skLineSegment(sketch, "E39.54.6", {"start": v(-66.33, -90.64) * mm, "end": v(-73, -85.36) * mm});
            skLineSegment(sketch, "E39.54.7", {"start": v(-73, -85.36) * mm, "end": v(-70.64, -82.69) * mm});
            skLineSegment(sketch, "E39.54.8", {"start": v(-66.33, -90.64) * mm, "end": v(-64.26, -87.74) * mm});
            skLineSegment(sketch, "E39.54.9", {"start": v(-66.33, -90.64) * mm, "end": v(-64.26, -87.74) * mm});
            skLineSegment(sketch, "E39.54.10", {"start": v(-73, -85.36) * mm, "end": v(-70.64, -82.69) * mm});
            skLineSegment(sketch, "E39.55.0", {"start": v(-63.83, -92.42) * mm, "end": v(-61.77, -89.51) * mm});
            skLineSegment(sketch, "E39.55.1", {"start": v(-63.83, -92.42) * mm, "end": v(-56.66, -96.98) * mm});
            skLineSegment(sketch, "E39.55.2", {"start": v(-61.77, -89.51) * mm, "end": v(-59.52, -89.72) * mm});
            skLineSegment(sketch, "E39.55.3", {"start": v(-59.52, -89.72) * mm, "end": v(-55.69, -92.16) * mm});
            skLineSegment(sketch, "E39.55.4", {"start": v(-56.66, -96.98) * mm, "end": v(-54.9, -93.88) * mm});
            skLineSegment(sketch, "E39.55.5", {"start": v(-55.69, -92.16) * mm, "end": v(-54.9, -93.88) * mm});
            skLineSegment(sketch, "E39.55.6", {"start": v(-56.66, -96.98) * mm, "end": v(-63.83, -92.42) * mm});
            skLineSegment(sketch, "E39.55.7", {"start": v(-63.83, -92.42) * mm, "end": v(-61.77, -89.51) * mm});
            skLineSegment(sketch, "E39.55.8", {"start": v(-56.66, -96.98) * mm, "end": v(-54.9, -93.88) * mm});
            skLineSegment(sketch, "E39.55.9", {"start": v(-56.66, -96.98) * mm, "end": v(-54.9, -93.88) * mm});
            skLineSegment(sketch, "E39.55.10", {"start": v(-63.83, -92.42) * mm, "end": v(-61.77, -89.51) * mm});
            skLineSegment(sketch, "E39.56.0", {"start": v(-53.99, -98.49) * mm, "end": v(-52.24, -95.39) * mm});
            skLineSegment(sketch, "E39.56.1", {"start": v(-53.99, -98.49) * mm, "end": v(-46.39, -102.3) * mm});
            skLineSegment(sketch, "E39.56.2", {"start": v(-52.24, -95.39) * mm, "end": v(-49.98, -95.37) * mm});
            skLineSegment(sketch, "E39.56.3", {"start": v(-49.98, -95.37) * mm, "end": v(-45.92, -97.4) * mm});
            skLineSegment(sketch, "E39.56.4", {"start": v(-46.39, -102.3) * mm, "end": v(-44.96, -99.03) * mm});
            skLineSegment(sketch, "E39.56.5", {"start": v(-45.92, -97.4) * mm, "end": v(-44.96, -99.03) * mm});
            skLineSegment(sketch, "E39.56.6", {"start": v(-46.39, -102.3) * mm, "end": v(-53.99, -98.49) * mm});
            skLineSegment(sketch, "E39.56.7", {"start": v(-53.99, -98.49) * mm, "end": v(-52.24, -95.39) * mm});
            skLineSegment(sketch, "E39.56.8", {"start": v(-46.39, -102.3) * mm, "end": v(-44.96, -99.03) * mm});
            skLineSegment(sketch, "E39.56.9", {"start": v(-46.39, -102.3) * mm, "end": v(-44.96, -99.03) * mm});
            skLineSegment(sketch, "E39.56.10", {"start": v(-53.99, -98.49) * mm, "end": v(-52.24, -95.39) * mm});
            skLineSegment(sketch, "E39.57.0", {"start": v(-43.58, -103.52) * mm, "end": v(-42.15, -100.25) * mm});
            skLineSegment(sketch, "E39.57.1", {"start": v(-43.58, -103.52) * mm, "end": v(-35.62, -106.52) * mm});
            skLineSegment(sketch, "E39.57.2", {"start": v(-42.15, -100.25) * mm, "end": v(-39.91, -100) * mm});
            skLineSegment(sketch, "E39.57.3", {"start": v(-39.91, -100) * mm, "end": v(-35.66, -101.6) * mm});
            skLineSegment(sketch, "E39.57.4", {"start": v(-35.62, -106.52) * mm, "end": v(-34.54, -103.12) * mm});
            skLineSegment(sketch, "E39.57.5", {"start": v(-35.66, -101.6) * mm, "end": v(-34.54, -103.12) * mm});
            skLineSegment(sketch, "E39.57.6", {"start": v(-35.62, -106.52) * mm, "end": v(-43.58, -103.52) * mm});
            skLineSegment(sketch, "E39.57.7", {"start": v(-43.58, -103.52) * mm, "end": v(-42.15, -100.25) * mm});
            skLineSegment(sketch, "E39.57.8", {"start": v(-35.62, -106.52) * mm, "end": v(-34.54, -103.12) * mm});
            skLineSegment(sketch, "E39.57.9", {"start": v(-35.62, -106.52) * mm, "end": v(-34.54, -103.12) * mm});
            skLineSegment(sketch, "E39.57.10", {"start": v(-43.58, -103.52) * mm, "end": v(-42.15, -100.25) * mm});
            skLineSegment(sketch, "E39.58.0", {"start": v(-32.7, -107.45) * mm, "end": v(-31.62, -104.06) * mm});
            skLineSegment(sketch, "E39.58.1", {"start": v(-32.7, -107.45) * mm, "end": v(-24.48, -109.62) * mm});
            skLineSegment(sketch, "E39.58.2", {"start": v(-31.62, -104.06) * mm, "end": v(-29.42, -103.58) * mm});
            skLineSegment(sketch, "E39.58.3", {"start": v(-29.42, -103.58) * mm, "end": v(-25.02, -104.73) * mm});
            skLineSegment(sketch, "E39.58.4", {"start": v(-24.48, -109.62) * mm, "end": v(-23.75, -106.13) * mm});
            skLineSegment(sketch, "E39.58.5", {"start": v(-25.02, -104.73) * mm, "end": v(-23.75, -106.13) * mm});
            skLineSegment(sketch, "E39.58.6", {"start": v(-24.48, -109.62) * mm, "end": v(-32.7, -107.45) * mm});
            skLineSegment(sketch, "E39.58.7", {"start": v(-32.7, -107.45) * mm, "end": v(-31.62, -104.06) * mm});
            skLineSegment(sketch, "E39.58.8", {"start": v(-24.48, -109.62) * mm, "end": v(-23.75, -106.13) * mm});
            skLineSegment(sketch, "E39.58.9", {"start": v(-24.48, -109.62) * mm, "end": v(-23.75, -106.13) * mm});
            skLineSegment(sketch, "E39.58.10", {"start": v(-32.7, -107.45) * mm, "end": v(-31.62, -104.06) * mm});
            skLineSegment(sketch, "E39.59.0", {"start": v(-21.48, -110.24) * mm, "end": v(-20.75, -106.76) * mm});
            skLineSegment(sketch, "E39.59.1", {"start": v(-21.48, -110.24) * mm, "end": v(-13.08, -111.55) * mm});
            skLineSegment(sketch, "E39.59.2", {"start": v(-20.75, -106.76) * mm, "end": v(-18.61, -106.05) * mm});
            skLineSegment(sketch, "E39.59.3", {"start": v(-18.61, -106.05) * mm, "end": v(-14.12, -106.75) * mm});
            skLineSegment(sketch, "E39.59.4", {"start": v(-13.08, -111.55) * mm, "end": v(-12.71, -108) * mm});
            skLineSegment(sketch, "E39.59.5", {"start": v(-14.12, -106.75) * mm, "end": v(-12.71, -108) * mm});
            skLineSegment(sketch, "E39.59.6", {"start": v(-13.08, -111.55) * mm, "end": v(-21.48, -110.24) * mm});
            skLineSegment(sketch, "E39.59.7", {"start": v(-21.48, -110.24) * mm, "end": v(-20.75, -106.76) * mm});
            skLineSegment(sketch, "E39.59.8", {"start": v(-13.08, -111.55) * mm, "end": v(-12.71, -108) * mm});
            skLineSegment(sketch, "E39.59.9", {"start": v(-13.08, -111.55) * mm, "end": v(-12.71, -108) * mm});
            skLineSegment(sketch, "E39.59.10", {"start": v(-21.48, -110.24) * mm, "end": v(-20.75, -106.76) * mm});
            skLineSegment(sketch, "E39.60.0", {"start": v(-10.03, -111.87) * mm, "end": v(-9.67, -108.32) * mm});
            skLineSegment(sketch, "E39.60.1", {"start": v(-10.03, -111.87) * mm, "end": v(-1.54, -112.3) * mm});
            skLineSegment(sketch, "E39.60.2", {"start": v(-9.67, -108.32) * mm, "end": v(-7.6, -107.4) * mm});
            skLineSegment(sketch, "E39.60.3", {"start": v(-7.6, -107.4) * mm, "end": v(-3.07, -107.64) * mm});
            skLineSegment(sketch, "E39.60.4", {"start": v(-1.54, -112.3) * mm, "end": v(-1.54, -108.74) * mm});
            skLineSegment(sketch, "E39.60.5", {"start": v(-3.07, -107.64) * mm, "end": v(-1.54, -108.74) * mm});
            skLineSegment(sketch, "E39.60.6", {"start": v(-1.54, -112.3) * mm, "end": v(-10.03, -111.87) * mm});
            skLineSegment(sketch, "E39.60.7", {"start": v(-10.03, -111.87) * mm, "end": v(-9.67, -108.32) * mm});
            skLineSegment(sketch, "E39.60.8", {"start": v(-1.54, -112.3) * mm, "end": v(-1.54, -108.74) * mm});
            skLineSegment(sketch, "E39.60.9", {"start": v(-1.54, -112.3) * mm, "end": v(-1.54, -108.74) * mm});
            skLineSegment(sketch, "E39.60.10", {"start": v(-10.03, -111.87) * mm, "end": v(-9.67, -108.32) * mm});
            skSolve(sketch);
        }
        {
            var Q0;
            Q0 = qSketchRegion(id + "F10", true);
            extrude(context, id + "F11", {"entities" : qUnion([Q0]), "operationType" : NewBodyOperationType.REMOVE, "depth" : 25.4 * mm});
        }
    });
